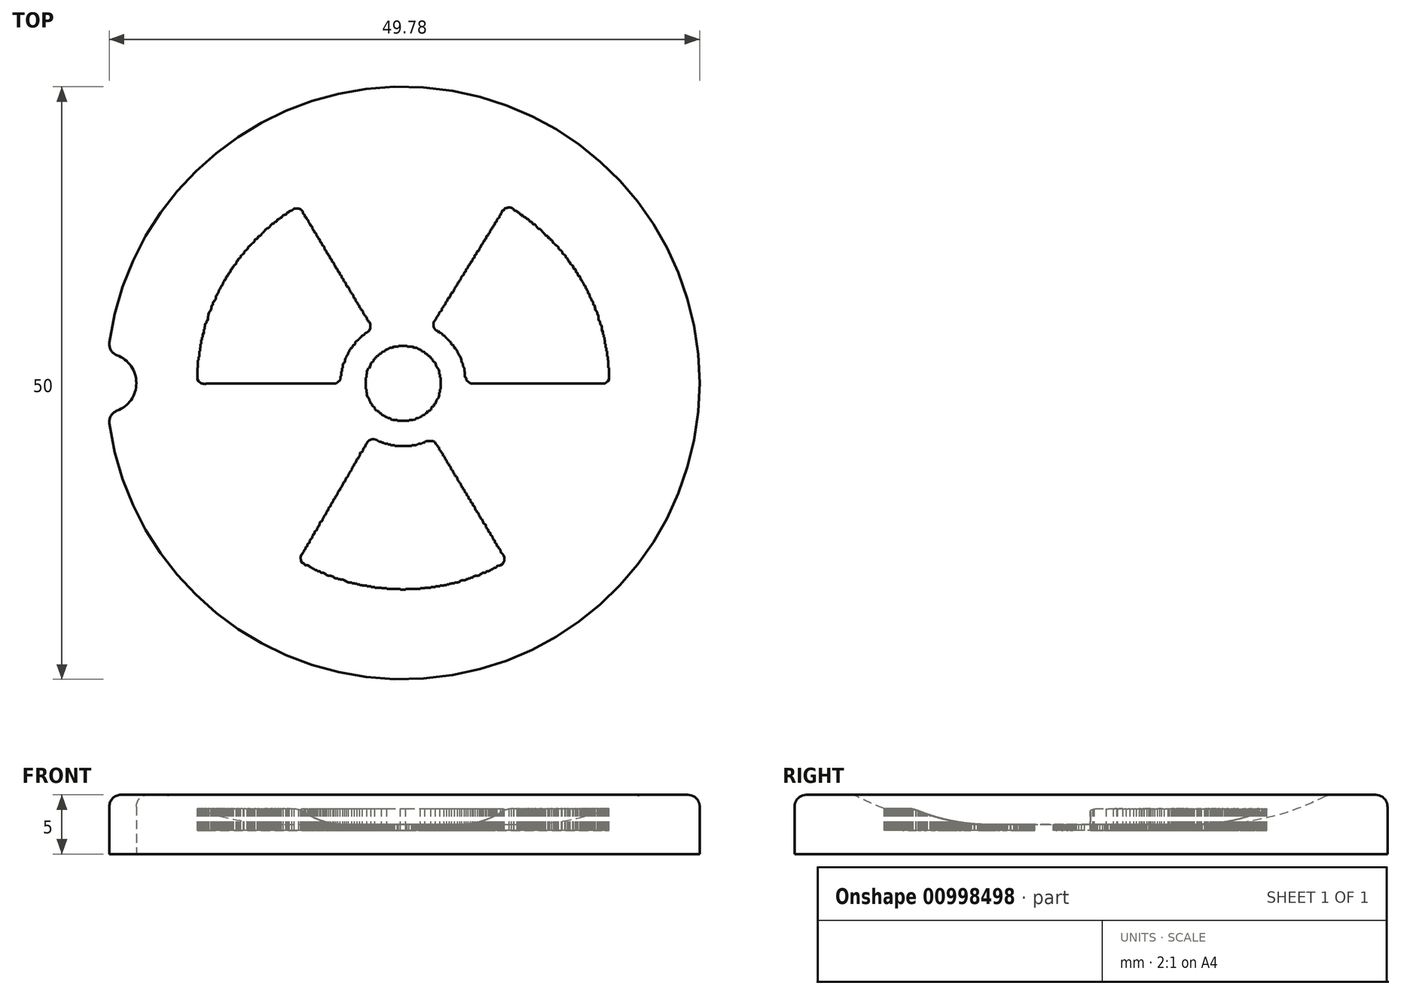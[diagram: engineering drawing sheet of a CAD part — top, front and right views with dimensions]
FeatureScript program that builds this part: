
annotation { "Feature Type Name" : "Feature", "Feature Type Description" : "" }
export const myFeature = defineFeature(function(context is Context, id is Id, definition is map)
    precondition{}
    {
        {
            var Q0;
            Q0=qCreatedBy(makeId("Front.planeOp"),FACE);
            var sketch = newSketch(context, id + "F0", { "sketchPlane" : qUnion([Q0])});
            skLineSegment(sketch, "E0.bottom", {"start": v(0, 0) * mm, "end": v(-25, 0) * mm});
            skLineSegment(sketch, "E0.top", {"start": v(-20, 5) * mm, "end": v(-25, 5) * mm});
            skLineSegment(sketch, "E0.left", {"start": v(0, 0) * mm, "end": v(0, 2.5) * mm});
            skLineSegment(sketch, "E0.right", {"start": v(-25, 0) * mm, "end": v(-25, 5) * mm});
            skArc(sketch, "E1", {"start": v(-20, 5) * mm, "mid": v(-15.15, 3.13) * mm, "end": v(-10, 2.5) * mm});
            skLineSegment(sketch, "E2", {"start": v(-10, 2.5) * mm, "end": v(0, 2.5) * mm});
            skPoint(sketch, "E3.orphan", {"position": v(0, 5) * mm});
            skSolve(sketch);
        }
        {
            var Q0;
            Q0 = qSketchRegion(id + "F0", true);
            var Q1;
            Q1=sQuery(id+"F0.wireOp",EDGE,"E0.left");
            revolve(context, id + "F1", {"surfaceOperationType" : NewSurfaceOperationType.NEW, "entities" : qUnion([Q0]), "axis" : qUnion([Q1]), "revolveType" : RevolveType.FULL});
        }
        {
            var Q0;
            Q0=makeQuery(id+"F1.opRevolve","SWEPT_EDGE",EDGE,{"disambiguationData":[OSD([sQuery(id+"F0.wireOp",EDGE,"E0.top"),sQuery(id+"F0.wireOp",EDGE,"E0.right")])]});
            var Q1;
            Q1=makeQuery(id+"F1.opRevolve","SWEPT_FACE",FACE,{"disambiguationData":[OSD([sQuery(id+"F0.wireOp",EDGE,"E2")])]});
            var Q2;
            Q2=makeQuery(id+"F1.opRevolve","SWEPT_EDGE",EDGE,{"disambiguationData":[OSD([sQuery(id+"F0.wireOp",EDGE,"E0.top"),sQuery(id+"F0.wireOp",EDGE,"E1")])]});
            fillet(context, id + "F2", {"entities" : qUnion([Q0, Q1, Q2]), "radius" : 1 * mm, "tangentPropagation" : true, "allowEdgeOverflow" : false});
        }
        {
            var Q0;
            Q0=qCreatedBy(makeId("Top.planeOp"),FACE);
            var sketch = newSketch(context, id + "F3", { "sketchPlane" : qUnion([Q0])});
            skLineSegment(sketch, "E4", {"start": v(0, 0) * mm, "end": v(-25, 0) * mm});
            skCircle(sketch, "E5", {"center": v(-25, 0) * mm, "radius": 2.5 * mm});
            skSolve(sketch);
        }
        {
            var Q0;
            Q0 = qSketchRegion(id + "F3", true);
            extrude(context, id + "F4", {"entities" : qUnion([Q0]), "operationType" : NewBodyOperationType.REMOVE, "depth" : 25 * mm, "offsetDistance" : 25 * mm});
        }
        {
            var Q0;
            Q0=makeQuery(id+"F4.boolean.opBoolean","INTERSECT",EDGE,{"derivedFrom":[makeQuery(id+"F1.opRevolve","SWEPT_FACE",FACE,{"disambiguationData":[OSD([sQuery(id+"F0.wireOp",EDGE,"E0.top")])]}),makeQuery(id+"F4.opExtrude","SWEPT_FACE",FACE,{"disambiguationData":[OSD([sQuery(id+"F3.wireOp",EDGE,"E5")])]})]});
            fillet(context, id + "F5", {"entities" : qUnion([Q0]), "radius" : 1 * mm, "tangentPropagation" : true, "allowEdgeOverflow" : false});
        }
        {
            var Q0;
            Q0=qCreatedBy(makeId("Top.planeOp"),FACE);
            cPlane(context, id + "F6", {"entities" : qUnion([Q0]), "cplaneType" : CPlaneType.OFFSET, "offset" : 5 * mm, "width" : 150 * mm, "height" : 150 * mm});
        }
        {
            var Q0;
            Q0=qCreatedBy(id+"F6.planeOp",FACE);
            var sketch = newSketch(context, id + "F7", { "sketchPlane" : qUnion([Q0])});
            skLineSegment(sketch, "E6", {"start": v(8.93, 14.83) * mm, "end": v(8.54, 14.72) * mm});
            skLineSegment(sketch, "E7", {"start": v(8.54, 14.72) * mm, "end": v(8.48, 14.56) * mm});
            skLineSegment(sketch, "E8", {"start": v(8.48, 14.56) * mm, "end": v(8.37, 14.56) * mm});
            skLineSegment(sketch, "E9", {"start": v(8.37, 14.56) * mm, "end": v(8.32, 14.45) * mm});
            skLineSegment(sketch, "E10", {"start": v(8.32, 14.45) * mm, "end": v(8.32, 14.33) * mm});
            skLineSegment(sketch, "E11", {"start": v(8.32, 14.33) * mm, "end": v(8.26, 14.33) * mm});
            skLineSegment(sketch, "E12", {"start": v(8.26, 14.33) * mm, "end": v(8.26, 14.22) * mm});
            skLineSegment(sketch, "E13", {"start": v(8.26, 14.22) * mm, "end": v(8.15, 14.17) * mm});
            skLineSegment(sketch, "E14", {"start": v(8.15, 14.17) * mm, "end": v(8.1, 13.95) * mm});
            skLineSegment(sketch, "E15", {"start": v(8.1, 13.95) * mm, "end": v(7.93, 13.84) * mm});
            skLineSegment(sketch, "E16", {"start": v(7.93, 13.84) * mm, "end": v(7.87, 13.61) * mm});
            skLineSegment(sketch, "E17", {"start": v(7.87, 13.61) * mm, "end": v(7.76, 13.56) * mm});
            skLineSegment(sketch, "E18", {"start": v(7.76, 13.56) * mm, "end": v(7.7, 13.34) * mm});
            skLineSegment(sketch, "E19", {"start": v(7.7, 13.34) * mm, "end": v(7.6, 13.28) * mm});
            skLineSegment(sketch, "E20", {"start": v(7.6, 13.28) * mm, "end": v(7.6, 13.17) * mm});
            skLineSegment(sketch, "E21", {"start": v(7.6, 13.17) * mm, "end": v(7.49, 13.11) * mm});
            skLineSegment(sketch, "E22", {"start": v(7.49, 13.11) * mm, "end": v(7.49, 13) * mm});
            skLineSegment(sketch, "E23", {"start": v(7.49, 13) * mm, "end": v(7.38, 12.95) * mm});
            skLineSegment(sketch, "E24", {"start": v(7.38, 12.95) * mm, "end": v(7.38, 12.84) * mm});
            skLineSegment(sketch, "E25", {"start": v(7.38, 12.84) * mm, "end": v(7.32, 12.84) * mm});
            skLineSegment(sketch, "E26", {"start": v(7.32, 12.84) * mm, "end": v(7.32, 12.73) * mm});
            skLineSegment(sketch, "E27", {"start": v(7.32, 12.73) * mm, "end": v(7.26, 12.62) * mm});
            skLineSegment(sketch, "E28", {"start": v(7.26, 12.62) * mm, "end": v(7.15, 12.56) * mm});
            skLineSegment(sketch, "E29", {"start": v(7.15, 12.56) * mm, "end": v(7.15, 12.45) * mm});
            skLineSegment(sketch, "E30", {"start": v(7.15, 12.45) * mm, "end": v(7.04, 12.4) * mm});
            skLineSegment(sketch, "E31", {"start": v(7.04, 12.4) * mm, "end": v(6.99, 12.17) * mm});
            skLineSegment(sketch, "E32", {"start": v(6.99, 12.17) * mm, "end": v(6.88, 12.12) * mm});
            skLineSegment(sketch, "E33", {"start": v(6.88, 12.12) * mm, "end": v(6.88, 12) * mm});
            skLineSegment(sketch, "E34", {"start": v(6.88, 12) * mm, "end": v(6.77, 11.95) * mm});
            skLineSegment(sketch, "E35", {"start": v(6.77, 11.95) * mm, "end": v(6.7, 11.73) * mm});
            skLineSegment(sketch, "E36", {"start": v(6.7, 11.73) * mm, "end": v(6.6, 11.67) * mm});
            skLineSegment(sketch, "E37", {"start": v(6.6, 11.67) * mm, "end": v(6.6, 11.56) * mm});
            skLineSegment(sketch, "E38", {"start": v(6.6, 11.56) * mm, "end": v(6.49, 11.5) * mm});
            skLineSegment(sketch, "E39", {"start": v(6.49, 11.5) * mm, "end": v(6.49, 11.4) * mm});
            skLineSegment(sketch, "E40", {"start": v(6.49, 11.4) * mm, "end": v(6.43, 11.4) * mm});
            skLineSegment(sketch, "E41", {"start": v(6.43, 11.4) * mm, "end": v(6.43, 11.28) * mm});
            skLineSegment(sketch, "E42", {"start": v(6.43, 11.28) * mm, "end": v(6.38, 11.17) * mm});
            skLineSegment(sketch, "E43", {"start": v(6.38, 11.17) * mm, "end": v(6.21, 11.06) * mm});
            skLineSegment(sketch, "E44", {"start": v(6.21, 11.06) * mm, "end": v(6.16, 10.84) * mm});
            skLineSegment(sketch, "E45", {"start": v(6.16, 10.84) * mm, "end": v(6.04, 10.79) * mm});
            skLineSegment(sketch, "E46", {"start": v(6.04, 10.79) * mm, "end": v(5.99, 10.56) * mm});
            skLineSegment(sketch, "E47", {"start": v(5.99, 10.56) * mm, "end": v(5.88, 10.5) * mm});
            skLineSegment(sketch, "E48", {"start": v(5.88, 10.5) * mm, "end": v(5.82, 10.29) * mm});
            skLineSegment(sketch, "E49", {"start": v(5.82, 10.29) * mm, "end": v(5.71, 10.23) * mm});
            skLineSegment(sketch, "E50", {"start": v(5.71, 10.23) * mm, "end": v(5.71, 10.12) * mm});
            skLineSegment(sketch, "E51", {"start": v(5.71, 10.12) * mm, "end": v(5.6, 10.06) * mm});
            skLineSegment(sketch, "E52", {"start": v(5.6, 10.06) * mm, "end": v(5.6, 9.95) * mm});
            skLineSegment(sketch, "E53", {"start": v(5.6, 9.95) * mm, "end": v(5.49, 9.9) * mm});
            skLineSegment(sketch, "E54", {"start": v(5.49, 9.9) * mm, "end": v(5.43, 9.68) * mm});
            skLineSegment(sketch, "E55", {"start": v(5.43, 9.68) * mm, "end": v(5.32, 9.62) * mm});
            skLineSegment(sketch, "E56", {"start": v(5.32, 9.62) * mm, "end": v(5.27, 9.4) * mm});
            skLineSegment(sketch, "E57", {"start": v(5.27, 9.4) * mm, "end": v(5.16, 9.34) * mm});
            skLineSegment(sketch, "E58", {"start": v(5.16, 9.34) * mm, "end": v(5.1, 9.12) * mm});
            skLineSegment(sketch, "E59", {"start": v(5.1, 9.12) * mm, "end": v(4.94, 9.01) * mm});
            skLineSegment(sketch, "E60", {"start": v(4.94, 9.01) * mm, "end": v(4.82, 8.68) * mm});
            skLineSegment(sketch, "E61", {"start": v(4.82, 8.68) * mm, "end": v(4.71, 8.62) * mm});
            skLineSegment(sketch, "E62", {"start": v(4.71, 8.62) * mm, "end": v(4.71, 8.51) * mm});
            skLineSegment(sketch, "E63", {"start": v(4.71, 8.51) * mm, "end": v(4.6, 8.46) * mm});
            skLineSegment(sketch, "E64", {"start": v(4.6, 8.46) * mm, "end": v(4.55, 8.23) * mm});
            skLineSegment(sketch, "E65", {"start": v(4.55, 8.23) * mm, "end": v(4.44, 8.18) * mm});
            skLineSegment(sketch, "E66", {"start": v(4.44, 8.18) * mm, "end": v(4.44, 8.07) * mm});
            skLineSegment(sketch, "E67", {"start": v(4.44, 8.07) * mm, "end": v(4.33, 8.01) * mm});
            skLineSegment(sketch, "E68", {"start": v(4.33, 8.01) * mm, "end": v(4.33, 7.9) * mm});
            skLineSegment(sketch, "E69", {"start": v(4.33, 7.9) * mm, "end": v(4.27, 7.9) * mm});
            skLineSegment(sketch, "E70", {"start": v(4.27, 7.9) * mm, "end": v(4.27, 7.8) * mm});
            skLineSegment(sketch, "E71", {"start": v(4.27, 7.8) * mm, "end": v(4.21, 7.68) * mm});
            skLineSegment(sketch, "E72", {"start": v(4.21, 7.68) * mm, "end": v(4.05, 7.57) * mm});
            skLineSegment(sketch, "E73", {"start": v(4.05, 7.57) * mm, "end": v(3.94, 7.24) * mm});
            skLineSegment(sketch, "E74", {"start": v(3.94, 7.24) * mm, "end": v(3.77, 7.13) * mm});
            skLineSegment(sketch, "E75", {"start": v(3.77, 7.13) * mm, "end": v(3.72, 6.9) * mm});
            skLineSegment(sketch, "E76", {"start": v(3.72, 6.9) * mm, "end": v(3.6, 6.85) * mm});
            skLineSegment(sketch, "E77", {"start": v(3.6, 6.85) * mm, "end": v(3.55, 6.63) * mm});
            skLineSegment(sketch, "E78", {"start": v(3.55, 6.63) * mm, "end": v(3.44, 6.57) * mm});
            skLineSegment(sketch, "E79", {"start": v(3.44, 6.57) * mm, "end": v(3.44, 6.46) * mm});
            skLineSegment(sketch, "E80", {"start": v(3.44, 6.46) * mm, "end": v(3.33, 6.4) * mm});
            skLineSegment(sketch, "E81", {"start": v(3.33, 6.4) * mm, "end": v(3.33, 6.3) * mm});
            skLineSegment(sketch, "E82", {"start": v(3.33, 6.3) * mm, "end": v(3.27, 6.3) * mm});
            skLineSegment(sketch, "E83", {"start": v(3.27, 6.3) * mm, "end": v(3.27, 6.18) * mm});
            skLineSegment(sketch, "E84", {"start": v(3.27, 6.18) * mm, "end": v(3.22, 6.07) * mm});
            skLineSegment(sketch, "E85", {"start": v(3.22, 6.07) * mm, "end": v(3.05, 5.96) * mm});
            skLineSegment(sketch, "E86", {"start": v(3.05, 5.96) * mm, "end": v(3, 5.74) * mm});
            skLineSegment(sketch, "E87", {"start": v(3, 5.74) * mm, "end": v(2.88, 5.68) * mm});
            skLineSegment(sketch, "E88", {"start": v(2.88, 5.68) * mm, "end": v(2.88, 5.57) * mm});
            skLineSegment(sketch, "E89", {"start": v(2.88, 5.57) * mm, "end": v(2.77, 5.52) * mm});
            skLineSegment(sketch, "E90", {"start": v(2.77, 5.52) * mm, "end": v(2.77, 5.4) * mm});
            skLineSegment(sketch, "E91", {"start": v(2.77, 5.4) * mm, "end": v(2.72, 5.4) * mm});
            skLineSegment(sketch, "E92", {"start": v(2.72, 5.4) * mm, "end": v(2.72, 5.3) * mm});
            skLineSegment(sketch, "E93", {"start": v(2.72, 5.3) * mm, "end": v(2.66, 5.3) * mm});
            skLineSegment(sketch, "E94", {"start": v(2.66, 5.3) * mm, "end": v(2.66, 5.18) * mm});
            skLineSegment(sketch, "E95", {"start": v(2.66, 5.18) * mm, "end": v(2.6, 5.18) * mm});
            skLineSegment(sketch, "E96", {"start": v(2.6, 5.18) * mm, "end": v(2.55, 5.07) * mm});
            skLineSegment(sketch, "E97", {"start": v(2.55, 5.07) * mm, "end": v(2.55, 4.74) * mm});
            skLineSegment(sketch, "E98", {"start": v(2.55, 4.74) * mm, "end": v(2.66, 4.57) * mm});
            skLineSegment(sketch, "E99", {"start": v(2.66, 4.57) * mm, "end": v(2.83, 4.4) * mm});
            skLineSegment(sketch, "E100", {"start": v(2.83, 4.4) * mm, "end": v(2.94, 4.4) * mm});
            skLineSegment(sketch, "E101", {"start": v(2.94, 4.4) * mm, "end": v(3.05, 4.24) * mm});
            skLineSegment(sketch, "E102", {"start": v(3.05, 4.24) * mm, "end": v(3.16, 4.24) * mm});
            skLineSegment(sketch, "E103", {"start": v(3.16, 4.24) * mm, "end": v(3.33, 4.13) * mm});
            skLineSegment(sketch, "E104", {"start": v(3.33, 4.13) * mm, "end": v(3.33, 4.02) * mm});
            skLineSegment(sketch, "E105", {"start": v(3.33, 4.02) * mm, "end": v(3.44, 4.02) * mm});
            skLineSegment(sketch, "E106", {"start": v(3.44, 4.02) * mm, "end": v(3.5, 3.96) * mm});
            skLineSegment(sketch, "E107", {"start": v(3.5, 3.96) * mm, "end": v(3.55, 3.9) * mm});
            skLineSegment(sketch, "E108", {"start": v(3.55, 3.9) * mm, "end": v(3.55, 3.85) * mm});
            skLineSegment(sketch, "E109", {"start": v(3.55, 3.85) * mm, "end": v(3.6, 3.85) * mm});
            skLineSegment(sketch, "E110", {"start": v(3.6, 3.85) * mm, "end": v(3.6, 3.8) * mm});
            skLineSegment(sketch, "E111", {"start": v(3.6, 3.8) * mm, "end": v(3.66, 3.8) * mm});
            skLineSegment(sketch, "E112", {"start": v(3.66, 3.8) * mm, "end": v(3.66, 3.74) * mm});
            skLineSegment(sketch, "E113", {"start": v(3.66, 3.74) * mm, "end": v(3.72, 3.74) * mm});
            skLineSegment(sketch, "E114", {"start": v(3.72, 3.74) * mm, "end": v(3.72, 3.69) * mm});
            skLineSegment(sketch, "E115", {"start": v(3.72, 3.69) * mm, "end": v(3.77, 3.69) * mm});
            skLineSegment(sketch, "E116", {"start": v(3.77, 3.69) * mm, "end": v(3.77, 3.63) * mm});
            skLineSegment(sketch, "E117", {"start": v(3.77, 3.63) * mm, "end": v(3.83, 3.63) * mm});
            skLineSegment(sketch, "E118", {"start": v(3.83, 3.63) * mm, "end": v(3.83, 3.58) * mm});
            skLineSegment(sketch, "E119", {"start": v(3.83, 3.58) * mm, "end": v(3.88, 3.58) * mm});
            skLineSegment(sketch, "E120", {"start": v(3.88, 3.58) * mm, "end": v(3.88, 3.52) * mm});
            skLineSegment(sketch, "E121", {"start": v(3.88, 3.52) * mm, "end": v(3.94, 3.52) * mm});
            skLineSegment(sketch, "E122", {"start": v(3.94, 3.52) * mm, "end": v(3.94, 3.47) * mm});
            skLineSegment(sketch, "E123", {"start": v(3.94, 3.47) * mm, "end": v(4.05, 3.41) * mm});
            skLineSegment(sketch, "E124", {"start": v(4.05, 3.41) * mm, "end": v(4.05, 3.3) * mm});
            skLineSegment(sketch, "E125", {"start": v(4.05, 3.3) * mm, "end": v(4.1, 3.24) * mm});
            skLineSegment(sketch, "E126", {"start": v(4.1, 3.24) * mm, "end": v(4.21, 3.19) * mm});
            skLineSegment(sketch, "E127", {"start": v(4.21, 3.19) * mm, "end": v(4.27, 3.13) * mm});
            skLineSegment(sketch, "E128", {"start": v(4.27, 3.13) * mm, "end": v(4.27, 3.02) * mm});
            skLineSegment(sketch, "E129", {"start": v(4.27, 3.02) * mm, "end": v(4.44, 2.91) * mm});
            skLineSegment(sketch, "E130", {"start": v(4.44, 2.91) * mm, "end": v(4.44, 2.8) * mm});
            skLineSegment(sketch, "E131", {"start": v(4.44, 2.8) * mm, "end": v(4.55, 2.74) * mm});
            skLineSegment(sketch, "E132", {"start": v(4.55, 2.74) * mm, "end": v(4.6, 2.52) * mm});
            skLineSegment(sketch, "E133", {"start": v(4.6, 2.52) * mm, "end": v(4.66, 2.52) * mm});
            skLineSegment(sketch, "E134", {"start": v(4.66, 2.52) * mm, "end": v(4.66, 2.41) * mm});
            skLineSegment(sketch, "E135", {"start": v(4.66, 2.41) * mm, "end": v(4.71, 2.41) * mm});
            skLineSegment(sketch, "E136", {"start": v(4.71, 2.41) * mm, "end": v(4.71, 2.3) * mm});
            skLineSegment(sketch, "E137", {"start": v(4.71, 2.3) * mm, "end": v(4.77, 2.3) * mm});
            skLineSegment(sketch, "E138", {"start": v(4.77, 2.3) * mm, "end": v(4.77, 2.2) * mm});
            skLineSegment(sketch, "E139", {"start": v(4.77, 2.2) * mm, "end": v(4.82, 2.2) * mm});
            skLineSegment(sketch, "E140", {"start": v(4.82, 2.2) * mm, "end": v(4.88, 2.08) * mm});
            skLineSegment(sketch, "E141", {"start": v(4.88, 2.08) * mm, "end": v(4.94, 1.75) * mm});
            skLineSegment(sketch, "E142", {"start": v(4.94, 1.75) * mm, "end": v(5.05, 1.64) * mm});
            skLineSegment(sketch, "E143", {"start": v(5.05, 1.64) * mm, "end": v(5.05, 1.41) * mm});
            skLineSegment(sketch, "E144", {"start": v(5.05, 1.41) * mm, "end": v(5.16, 1.25) * mm});
            skLineSegment(sketch, "E145", {"start": v(5.16, 1.25) * mm, "end": v(5.16, 0.97) * mm});
            skLineSegment(sketch, "E146", {"start": v(5.16, 0.97) * mm, "end": v(5.21, 0.97) * mm});
            skLineSegment(sketch, "E147", {"start": v(5.21, 0.97) * mm, "end": v(5.21, 0.58) * mm});
            skLineSegment(sketch, "E148", {"start": v(5.21, 0.58) * mm, "end": v(5.27, 0.42) * mm});
            skLineSegment(sketch, "E149", {"start": v(5.27, 0.42) * mm, "end": v(5.32, 0.42) * mm});
            skLineSegment(sketch, "E150", {"start": v(5.32, 0.42) * mm, "end": v(5.32, 0.25) * mm});
            skLineSegment(sketch, "E151", {"start": v(5.32, 0.25) * mm, "end": v(5.66, -0.03) * mm});
            skLineSegment(sketch, "E152", {"start": v(5.66, -0.03) * mm, "end": v(5.88, -0.03) * mm});
            skLineSegment(sketch, "E153", {"start": v(5.88, -0.03) * mm, "end": v(5.93, -0.03) * mm});
            skLineSegment(sketch, "E154", {"start": v(5.93, -0.03) * mm, "end": v(5.99, -0.03) * mm});
            skLineSegment(sketch, "E155", {"start": v(5.99, -0.03) * mm, "end": v(6.04, -0.03) * mm});
            skLineSegment(sketch, "E156", {"start": v(6.04, -0.03) * mm, "end": v(6.1, -0.03) * mm});
            skLineSegment(sketch, "E157", {"start": v(6.1, -0.03) * mm, "end": v(6.16, -0.03) * mm});
            skLineSegment(sketch, "E158", {"start": v(6.16, -0.03) * mm, "end": v(6.21, -0.03) * mm});
            skLineSegment(sketch, "E159", {"start": v(6.21, -0.03) * mm, "end": v(6.27, -0.03) * mm});
            skLineSegment(sketch, "E160", {"start": v(6.27, -0.03) * mm, "end": v(6.32, -0.03) * mm});
            skLineSegment(sketch, "E161", {"start": v(6.32, -0.03) * mm, "end": v(6.38, -0.03) * mm});
            skLineSegment(sketch, "E162", {"start": v(6.38, -0.03) * mm, "end": v(6.43, -0.03) * mm});
            skLineSegment(sketch, "E163", {"start": v(6.43, -0.03) * mm, "end": v(6.49, -0.03) * mm});
            skLineSegment(sketch, "E164", {"start": v(6.49, -0.03) * mm, "end": v(6.54, -0.03) * mm});
            skLineSegment(sketch, "E165", {"start": v(6.54, -0.03) * mm, "end": v(6.6, -0.03) * mm});
            skLineSegment(sketch, "E166", {"start": v(6.6, -0.03) * mm, "end": v(6.65, -0.03) * mm});
            skLineSegment(sketch, "E167", {"start": v(6.65, -0.03) * mm, "end": v(6.7, -0.03) * mm});
            skLineSegment(sketch, "E168", {"start": v(6.7, -0.03) * mm, "end": v(6.77, -0.03) * mm});
            skLineSegment(sketch, "E169", {"start": v(6.77, -0.03) * mm, "end": v(6.82, -0.03) * mm});
            skLineSegment(sketch, "E170", {"start": v(6.82, -0.03) * mm, "end": v(6.88, -0.03) * mm});
            skLineSegment(sketch, "E171", {"start": v(6.88, -0.03) * mm, "end": v(6.93, -0.03) * mm});
            skLineSegment(sketch, "E172", {"start": v(6.93, -0.03) * mm, "end": v(6.99, -0.03) * mm});
            skLineSegment(sketch, "E173", {"start": v(6.99, -0.03) * mm, "end": v(7.04, -0.03) * mm});
            skLineSegment(sketch, "E174", {"start": v(7.04, -0.03) * mm, "end": v(7.1, -0.03) * mm});
            skLineSegment(sketch, "E175", {"start": v(7.1, -0.03) * mm, "end": v(7.15, -0.03) * mm});
            skLineSegment(sketch, "E176", {"start": v(7.15, -0.03) * mm, "end": v(7.2, -0.03) * mm});
            skLineSegment(sketch, "E177", {"start": v(7.2, -0.03) * mm, "end": v(7.26, -0.03) * mm});
            skLineSegment(sketch, "E178", {"start": v(7.26, -0.03) * mm, "end": v(7.32, -0.03) * mm});
            skLineSegment(sketch, "E179", {"start": v(7.32, -0.03) * mm, "end": v(7.38, -0.03) * mm});
            skLineSegment(sketch, "E180", {"start": v(7.38, -0.03) * mm, "end": v(7.43, -0.03) * mm});
            skLineSegment(sketch, "E181", {"start": v(7.43, -0.03) * mm, "end": v(7.49, -0.03) * mm});
            skLineSegment(sketch, "E182", {"start": v(7.49, -0.03) * mm, "end": v(7.54, -0.03) * mm});
            skLineSegment(sketch, "E183", {"start": v(7.54, -0.03) * mm, "end": v(7.6, -0.03) * mm});
            skLineSegment(sketch, "E184", {"start": v(7.6, -0.03) * mm, "end": v(7.65, -0.03) * mm});
            skLineSegment(sketch, "E185", {"start": v(7.65, -0.03) * mm, "end": v(7.7, -0.03) * mm});
            skLineSegment(sketch, "E186", {"start": v(7.7, -0.03) * mm, "end": v(7.76, -0.03) * mm});
            skLineSegment(sketch, "E187", {"start": v(7.76, -0.03) * mm, "end": v(7.82, -0.03) * mm});
            skLineSegment(sketch, "E188", {"start": v(7.82, -0.03) * mm, "end": v(7.87, -0.03) * mm});
            skLineSegment(sketch, "E189", {"start": v(7.87, -0.03) * mm, "end": v(7.93, -0.03) * mm});
            skLineSegment(sketch, "E190", {"start": v(7.93, -0.03) * mm, "end": v(7.99, -0.03) * mm});
            skLineSegment(sketch, "E191", {"start": v(7.99, -0.03) * mm, "end": v(8.04, -0.03) * mm});
            skLineSegment(sketch, "E192", {"start": v(8.04, -0.03) * mm, "end": v(8.1, -0.03) * mm});
            skLineSegment(sketch, "E193", {"start": v(8.1, -0.03) * mm, "end": v(8.15, -0.03) * mm});
            skLineSegment(sketch, "E194", {"start": v(8.15, -0.03) * mm, "end": v(8.2, -0.03) * mm});
            skLineSegment(sketch, "E195", {"start": v(8.2, -0.03) * mm, "end": v(8.26, -0.03) * mm});
            skLineSegment(sketch, "E196", {"start": v(8.26, -0.03) * mm, "end": v(8.32, -0.03) * mm});
            skLineSegment(sketch, "E197", {"start": v(8.32, -0.03) * mm, "end": v(8.37, -0.03) * mm});
            skLineSegment(sketch, "E198", {"start": v(8.37, -0.03) * mm, "end": v(8.43, -0.03) * mm});
            skLineSegment(sketch, "E199", {"start": v(8.43, -0.03) * mm, "end": v(8.48, -0.03) * mm});
            skLineSegment(sketch, "E200", {"start": v(8.48, -0.03) * mm, "end": v(8.54, -0.03) * mm});
            skLineSegment(sketch, "E201", {"start": v(8.54, -0.03) * mm, "end": v(8.6, -0.03) * mm});
            skLineSegment(sketch, "E202", {"start": v(8.6, -0.03) * mm, "end": v(8.65, -0.03) * mm});
            skLineSegment(sketch, "E203", {"start": v(8.65, -0.03) * mm, "end": v(8.7, -0.03) * mm});
            skLineSegment(sketch, "E204", {"start": v(8.7, -0.03) * mm, "end": v(8.76, -0.03) * mm});
            skLineSegment(sketch, "E205", {"start": v(8.76, -0.03) * mm, "end": v(8.82, -0.03) * mm});
            skLineSegment(sketch, "E206", {"start": v(8.82, -0.03) * mm, "end": v(8.87, -0.03) * mm});
            skLineSegment(sketch, "E207", {"start": v(8.87, -0.03) * mm, "end": v(8.93, -0.03) * mm});
            skLineSegment(sketch, "E208", {"start": v(8.93, -0.03) * mm, "end": v(8.98, -0.03) * mm});
            skLineSegment(sketch, "E209", {"start": v(8.98, -0.03) * mm, "end": v(9.04, -0.03) * mm});
            skLineSegment(sketch, "E210", {"start": v(9.04, -0.03) * mm, "end": v(9.1, -0.03) * mm});
            skLineSegment(sketch, "E211", {"start": v(9.1, -0.03) * mm, "end": v(9.15, -0.03) * mm});
            skLineSegment(sketch, "E212", {"start": v(9.15, -0.03) * mm, "end": v(9.2, -0.03) * mm});
            skLineSegment(sketch, "E213", {"start": v(9.2, -0.03) * mm, "end": v(9.26, -0.03) * mm});
            skLineSegment(sketch, "E214", {"start": v(9.26, -0.03) * mm, "end": v(9.32, -0.03) * mm});
            skLineSegment(sketch, "E215", {"start": v(9.32, -0.03) * mm, "end": v(9.37, -0.03) * mm});
            skLineSegment(sketch, "E216", {"start": v(9.37, -0.03) * mm, "end": v(9.43, -0.03) * mm});
            skLineSegment(sketch, "E217", {"start": v(9.43, -0.03) * mm, "end": v(9.48, -0.03) * mm});
            skLineSegment(sketch, "E218", {"start": v(9.48, -0.03) * mm, "end": v(9.54, -0.03) * mm});
            skLineSegment(sketch, "E219", {"start": v(9.54, -0.03) * mm, "end": v(9.6, -0.03) * mm});
            skLineSegment(sketch, "E220", {"start": v(9.6, -0.03) * mm, "end": v(9.65, -0.03) * mm});
            skLineSegment(sketch, "E221", {"start": v(9.65, -0.03) * mm, "end": v(9.7, -0.03) * mm});
            skLineSegment(sketch, "E222", {"start": v(9.7, -0.03) * mm, "end": v(9.76, -0.03) * mm});
            skLineSegment(sketch, "E223", {"start": v(9.76, -0.03) * mm, "end": v(9.82, -0.03) * mm});
            skLineSegment(sketch, "E224", {"start": v(9.82, -0.03) * mm, "end": v(9.87, -0.03) * mm});
            skLineSegment(sketch, "E225", {"start": v(9.87, -0.03) * mm, "end": v(9.93, -0.03) * mm});
            skLineSegment(sketch, "E226", {"start": v(9.93, -0.03) * mm, "end": v(9.98, -0.03) * mm});
            skLineSegment(sketch, "E227", {"start": v(9.98, -0.03) * mm, "end": v(10.04, -0.03) * mm});
            skLineSegment(sketch, "E228", {"start": v(10.04, -0.03) * mm, "end": v(10.1, -0.03) * mm});
            skLineSegment(sketch, "E229", {"start": v(10.1, -0.03) * mm, "end": v(10.15, -0.03) * mm});
            skLineSegment(sketch, "E230", {"start": v(10.15, -0.03) * mm, "end": v(10.2, -0.03) * mm});
            skLineSegment(sketch, "E231", {"start": v(10.2, -0.03) * mm, "end": v(10.26, -0.03) * mm});
            skLineSegment(sketch, "E232", {"start": v(10.26, -0.03) * mm, "end": v(10.31, -0.03) * mm});
            skLineSegment(sketch, "E233", {"start": v(10.31, -0.03) * mm, "end": v(10.37, -0.03) * mm});
            skLineSegment(sketch, "E234", {"start": v(10.37, -0.03) * mm, "end": v(10.43, -0.03) * mm});
            skLineSegment(sketch, "E235", {"start": v(10.43, -0.03) * mm, "end": v(10.48, -0.03) * mm});
            skLineSegment(sketch, "E236", {"start": v(10.48, -0.03) * mm, "end": v(10.54, -0.03) * mm});
            skLineSegment(sketch, "E237", {"start": v(10.54, -0.03) * mm, "end": v(10.6, -0.03) * mm});
            skLineSegment(sketch, "E238", {"start": v(10.6, -0.03) * mm, "end": v(10.65, -0.03) * mm});
            skLineSegment(sketch, "E239", {"start": v(10.65, -0.03) * mm, "end": v(10.7, -0.03) * mm});
            skLineSegment(sketch, "E240", {"start": v(10.7, -0.03) * mm, "end": v(10.76, -0.03) * mm});
            skLineSegment(sketch, "E241", {"start": v(10.76, -0.03) * mm, "end": v(10.81, -0.03) * mm});
            skLineSegment(sketch, "E242", {"start": v(10.81, -0.03) * mm, "end": v(10.87, -0.03) * mm});
            skLineSegment(sketch, "E243", {"start": v(10.87, -0.03) * mm, "end": v(10.92, -0.03) * mm});
            skLineSegment(sketch, "E244", {"start": v(10.92, -0.03) * mm, "end": v(10.98, -0.03) * mm});
            skLineSegment(sketch, "E245", {"start": v(10.98, -0.03) * mm, "end": v(11.04, -0.03) * mm});
            skLineSegment(sketch, "E246", {"start": v(11.04, -0.03) * mm, "end": v(11.1, -0.03) * mm});
            skLineSegment(sketch, "E247", {"start": v(11.1, -0.03) * mm, "end": v(11.15, -0.03) * mm});
            skLineSegment(sketch, "E248", {"start": v(11.15, -0.03) * mm, "end": v(11.2, -0.03) * mm});
            skLineSegment(sketch, "E249", {"start": v(11.2, -0.03) * mm, "end": v(11.26, -0.03) * mm});
            skLineSegment(sketch, "E250", {"start": v(11.26, -0.03) * mm, "end": v(11.31, -0.03) * mm});
            skLineSegment(sketch, "E251", {"start": v(11.31, -0.03) * mm, "end": v(11.37, -0.03) * mm});
            skLineSegment(sketch, "E252", {"start": v(11.37, -0.03) * mm, "end": v(11.42, -0.03) * mm});
            skLineSegment(sketch, "E253", {"start": v(11.42, -0.03) * mm, "end": v(11.48, -0.03) * mm});
            skLineSegment(sketch, "E254", {"start": v(11.48, -0.03) * mm, "end": v(11.53, -0.03) * mm});
            skLineSegment(sketch, "E255", {"start": v(11.53, -0.03) * mm, "end": v(11.59, -0.03) * mm});
            skLineSegment(sketch, "E256", {"start": v(11.59, -0.03) * mm, "end": v(11.65, -0.03) * mm});
            skLineSegment(sketch, "E257", {"start": v(11.65, -0.03) * mm, "end": v(11.7, -0.03) * mm});
            skLineSegment(sketch, "E258", {"start": v(11.7, -0.03) * mm, "end": v(11.76, -0.03) * mm});
            skLineSegment(sketch, "E259", {"start": v(11.76, -0.03) * mm, "end": v(11.81, -0.03) * mm});
            skLineSegment(sketch, "E260", {"start": v(11.81, -0.03) * mm, "end": v(11.87, -0.03) * mm});
            skLineSegment(sketch, "E261", {"start": v(11.87, -0.03) * mm, "end": v(11.92, -0.03) * mm});
            skLineSegment(sketch, "E262", {"start": v(11.92, -0.03) * mm, "end": v(11.98, -0.03) * mm});
            skLineSegment(sketch, "E263", {"start": v(11.98, -0.03) * mm, "end": v(12.03, -0.03) * mm});
            skLineSegment(sketch, "E264", {"start": v(12.03, -0.03) * mm, "end": v(12.09, -0.03) * mm});
            skLineSegment(sketch, "E265", {"start": v(12.09, -0.03) * mm, "end": v(12.14, -0.03) * mm});
            skLineSegment(sketch, "E266", {"start": v(12.14, -0.03) * mm, "end": v(12.2, -0.03) * mm});
            skLineSegment(sketch, "E267", {"start": v(12.2, -0.03) * mm, "end": v(12.26, -0.03) * mm});
            skLineSegment(sketch, "E268", {"start": v(12.26, -0.03) * mm, "end": v(12.31, -0.03) * mm});
            skLineSegment(sketch, "E269", {"start": v(12.31, -0.03) * mm, "end": v(12.37, -0.03) * mm});
            skLineSegment(sketch, "E270", {"start": v(12.37, -0.03) * mm, "end": v(12.42, -0.03) * mm});
            skLineSegment(sketch, "E271", {"start": v(12.42, -0.03) * mm, "end": v(12.48, -0.03) * mm});
            skLineSegment(sketch, "E272", {"start": v(12.48, -0.03) * mm, "end": v(12.53, -0.03) * mm});
            skLineSegment(sketch, "E273", {"start": v(12.53, -0.03) * mm, "end": v(12.59, -0.03) * mm});
            skLineSegment(sketch, "E274", {"start": v(12.59, -0.03) * mm, "end": v(12.64, -0.03) * mm});
            skLineSegment(sketch, "E275", {"start": v(12.64, -0.03) * mm, "end": v(12.7, -0.03) * mm});
            skLineSegment(sketch, "E276", {"start": v(12.7, -0.03) * mm, "end": v(12.75, -0.03) * mm});
            skLineSegment(sketch, "E277", {"start": v(12.75, -0.03) * mm, "end": v(12.8, -0.03) * mm});
            skLineSegment(sketch, "E278", {"start": v(12.8, -0.03) * mm, "end": v(12.87, -0.03) * mm});
            skLineSegment(sketch, "E279", {"start": v(12.87, -0.03) * mm, "end": v(12.92, -0.03) * mm});
            skLineSegment(sketch, "E280", {"start": v(12.92, -0.03) * mm, "end": v(12.98, -0.03) * mm});
            skLineSegment(sketch, "E281", {"start": v(12.98, -0.03) * mm, "end": v(13.03, -0.03) * mm});
            skLineSegment(sketch, "E282", {"start": v(13.03, -0.03) * mm, "end": v(13.09, -0.03) * mm});
            skLineSegment(sketch, "E283", {"start": v(13.09, -0.03) * mm, "end": v(13.14, -0.03) * mm});
            skLineSegment(sketch, "E284", {"start": v(13.14, -0.03) * mm, "end": v(13.2, -0.03) * mm});
            skLineSegment(sketch, "E285", {"start": v(13.2, -0.03) * mm, "end": v(13.25, -0.03) * mm});
            skLineSegment(sketch, "E286", {"start": v(13.25, -0.03) * mm, "end": v(13.3, -0.03) * mm});
            skLineSegment(sketch, "E287", {"start": v(13.3, -0.03) * mm, "end": v(13.36, -0.03) * mm});
            skLineSegment(sketch, "E288", {"start": v(13.36, -0.03) * mm, "end": v(13.42, -0.03) * mm});
            skLineSegment(sketch, "E289", {"start": v(13.42, -0.03) * mm, "end": v(13.47, -0.03) * mm});
            skLineSegment(sketch, "E290", {"start": v(13.47, -0.03) * mm, "end": v(13.53, -0.03) * mm});
            skLineSegment(sketch, "E291", {"start": v(13.53, -0.03) * mm, "end": v(13.59, -0.03) * mm});
            skLineSegment(sketch, "E292", {"start": v(13.59, -0.03) * mm, "end": v(13.64, -0.03) * mm});
            skLineSegment(sketch, "E293", {"start": v(13.64, -0.03) * mm, "end": v(13.7, -0.03) * mm});
            skLineSegment(sketch, "E294", {"start": v(13.7, -0.03) * mm, "end": v(13.75, -0.03) * mm});
            skLineSegment(sketch, "E295", {"start": v(13.75, -0.03) * mm, "end": v(13.8, -0.03) * mm});
            skLineSegment(sketch, "E296", {"start": v(13.8, -0.03) * mm, "end": v(13.86, -0.03) * mm});
            skLineSegment(sketch, "E297", {"start": v(13.86, -0.03) * mm, "end": v(13.92, -0.03) * mm});
            skLineSegment(sketch, "E298", {"start": v(13.92, -0.03) * mm, "end": v(13.97, -0.03) * mm});
            skLineSegment(sketch, "E299", {"start": v(13.97, -0.03) * mm, "end": v(14.03, -0.03) * mm});
            skLineSegment(sketch, "E300", {"start": v(14.03, -0.03) * mm, "end": v(14.08, -0.03) * mm});
            skLineSegment(sketch, "E301", {"start": v(14.08, -0.03) * mm, "end": v(14.14, -0.03) * mm});
            skLineSegment(sketch, "E302", {"start": v(14.14, -0.03) * mm, "end": v(14.2, -0.03) * mm});
            skLineSegment(sketch, "E303", {"start": v(14.2, -0.03) * mm, "end": v(14.25, -0.03) * mm});
            skLineSegment(sketch, "E304", {"start": v(14.25, -0.03) * mm, "end": v(14.3, -0.03) * mm});
            skLineSegment(sketch, "E305", {"start": v(14.3, -0.03) * mm, "end": v(14.36, -0.03) * mm});
            skLineSegment(sketch, "E306", {"start": v(14.36, -0.03) * mm, "end": v(14.42, -0.03) * mm});
            skLineSegment(sketch, "E307", {"start": v(14.42, -0.03) * mm, "end": v(14.47, -0.03) * mm});
            skLineSegment(sketch, "E308", {"start": v(14.47, -0.03) * mm, "end": v(14.53, -0.03) * mm});
            skLineSegment(sketch, "E309", {"start": v(14.53, -0.03) * mm, "end": v(14.58, -0.03) * mm});
            skLineSegment(sketch, "E310", {"start": v(14.58, -0.03) * mm, "end": v(14.64, -0.03) * mm});
            skLineSegment(sketch, "E311", {"start": v(14.64, -0.03) * mm, "end": v(14.7, -0.03) * mm});
            skLineSegment(sketch, "E312", {"start": v(14.7, -0.03) * mm, "end": v(14.75, -0.03) * mm});
            skLineSegment(sketch, "E313", {"start": v(14.75, -0.03) * mm, "end": v(14.8, -0.03) * mm});
            skLineSegment(sketch, "E314", {"start": v(14.8, -0.03) * mm, "end": v(14.86, -0.03) * mm});
            skLineSegment(sketch, "E315", {"start": v(14.86, -0.03) * mm, "end": v(14.92, -0.03) * mm});
            skLineSegment(sketch, "E316", {"start": v(14.92, -0.03) * mm, "end": v(14.97, -0.03) * mm});
            skLineSegment(sketch, "E317", {"start": v(14.97, -0.03) * mm, "end": v(15.03, -0.03) * mm});
            skLineSegment(sketch, "E318", {"start": v(15.03, -0.03) * mm, "end": v(15.08, -0.03) * mm});
            skLineSegment(sketch, "E319", {"start": v(15.08, -0.03) * mm, "end": v(15.14, -0.03) * mm});
            skLineSegment(sketch, "E320", {"start": v(15.14, -0.03) * mm, "end": v(15.2, -0.03) * mm});
            skLineSegment(sketch, "E321", {"start": v(15.2, -0.03) * mm, "end": v(15.25, -0.03) * mm});
            skLineSegment(sketch, "E322", {"start": v(15.25, -0.03) * mm, "end": v(15.3, -0.03) * mm});
            skLineSegment(sketch, "E323", {"start": v(15.3, -0.03) * mm, "end": v(15.36, -0.03) * mm});
            skLineSegment(sketch, "E324", {"start": v(15.36, -0.03) * mm, "end": v(15.42, -0.03) * mm});
            skLineSegment(sketch, "E325", {"start": v(15.42, -0.03) * mm, "end": v(15.47, -0.03) * mm});
            skLineSegment(sketch, "E326", {"start": v(15.47, -0.03) * mm, "end": v(15.53, -0.03) * mm});
            skLineSegment(sketch, "E327", {"start": v(15.53, -0.03) * mm, "end": v(15.58, -0.03) * mm});
            skLineSegment(sketch, "E328", {"start": v(15.58, -0.03) * mm, "end": v(15.64, -0.03) * mm});
            skLineSegment(sketch, "E329", {"start": v(15.64, -0.03) * mm, "end": v(15.7, -0.03) * mm});
            skLineSegment(sketch, "E330", {"start": v(15.7, -0.03) * mm, "end": v(15.75, -0.03) * mm});
            skLineSegment(sketch, "E331", {"start": v(15.75, -0.03) * mm, "end": v(15.8, -0.03) * mm});
            skLineSegment(sketch, "E332", {"start": v(15.8, -0.03) * mm, "end": v(15.86, -0.03) * mm});
            skLineSegment(sketch, "E333", {"start": v(15.86, -0.03) * mm, "end": v(15.91, -0.03) * mm});
            skLineSegment(sketch, "E334", {"start": v(15.91, -0.03) * mm, "end": v(15.97, -0.03) * mm});
            skLineSegment(sketch, "E335", {"start": v(15.97, -0.03) * mm, "end": v(16.03, -0.03) * mm});
            skLineSegment(sketch, "E336", {"start": v(16.03, -0.03) * mm, "end": v(16.08, -0.03) * mm});
            skLineSegment(sketch, "E337", {"start": v(16.08, -0.03) * mm, "end": v(16.14, -0.03) * mm});
            skLineSegment(sketch, "E338", {"start": v(16.14, -0.03) * mm, "end": v(16.2, -0.03) * mm});
            skLineSegment(sketch, "E339", {"start": v(16.2, -0.03) * mm, "end": v(16.25, -0.03) * mm});
            skLineSegment(sketch, "E340", {"start": v(16.25, -0.03) * mm, "end": v(16.3, -0.03) * mm});
            skLineSegment(sketch, "E341", {"start": v(16.3, -0.03) * mm, "end": v(16.36, -0.03) * mm});
            skLineSegment(sketch, "E342", {"start": v(16.36, -0.03) * mm, "end": v(16.41, -0.03) * mm});
            skLineSegment(sketch, "E343", {"start": v(16.41, -0.03) * mm, "end": v(16.47, -0.03) * mm});
            skLineSegment(sketch, "E344", {"start": v(16.47, -0.03) * mm, "end": v(16.52, -0.03) * mm});
            skLineSegment(sketch, "E345", {"start": v(16.52, -0.03) * mm, "end": v(16.58, -0.03) * mm});
            skLineSegment(sketch, "E346", {"start": v(16.58, -0.03) * mm, "end": v(16.64, -0.03) * mm});
            skLineSegment(sketch, "E347", {"start": v(16.64, -0.03) * mm, "end": v(16.7, -0.03) * mm});
            skLineSegment(sketch, "E348", {"start": v(16.7, -0.03) * mm, "end": v(17.02, -0.03) * mm});
            skLineSegment(sketch, "E349", {"start": v(17.02, -0.03) * mm, "end": v(17.25, 0.14) * mm});
            skLineSegment(sketch, "E350", {"start": v(17.25, 0.14) * mm, "end": v(17.36, 0.3) * mm});
            skLineSegment(sketch, "E351", {"start": v(17.36, 0.3) * mm, "end": v(17.36, 0.53) * mm});
            skLineSegment(sketch, "E352", {"start": v(17.36, 0.53) * mm, "end": v(17.36, 0.58) * mm});
            skLineSegment(sketch, "E353", {"start": v(17.36, 0.58) * mm, "end": v(17.36, 0.64) * mm});
            skLineSegment(sketch, "E354", {"start": v(17.36, 0.64) * mm, "end": v(17.36, 0.7) * mm});
            skLineSegment(sketch, "E355", {"start": v(17.36, 0.7) * mm, "end": v(17.36, 0.75) * mm});
            skLineSegment(sketch, "E356", {"start": v(17.36, 0.75) * mm, "end": v(17.36, 0.8) * mm});
            skLineSegment(sketch, "E357", {"start": v(17.36, 0.8) * mm, "end": v(17.36, 0.86) * mm});
            skLineSegment(sketch, "E358", {"start": v(17.36, 0.86) * mm, "end": v(17.36, 0.91) * mm});
            skLineSegment(sketch, "E359", {"start": v(17.36, 0.91) * mm, "end": v(17.36, 1.3) * mm});
            skLineSegment(sketch, "E360", {"start": v(17.36, 1.3) * mm, "end": v(17.3, 1.3) * mm});
            skLineSegment(sketch, "E361", {"start": v(17.3, 1.3) * mm, "end": v(17.3, 1.47) * mm});
            skLineSegment(sketch, "E362", {"start": v(17.3, 1.47) * mm, "end": v(17.3, 1.91) * mm});
            skLineSegment(sketch, "E363", {"start": v(17.3, 1.91) * mm, "end": v(17.25, 1.91) * mm});
            skLineSegment(sketch, "E364", {"start": v(17.25, 1.91) * mm, "end": v(17.25, 2.25) * mm});
            skLineSegment(sketch, "E365", {"start": v(17.25, 2.25) * mm, "end": v(17.2, 2.25) * mm});
            skLineSegment(sketch, "E366", {"start": v(17.2, 2.25) * mm, "end": v(17.2, 2.69) * mm});
            skLineSegment(sketch, "E367", {"start": v(17.2, 2.69) * mm, "end": v(17.13, 2.69) * mm});
            skLineSegment(sketch, "E368", {"start": v(17.13, 2.69) * mm, "end": v(17.13, 2.97) * mm});
            skLineSegment(sketch, "E369", {"start": v(17.13, 2.97) * mm, "end": v(17.08, 2.97) * mm});
            skLineSegment(sketch, "E370", {"start": v(17.08, 2.97) * mm, "end": v(17.08, 3.3) * mm});
            skLineSegment(sketch, "E371", {"start": v(17.08, 3.3) * mm, "end": v(17.02, 3.3) * mm});
            skLineSegment(sketch, "E372", {"start": v(17.02, 3.3) * mm, "end": v(17.02, 3.63) * mm});
            skLineSegment(sketch, "E373", {"start": v(17.02, 3.63) * mm, "end": v(16.97, 3.63) * mm});
            skLineSegment(sketch, "E374", {"start": v(16.97, 3.63) * mm, "end": v(16.97, 3.85) * mm});
            skLineSegment(sketch, "E375", {"start": v(16.97, 3.85) * mm, "end": v(16.91, 3.85) * mm});
            skLineSegment(sketch, "E376", {"start": v(16.91, 3.85) * mm, "end": v(16.91, 4.08) * mm});
            skLineSegment(sketch, "E377", {"start": v(16.91, 4.08) * mm, "end": v(16.86, 4.08) * mm});
            skLineSegment(sketch, "E378", {"start": v(16.86, 4.08) * mm, "end": v(16.86, 4.3) * mm});
            skLineSegment(sketch, "E379", {"start": v(16.86, 4.3) * mm, "end": v(16.75, 4.46) * mm});
            skLineSegment(sketch, "E380", {"start": v(16.75, 4.46) * mm, "end": v(16.75, 4.74) * mm});
            skLineSegment(sketch, "E381", {"start": v(16.75, 4.74) * mm, "end": v(16.7, 4.9) * mm});
            skLineSegment(sketch, "E382", {"start": v(16.7, 4.9) * mm, "end": v(16.64, 4.9) * mm});
            skLineSegment(sketch, "E383", {"start": v(16.64, 4.9) * mm, "end": v(16.64, 5.07) * mm});
            skLineSegment(sketch, "E384", {"start": v(16.64, 5.07) * mm, "end": v(16.58, 5.07) * mm});
            skLineSegment(sketch, "E385", {"start": v(16.58, 5.07) * mm, "end": v(16.58, 5.24) * mm});
            skLineSegment(sketch, "E386", {"start": v(16.58, 5.24) * mm, "end": v(16.52, 5.24) * mm});
            skLineSegment(sketch, "E387", {"start": v(16.52, 5.24) * mm, "end": v(16.47, 5.4) * mm});
            skLineSegment(sketch, "E388", {"start": v(16.47, 5.4) * mm, "end": v(16.47, 5.63) * mm});
            skLineSegment(sketch, "E389", {"start": v(16.47, 5.63) * mm, "end": v(16.41, 5.8) * mm});
            skLineSegment(sketch, "E390", {"start": v(16.41, 5.8) * mm, "end": v(16.36, 5.8) * mm});
            skLineSegment(sketch, "E391", {"start": v(16.36, 5.8) * mm, "end": v(16.36, 5.96) * mm});
            skLineSegment(sketch, "E392", {"start": v(16.36, 5.96) * mm, "end": v(16.2, 6.18) * mm});
            skLineSegment(sketch, "E393", {"start": v(16.2, 6.18) * mm, "end": v(16.14, 6.52) * mm});
            skLineSegment(sketch, "E394", {"start": v(16.14, 6.52) * mm, "end": v(16.03, 6.63) * mm});
            skLineSegment(sketch, "E395", {"start": v(16.03, 6.63) * mm, "end": v(16.03, 6.8) * mm});
            skLineSegment(sketch, "E396", {"start": v(16.03, 6.8) * mm, "end": v(15.97, 6.9) * mm});
            skLineSegment(sketch, "E397", {"start": v(15.97, 6.9) * mm, "end": v(15.91, 6.9) * mm});
            skLineSegment(sketch, "E398", {"start": v(15.91, 6.9) * mm, "end": v(15.91, 7.01) * mm});
            skLineSegment(sketch, "E399", {"start": v(15.91, 7.01) * mm, "end": v(15.86, 7.01) * mm});
            skLineSegment(sketch, "E400", {"start": v(15.86, 7.01) * mm, "end": v(15.86, 7.13) * mm});
            skLineSegment(sketch, "E401", {"start": v(15.86, 7.13) * mm, "end": v(15.8, 7.13) * mm});
            skLineSegment(sketch, "E402", {"start": v(15.8, 7.13) * mm, "end": v(15.8, 7.24) * mm});
            skLineSegment(sketch, "E403", {"start": v(15.8, 7.24) * mm, "end": v(15.75, 7.24) * mm});
            skLineSegment(sketch, "E404", {"start": v(15.75, 7.24) * mm, "end": v(15.7, 7.51) * mm});
            skLineSegment(sketch, "E405", {"start": v(15.7, 7.51) * mm, "end": v(15.58, 7.57) * mm});
            skLineSegment(sketch, "E406", {"start": v(15.58, 7.57) * mm, "end": v(15.58, 7.74) * mm});
            skLineSegment(sketch, "E407", {"start": v(15.58, 7.74) * mm, "end": v(15.47, 7.85) * mm});
            skLineSegment(sketch, "E408", {"start": v(15.47, 7.85) * mm, "end": v(15.47, 7.96) * mm});
            skLineSegment(sketch, "E409", {"start": v(15.47, 7.96) * mm, "end": v(15.42, 7.96) * mm});
            skLineSegment(sketch, "E410", {"start": v(15.42, 7.96) * mm, "end": v(15.36, 8.18) * mm});
            skLineSegment(sketch, "E411", {"start": v(15.36, 8.18) * mm, "end": v(15.25, 8.23) * mm});
            skLineSegment(sketch, "E412", {"start": v(15.25, 8.23) * mm, "end": v(15.25, 8.35) * mm});
            skLineSegment(sketch, "E413", {"start": v(15.25, 8.35) * mm, "end": v(15.2, 8.35) * mm});
            skLineSegment(sketch, "E414", {"start": v(15.2, 8.35) * mm, "end": v(15.2, 8.46) * mm});
            skLineSegment(sketch, "E415", {"start": v(15.2, 8.46) * mm, "end": v(15.14, 8.46) * mm});
            skLineSegment(sketch, "E416", {"start": v(15.14, 8.46) * mm, "end": v(15.14, 8.57) * mm});
            skLineSegment(sketch, "E417", {"start": v(15.14, 8.57) * mm, "end": v(15.08, 8.57) * mm});
            skLineSegment(sketch, "E418", {"start": v(15.08, 8.57) * mm, "end": v(15.08, 8.68) * mm});
            skLineSegment(sketch, "E419", {"start": v(15.08, 8.68) * mm, "end": v(14.97, 8.73) * mm});
            skLineSegment(sketch, "E420", {"start": v(14.97, 8.73) * mm, "end": v(14.92, 8.96) * mm});
            skLineSegment(sketch, "E421", {"start": v(14.92, 8.96) * mm, "end": v(14.75, 9.07) * mm});
            skLineSegment(sketch, "E422", {"start": v(14.75, 9.07) * mm, "end": v(14.7, 9.29) * mm});
            skLineSegment(sketch, "E423", {"start": v(14.7, 9.29) * mm, "end": v(14.58, 9.34) * mm});
            skLineSegment(sketch, "E424", {"start": v(14.58, 9.34) * mm, "end": v(14.53, 9.57) * mm});
            skLineSegment(sketch, "E425", {"start": v(14.53, 9.57) * mm, "end": v(14.36, 9.68) * mm});
            skLineSegment(sketch, "E426", {"start": v(14.36, 9.68) * mm, "end": v(14.3, 9.9) * mm});
            skLineSegment(sketch, "E427", {"start": v(14.3, 9.9) * mm, "end": v(14.08, 10.06) * mm});
            skLineSegment(sketch, "E428", {"start": v(14.08, 10.06) * mm, "end": v(14.08, 10.18) * mm});
            skLineSegment(sketch, "E429", {"start": v(14.08, 10.18) * mm, "end": v(13.97, 10.23) * mm});
            skLineSegment(sketch, "E430", {"start": v(13.97, 10.23) * mm, "end": v(13.97, 10.34) * mm});
            skLineSegment(sketch, "E431", {"start": v(13.97, 10.34) * mm, "end": v(13.86, 10.4) * mm});
            skLineSegment(sketch, "E432", {"start": v(13.86, 10.4) * mm, "end": v(13.86, 10.5) * mm});
            skLineSegment(sketch, "E433", {"start": v(13.86, 10.5) * mm, "end": v(13.7, 10.62) * mm});
            skLineSegment(sketch, "E434", {"start": v(13.7, 10.62) * mm, "end": v(13.7, 10.73) * mm});
            skLineSegment(sketch, "E435", {"start": v(13.7, 10.73) * mm, "end": v(13.64, 10.79) * mm});
            skLineSegment(sketch, "E436", {"start": v(13.64, 10.79) * mm, "end": v(13.42, 10.95) * mm});
            skLineSegment(sketch, "E437", {"start": v(13.42, 10.95) * mm, "end": v(13.42, 11.06) * mm});
            skLineSegment(sketch, "E438", {"start": v(13.42, 11.06) * mm, "end": v(13.36, 11.12) * mm});
            skLineSegment(sketch, "E439", {"start": v(13.36, 11.12) * mm, "end": v(13.09, 11.34) * mm});
            skLineSegment(sketch, "E440", {"start": v(13.09, 11.34) * mm, "end": v(13.09, 11.45) * mm});
            skLineSegment(sketch, "E441", {"start": v(13.09, 11.45) * mm, "end": v(13.03, 11.5) * mm});
            skLineSegment(sketch, "E442", {"start": v(13.03, 11.5) * mm, "end": v(12.92, 11.62) * mm});
            skLineSegment(sketch, "E443", {"start": v(12.92, 11.62) * mm, "end": v(12.87, 11.62) * mm});
            skLineSegment(sketch, "E444", {"start": v(12.87, 11.62) * mm, "end": v(12.87, 11.67) * mm});
            skLineSegment(sketch, "E445", {"start": v(12.87, 11.67) * mm, "end": v(12.8, 11.67) * mm});
            skLineSegment(sketch, "E446", {"start": v(12.8, 11.67) * mm, "end": v(12.8, 11.73) * mm});
            skLineSegment(sketch, "E447", {"start": v(12.8, 11.73) * mm, "end": v(12.75, 11.73) * mm});
            skLineSegment(sketch, "E448", {"start": v(12.75, 11.73) * mm, "end": v(12.75, 11.78) * mm});
            skLineSegment(sketch, "E449", {"start": v(12.75, 11.78) * mm, "end": v(12.7, 11.78) * mm});
            skLineSegment(sketch, "E450", {"start": v(12.7, 11.78) * mm, "end": v(12.53, 12.06) * mm});
            skLineSegment(sketch, "E451", {"start": v(12.53, 12.06) * mm, "end": v(12.37, 12.12) * mm});
            skLineSegment(sketch, "E452", {"start": v(12.37, 12.12) * mm, "end": v(12.37, 12.23) * mm});
            skLineSegment(sketch, "E453", {"start": v(12.37, 12.23) * mm, "end": v(12.26, 12.23) * mm});
            skLineSegment(sketch, "E454", {"start": v(12.26, 12.23) * mm, "end": v(12.2, 12.28) * mm});
            skLineSegment(sketch, "E455", {"start": v(12.2, 12.28) * mm, "end": v(12.2, 12.4) * mm});
            skLineSegment(sketch, "E456", {"start": v(12.2, 12.4) * mm, "end": v(12.03, 12.45) * mm});
            skLineSegment(sketch, "E457", {"start": v(12.03, 12.45) * mm, "end": v(11.92, 12.56) * mm});
            skLineSegment(sketch, "E458", {"start": v(11.92, 12.56) * mm, "end": v(11.92, 12.62) * mm});
            skLineSegment(sketch, "E459", {"start": v(11.92, 12.62) * mm, "end": v(11.87, 12.62) * mm});
            skLineSegment(sketch, "E460", {"start": v(11.87, 12.62) * mm, "end": v(11.87, 12.67) * mm});
            skLineSegment(sketch, "E461", {"start": v(11.87, 12.67) * mm, "end": v(11.81, 12.67) * mm});
            skLineSegment(sketch, "E462", {"start": v(11.81, 12.67) * mm, "end": v(11.81, 12.73) * mm});
            skLineSegment(sketch, "E463", {"start": v(11.81, 12.73) * mm, "end": v(11.76, 12.73) * mm});
            skLineSegment(sketch, "E464", {"start": v(11.76, 12.73) * mm, "end": v(11.76, 12.78) * mm});
            skLineSegment(sketch, "E465", {"start": v(11.76, 12.78) * mm, "end": v(11.7, 12.78) * mm});
            skLineSegment(sketch, "E466", {"start": v(11.7, 12.78) * mm, "end": v(11.7, 12.84) * mm});
            skLineSegment(sketch, "E467", {"start": v(11.7, 12.84) * mm, "end": v(11.65, 12.84) * mm});
            skLineSegment(sketch, "E468", {"start": v(11.65, 12.84) * mm, "end": v(11.65, 12.9) * mm});
            skLineSegment(sketch, "E469", {"start": v(11.65, 12.9) * mm, "end": v(11.53, 13) * mm});
            skLineSegment(sketch, "E470", {"start": v(11.53, 13) * mm, "end": v(11.42, 13) * mm});
            skLineSegment(sketch, "E471", {"start": v(11.42, 13) * mm, "end": v(11.37, 13.06) * mm});
            skLineSegment(sketch, "E472", {"start": v(11.37, 13.06) * mm, "end": v(11.26, 13.17) * mm});
            skLineSegment(sketch, "E473", {"start": v(11.26, 13.17) * mm, "end": v(11.26, 13.23) * mm});
            skLineSegment(sketch, "E474", {"start": v(11.26, 13.23) * mm, "end": v(11.2, 13.23) * mm});
            skLineSegment(sketch, "E475", {"start": v(11.2, 13.23) * mm, "end": v(11.2, 13.28) * mm});
            skLineSegment(sketch, "E476", {"start": v(11.2, 13.28) * mm, "end": v(11.1, 13.4) * mm});
            skLineSegment(sketch, "E477", {"start": v(11.1, 13.4) * mm, "end": v(10.98, 13.4) * mm});
            skLineSegment(sketch, "E478", {"start": v(10.98, 13.4) * mm, "end": v(10.92, 13.45) * mm});
            skLineSegment(sketch, "E479", {"start": v(10.92, 13.45) * mm, "end": v(10.87, 13.56) * mm});
            skLineSegment(sketch, "E480", {"start": v(10.87, 13.56) * mm, "end": v(10.81, 13.61) * mm});
            skLineSegment(sketch, "E481", {"start": v(10.81, 13.61) * mm, "end": v(10.7, 13.61) * mm});
            skLineSegment(sketch, "E482", {"start": v(10.7, 13.61) * mm, "end": v(10.65, 13.67) * mm});
            skLineSegment(sketch, "E483", {"start": v(10.65, 13.67) * mm, "end": v(10.6, 13.78) * mm});
            skLineSegment(sketch, "E484", {"start": v(10.6, 13.78) * mm, "end": v(10.54, 13.84) * mm});
            skLineSegment(sketch, "E485", {"start": v(10.54, 13.84) * mm, "end": v(10.43, 13.84) * mm});
            skLineSegment(sketch, "E486", {"start": v(10.43, 13.84) * mm, "end": v(10.37, 13.95) * mm});
            skLineSegment(sketch, "E487", {"start": v(10.37, 13.95) * mm, "end": v(10.26, 13.95) * mm});
            skLineSegment(sketch, "E488", {"start": v(10.26, 13.95) * mm, "end": v(10.2, 14.06) * mm});
            skLineSegment(sketch, "E489", {"start": v(10.2, 14.06) * mm, "end": v(10.1, 14.06) * mm});
            skLineSegment(sketch, "E490", {"start": v(10.1, 14.06) * mm, "end": v(9.98, 14.22) * mm});
            skLineSegment(sketch, "E491", {"start": v(9.98, 14.22) * mm, "end": v(9.87, 14.22) * mm});
            skLineSegment(sketch, "E492", {"start": v(9.87, 14.22) * mm, "end": v(9.76, 14.4) * mm});
            skLineSegment(sketch, "E493", {"start": v(9.76, 14.4) * mm, "end": v(9.65, 14.4) * mm});
            skLineSegment(sketch, "E494", {"start": v(9.65, 14.4) * mm, "end": v(9.6, 14.5) * mm});
            skLineSegment(sketch, "E495", {"start": v(9.6, 14.5) * mm, "end": v(9.37, 14.56) * mm});
            skLineSegment(sketch, "E496", {"start": v(9.37, 14.56) * mm, "end": v(9.32, 14.67) * mm});
            skLineSegment(sketch, "E497", {"start": v(9.32, 14.67) * mm, "end": v(9.15, 14.78) * mm});
            skLineSegment(sketch, "E498", {"start": v(9.15, 14.78) * mm, "end": v(8.93, 14.83) * mm});
            skLineSegment(sketch, "E499", {"start": v(-9.2, 14.72) * mm, "end": v(-9.37, 14.56) * mm});
            skLineSegment(sketch, "E500", {"start": v(-9.37, 14.56) * mm, "end": v(-9.6, 14.5) * mm});
            skLineSegment(sketch, "E501", {"start": v(-9.6, 14.5) * mm, "end": v(-9.65, 14.4) * mm});
            skLineSegment(sketch, "E502", {"start": v(-9.65, 14.4) * mm, "end": v(-9.76, 14.4) * mm});
            skLineSegment(sketch, "E503", {"start": v(-9.76, 14.4) * mm, "end": v(-9.87, 14.22) * mm});
            skLineSegment(sketch, "E504", {"start": v(-9.87, 14.22) * mm, "end": v(-10.1, 14.17) * mm});
            skLineSegment(sketch, "E505", {"start": v(-10.1, 14.17) * mm, "end": v(-10.26, 13.95) * mm});
            skLineSegment(sketch, "E506", {"start": v(-10.26, 13.95) * mm, "end": v(-10.37, 13.95) * mm});
            skLineSegment(sketch, "E507", {"start": v(-10.37, 13.95) * mm, "end": v(-10.43, 13.84) * mm});
            skLineSegment(sketch, "E508", {"start": v(-10.43, 13.84) * mm, "end": v(-10.54, 13.84) * mm});
            skLineSegment(sketch, "E509", {"start": v(-10.54, 13.84) * mm, "end": v(-10.6, 13.78) * mm});
            skLineSegment(sketch, "E510", {"start": v(-10.6, 13.78) * mm, "end": v(-10.65, 13.67) * mm});
            skLineSegment(sketch, "E511", {"start": v(-10.65, 13.67) * mm, "end": v(-10.7, 13.61) * mm});
            skLineSegment(sketch, "E512", {"start": v(-10.7, 13.61) * mm, "end": v(-10.81, 13.61) * mm});
            skLineSegment(sketch, "E513", {"start": v(-10.81, 13.61) * mm, "end": v(-10.92, 13.45) * mm});
            skLineSegment(sketch, "E514", {"start": v(-10.92, 13.45) * mm, "end": v(-11.04, 13.45) * mm});
            skLineSegment(sketch, "E515", {"start": v(-11.04, 13.45) * mm, "end": v(-11.1, 13.4) * mm});
            skLineSegment(sketch, "E516", {"start": v(-11.1, 13.4) * mm, "end": v(-11.2, 13.28) * mm});
            skLineSegment(sketch, "E517", {"start": v(-11.2, 13.28) * mm, "end": v(-11.2, 13.23) * mm});
            skLineSegment(sketch, "E518", {"start": v(-11.2, 13.23) * mm, "end": v(-11.26, 13.23) * mm});
            skLineSegment(sketch, "E519", {"start": v(-11.26, 13.23) * mm, "end": v(-11.26, 13.17) * mm});
            skLineSegment(sketch, "E520", {"start": v(-11.26, 13.17) * mm, "end": v(-11.37, 13.06) * mm});
            skLineSegment(sketch, "E521", {"start": v(-11.37, 13.06) * mm, "end": v(-11.48, 13.06) * mm});
            skLineSegment(sketch, "E522", {"start": v(-11.48, 13.06) * mm, "end": v(-11.53, 13) * mm});
            skLineSegment(sketch, "E523", {"start": v(-11.53, 13) * mm, "end": v(-11.65, 12.9) * mm});
            skLineSegment(sketch, "E524", {"start": v(-11.65, 12.9) * mm, "end": v(-11.65, 12.84) * mm});
            skLineSegment(sketch, "E525", {"start": v(-11.65, 12.84) * mm, "end": v(-11.7, 12.84) * mm});
            skLineSegment(sketch, "E526", {"start": v(-11.7, 12.84) * mm, "end": v(-11.7, 12.78) * mm});
            skLineSegment(sketch, "E527", {"start": v(-11.7, 12.78) * mm, "end": v(-11.76, 12.78) * mm});
            skLineSegment(sketch, "E528", {"start": v(-11.76, 12.78) * mm, "end": v(-11.76, 12.73) * mm});
            skLineSegment(sketch, "E529", {"start": v(-11.76, 12.73) * mm, "end": v(-11.81, 12.73) * mm});
            skLineSegment(sketch, "E530", {"start": v(-11.81, 12.73) * mm, "end": v(-11.81, 12.67) * mm});
            skLineSegment(sketch, "E531", {"start": v(-11.81, 12.67) * mm, "end": v(-11.87, 12.67) * mm});
            skLineSegment(sketch, "E532", {"start": v(-11.87, 12.67) * mm, "end": v(-11.87, 12.62) * mm});
            skLineSegment(sketch, "E533", {"start": v(-11.87, 12.62) * mm, "end": v(-11.92, 12.62) * mm});
            skLineSegment(sketch, "E534", {"start": v(-11.92, 12.62) * mm, "end": v(-11.92, 12.56) * mm});
            skLineSegment(sketch, "E535", {"start": v(-11.92, 12.56) * mm, "end": v(-12.03, 12.45) * mm});
            skLineSegment(sketch, "E536", {"start": v(-12.03, 12.45) * mm, "end": v(-12.09, 12.4) * mm});
            skLineSegment(sketch, "E537", {"start": v(-12.09, 12.4) * mm, "end": v(-12.2, 12.4) * mm});
            skLineSegment(sketch, "E538", {"start": v(-12.2, 12.4) * mm, "end": v(-12.26, 12.23) * mm});
            skLineSegment(sketch, "E539", {"start": v(-12.26, 12.23) * mm, "end": v(-12.31, 12.17) * mm});
            skLineSegment(sketch, "E540", {"start": v(-12.31, 12.17) * mm, "end": v(-12.48, 12.12) * mm});
            skLineSegment(sketch, "E541", {"start": v(-12.48, 12.12) * mm, "end": v(-12.53, 12.06) * mm});
            skLineSegment(sketch, "E542", {"start": v(-12.53, 12.06) * mm, "end": v(-12.53, 11.95) * mm});
            skLineSegment(sketch, "E543", {"start": v(-12.53, 11.95) * mm, "end": v(-12.64, 11.84) * mm});
            skLineSegment(sketch, "E544", {"start": v(-12.64, 11.84) * mm, "end": v(-12.7, 11.84) * mm});
            skLineSegment(sketch, "E545", {"start": v(-12.7, 11.84) * mm, "end": v(-12.7, 11.78) * mm});
            skLineSegment(sketch, "E546", {"start": v(-12.7, 11.78) * mm, "end": v(-12.75, 11.78) * mm});
            skLineSegment(sketch, "E547", {"start": v(-12.75, 11.78) * mm, "end": v(-12.75, 11.73) * mm});
            skLineSegment(sketch, "E548", {"start": v(-12.75, 11.73) * mm, "end": v(-12.8, 11.73) * mm});
            skLineSegment(sketch, "E549", {"start": v(-12.8, 11.73) * mm, "end": v(-12.8, 11.67) * mm});
            skLineSegment(sketch, "E550", {"start": v(-12.8, 11.67) * mm, "end": v(-12.87, 11.67) * mm});
            skLineSegment(sketch, "E551", {"start": v(-12.87, 11.67) * mm, "end": v(-12.87, 11.62) * mm});
            skLineSegment(sketch, "E552", {"start": v(-12.87, 11.62) * mm, "end": v(-12.92, 11.62) * mm});
            skLineSegment(sketch, "E553", {"start": v(-12.92, 11.62) * mm, "end": v(-12.92, 11.56) * mm});
            skLineSegment(sketch, "E554", {"start": v(-12.92, 11.56) * mm, "end": v(-12.98, 11.56) * mm});
            skLineSegment(sketch, "E555", {"start": v(-12.98, 11.56) * mm, "end": v(-13.09, 11.45) * mm});
            skLineSegment(sketch, "E556", {"start": v(-13.09, 11.45) * mm, "end": v(-13.09, 11.34) * mm});
            skLineSegment(sketch, "E557", {"start": v(-13.09, 11.34) * mm, "end": v(-13.14, 11.28) * mm});
            skLineSegment(sketch, "E558", {"start": v(-13.14, 11.28) * mm, "end": v(-13.42, 11.06) * mm});
            skLineSegment(sketch, "E559", {"start": v(-13.42, 11.06) * mm, "end": v(-13.42, 10.95) * mm});
            skLineSegment(sketch, "E560", {"start": v(-13.42, 10.95) * mm, "end": v(-13.48, 10.9) * mm});
            skLineSegment(sketch, "E561", {"start": v(-13.48, 10.9) * mm, "end": v(-13.7, 10.73) * mm});
            skLineSegment(sketch, "E562", {"start": v(-13.7, 10.73) * mm, "end": v(-13.7, 10.62) * mm});
            skLineSegment(sketch, "E563", {"start": v(-13.7, 10.62) * mm, "end": v(-13.75, 10.56) * mm});
            skLineSegment(sketch, "E564", {"start": v(-13.75, 10.56) * mm, "end": v(-13.86, 10.5) * mm});
            skLineSegment(sketch, "E565", {"start": v(-13.86, 10.5) * mm, "end": v(-13.92, 10.45) * mm});
            skLineSegment(sketch, "E566", {"start": v(-13.92, 10.45) * mm, "end": v(-13.92, 10.34) * mm});
            skLineSegment(sketch, "E567", {"start": v(-13.92, 10.34) * mm, "end": v(-14.03, 10.29) * mm});
            skLineSegment(sketch, "E568", {"start": v(-14.03, 10.29) * mm, "end": v(-14.09, 10.06) * mm});
            skLineSegment(sketch, "E569", {"start": v(-14.09, 10.06) * mm, "end": v(-14.3, 9.9) * mm});
            skLineSegment(sketch, "E570", {"start": v(-14.3, 9.9) * mm, "end": v(-14.3, 9.79) * mm});
            skLineSegment(sketch, "E571", {"start": v(-14.3, 9.79) * mm, "end": v(-14.42, 9.73) * mm});
            skLineSegment(sketch, "E572", {"start": v(-14.42, 9.73) * mm, "end": v(-14.42, 9.62) * mm});
            skLineSegment(sketch, "E573", {"start": v(-14.42, 9.62) * mm, "end": v(-14.53, 9.57) * mm});
            skLineSegment(sketch, "E574", {"start": v(-14.53, 9.57) * mm, "end": v(-14.58, 9.34) * mm});
            skLineSegment(sketch, "E575", {"start": v(-14.58, 9.34) * mm, "end": v(-14.7, 9.29) * mm});
            skLineSegment(sketch, "E576", {"start": v(-14.7, 9.29) * mm, "end": v(-14.7, 9.18) * mm});
            skLineSegment(sketch, "E577", {"start": v(-14.7, 9.18) * mm, "end": v(-14.8, 9.12) * mm});
            skLineSegment(sketch, "E578", {"start": v(-14.8, 9.12) * mm, "end": v(-14.8, 9.01) * mm});
            skLineSegment(sketch, "E579", {"start": v(-14.8, 9.01) * mm, "end": v(-14.92, 8.96) * mm});
            skLineSegment(sketch, "E580", {"start": v(-14.92, 8.96) * mm, "end": v(-14.97, 8.73) * mm});
            skLineSegment(sketch, "E581", {"start": v(-14.97, 8.73) * mm, "end": v(-15.08, 8.68) * mm});
            skLineSegment(sketch, "E582", {"start": v(-15.08, 8.68) * mm, "end": v(-15.08, 8.57) * mm});
            skLineSegment(sketch, "E583", {"start": v(-15.08, 8.57) * mm, "end": v(-15.14, 8.57) * mm});
            skLineSegment(sketch, "E584", {"start": v(-15.14, 8.57) * mm, "end": v(-15.14, 8.46) * mm});
            skLineSegment(sketch, "E585", {"start": v(-15.14, 8.46) * mm, "end": v(-15.2, 8.46) * mm});
            skLineSegment(sketch, "E586", {"start": v(-15.2, 8.46) * mm, "end": v(-15.2, 8.35) * mm});
            skLineSegment(sketch, "E587", {"start": v(-15.2, 8.35) * mm, "end": v(-15.25, 8.35) * mm});
            skLineSegment(sketch, "E588", {"start": v(-15.25, 8.35) * mm, "end": v(-15.25, 8.23) * mm});
            skLineSegment(sketch, "E589", {"start": v(-15.25, 8.23) * mm, "end": v(-15.36, 8.18) * mm});
            skLineSegment(sketch, "E590", {"start": v(-15.36, 8.18) * mm, "end": v(-15.36, 8.07) * mm});
            skLineSegment(sketch, "E591", {"start": v(-15.36, 8.07) * mm, "end": v(-15.42, 8.07) * mm});
            skLineSegment(sketch, "E592", {"start": v(-15.42, 8.07) * mm, "end": v(-15.42, 7.96) * mm});
            skLineSegment(sketch, "E593", {"start": v(-15.42, 7.96) * mm, "end": v(-15.47, 7.96) * mm});
            skLineSegment(sketch, "E594", {"start": v(-15.47, 7.96) * mm, "end": v(-15.47, 7.85) * mm});
            skLineSegment(sketch, "E595", {"start": v(-15.47, 7.85) * mm, "end": v(-15.53, 7.85) * mm});
            skLineSegment(sketch, "E596", {"start": v(-15.53, 7.85) * mm, "end": v(-15.53, 7.74) * mm});
            skLineSegment(sketch, "E597", {"start": v(-15.53, 7.74) * mm, "end": v(-15.58, 7.74) * mm});
            skLineSegment(sketch, "E598", {"start": v(-15.58, 7.74) * mm, "end": v(-15.58, 7.62) * mm});
            skLineSegment(sketch, "E599", {"start": v(-15.58, 7.62) * mm, "end": v(-15.64, 7.62) * mm});
            skLineSegment(sketch, "E600", {"start": v(-15.64, 7.62) * mm, "end": v(-15.64, 7.51) * mm});
            skLineSegment(sketch, "E601", {"start": v(-15.64, 7.51) * mm, "end": v(-15.7, 7.51) * mm});
            skLineSegment(sketch, "E602", {"start": v(-15.7, 7.51) * mm, "end": v(-15.7, 7.4) * mm});
            skLineSegment(sketch, "E603", {"start": v(-15.7, 7.4) * mm, "end": v(-15.75, 7.4) * mm});
            skLineSegment(sketch, "E604", {"start": v(-15.75, 7.4) * mm, "end": v(-15.8, 7.3) * mm});
            skLineSegment(sketch, "E605", {"start": v(-15.8, 7.3) * mm, "end": v(-15.8, 7.13) * mm});
            skLineSegment(sketch, "E606", {"start": v(-15.8, 7.13) * mm, "end": v(-15.86, 7.01) * mm});
            skLineSegment(sketch, "E607", {"start": v(-15.86, 7.01) * mm, "end": v(-15.92, 7.01) * mm});
            skLineSegment(sketch, "E608", {"start": v(-15.92, 7.01) * mm, "end": v(-15.92, 6.9) * mm});
            skLineSegment(sketch, "E609", {"start": v(-15.92, 6.9) * mm, "end": v(-16.03, 6.8) * mm});
            skLineSegment(sketch, "E610", {"start": v(-16.03, 6.8) * mm, "end": v(-16.03, 6.63) * mm});
            skLineSegment(sketch, "E611", {"start": v(-16.03, 6.63) * mm, "end": v(-16.14, 6.52) * mm});
            skLineSegment(sketch, "E612", {"start": v(-16.14, 6.52) * mm, "end": v(-16.2, 6.18) * mm});
            skLineSegment(sketch, "E613", {"start": v(-16.2, 6.18) * mm, "end": v(-16.36, 5.96) * mm});
            skLineSegment(sketch, "E614", {"start": v(-16.36, 5.96) * mm, "end": v(-16.41, 5.8) * mm});
            skLineSegment(sketch, "E615", {"start": v(-16.41, 5.8) * mm, "end": v(-16.41, 5.63) * mm});
            skLineSegment(sketch, "E616", {"start": v(-16.41, 5.63) * mm, "end": v(-16.47, 5.63) * mm});
            skLineSegment(sketch, "E617", {"start": v(-16.47, 5.63) * mm, "end": v(-16.47, 5.4) * mm});
            skLineSegment(sketch, "E618", {"start": v(-16.47, 5.4) * mm, "end": v(-16.53, 5.24) * mm});
            skLineSegment(sketch, "E619", {"start": v(-16.53, 5.24) * mm, "end": v(-16.58, 5.24) * mm});
            skLineSegment(sketch, "E620", {"start": v(-16.58, 5.24) * mm, "end": v(-16.58, 5.07) * mm});
            skLineSegment(sketch, "E621", {"start": v(-16.58, 5.07) * mm, "end": v(-16.7, 4.96) * mm});
            skLineSegment(sketch, "E622", {"start": v(-16.7, 4.96) * mm, "end": v(-16.7, 4.74) * mm});
            skLineSegment(sketch, "E623", {"start": v(-16.7, 4.74) * mm, "end": v(-16.75, 4.74) * mm});
            skLineSegment(sketch, "E624", {"start": v(-16.75, 4.74) * mm, "end": v(-16.75, 4.52) * mm});
            skLineSegment(sketch, "E625", {"start": v(-16.75, 4.52) * mm, "end": v(-16.8, 4.52) * mm});
            skLineSegment(sketch, "E626", {"start": v(-16.8, 4.52) * mm, "end": v(-16.8, 4.24) * mm});
            skLineSegment(sketch, "E627", {"start": v(-16.8, 4.24) * mm, "end": v(-16.91, 4.08) * mm});
            skLineSegment(sketch, "E628", {"start": v(-16.91, 4.08) * mm, "end": v(-16.91, 3.85) * mm});
            skLineSegment(sketch, "E629", {"start": v(-16.91, 3.85) * mm, "end": v(-16.97, 3.85) * mm});
            skLineSegment(sketch, "E630", {"start": v(-16.97, 3.85) * mm, "end": v(-16.97, 3.63) * mm});
            skLineSegment(sketch, "E631", {"start": v(-16.97, 3.63) * mm, "end": v(-17.02, 3.63) * mm});
            skLineSegment(sketch, "E632", {"start": v(-17.02, 3.63) * mm, "end": v(-17.02, 3.3) * mm});
            skLineSegment(sketch, "E633", {"start": v(-17.02, 3.3) * mm, "end": v(-17.08, 3.3) * mm});
            skLineSegment(sketch, "E634", {"start": v(-17.08, 3.3) * mm, "end": v(-17.08, 2.97) * mm});
            skLineSegment(sketch, "E635", {"start": v(-17.08, 2.97) * mm, "end": v(-17.13, 2.97) * mm});
            skLineSegment(sketch, "E636", {"start": v(-17.13, 2.97) * mm, "end": v(-17.13, 2.69) * mm});
            skLineSegment(sketch, "E637", {"start": v(-17.13, 2.69) * mm, "end": v(-17.2, 2.69) * mm});
            skLineSegment(sketch, "E638", {"start": v(-17.2, 2.69) * mm, "end": v(-17.2, 2.52) * mm});
            skLineSegment(sketch, "E639", {"start": v(-17.2, 2.52) * mm, "end": v(-17.2, 2.36) * mm});
            skLineSegment(sketch, "E640", {"start": v(-17.2, 2.36) * mm, "end": v(-17.2, 2.2) * mm});
            skLineSegment(sketch, "E641", {"start": v(-17.2, 2.2) * mm, "end": v(-17.25, 2.2) * mm});
            skLineSegment(sketch, "E642", {"start": v(-17.25, 2.2) * mm, "end": v(-17.25, 1.91) * mm});
            skLineSegment(sketch, "E643", {"start": v(-17.25, 1.91) * mm, "end": v(-17.3, 1.91) * mm});
            skLineSegment(sketch, "E644", {"start": v(-17.3, 1.91) * mm, "end": v(-17.3, 1.75) * mm});
            skLineSegment(sketch, "E645", {"start": v(-17.3, 1.75) * mm, "end": v(-17.3, 1.3) * mm});
            skLineSegment(sketch, "E646", {"start": v(-17.3, 1.3) * mm, "end": v(-17.36, 1.3) * mm});
            skLineSegment(sketch, "E647", {"start": v(-17.36, 1.3) * mm, "end": v(-17.36, 1.14) * mm});
            skLineSegment(sketch, "E648", {"start": v(-17.36, 1.14) * mm, "end": v(-17.36, 0.91) * mm});
            skLineSegment(sketch, "E649", {"start": v(-17.36, 0.91) * mm, "end": v(-17.36, 0.86) * mm});
            skLineSegment(sketch, "E650", {"start": v(-17.36, 0.86) * mm, "end": v(-17.36, 0.8) * mm});
            skLineSegment(sketch, "E651", {"start": v(-17.36, 0.8) * mm, "end": v(-17.36, 0.75) * mm});
            skLineSegment(sketch, "E652", {"start": v(-17.36, 0.75) * mm, "end": v(-17.36, 0.7) * mm});
            skLineSegment(sketch, "E653", {"start": v(-17.36, 0.7) * mm, "end": v(-17.36, 0.64) * mm});
            skLineSegment(sketch, "E654", {"start": v(-17.36, 0.64) * mm, "end": v(-17.36, 0.58) * mm});
            skLineSegment(sketch, "E655", {"start": v(-17.36, 0.58) * mm, "end": v(-17.36, 0.53) * mm});
            skLineSegment(sketch, "E656", {"start": v(-17.36, 0.53) * mm, "end": v(-17.36, 0.3) * mm});
            skLineSegment(sketch, "E657", {"start": v(-17.36, 0.3) * mm, "end": v(-17.25, 0.14) * mm});
            skLineSegment(sketch, "E658", {"start": v(-17.25, 0.14) * mm, "end": v(-17.02, -0.03) * mm});
            skLineSegment(sketch, "E659", {"start": v(-17.02, -0.03) * mm, "end": v(-16.75, -0.08) * mm});
            skLineSegment(sketch, "E660", {"start": v(-16.75, -0.08) * mm, "end": v(-16.64, -0.08) * mm});
            skLineSegment(sketch, "E661", {"start": v(-16.64, -0.08) * mm, "end": v(-16.58, -0.03) * mm});
            skLineSegment(sketch, "E662", {"start": v(-16.58, -0.03) * mm, "end": v(-16.36, -0.03) * mm});
            skLineSegment(sketch, "E663", {"start": v(-16.36, -0.03) * mm, "end": v(-16.3, -0.03) * mm});
            skLineSegment(sketch, "E664", {"start": v(-16.3, -0.03) * mm, "end": v(-16.25, -0.03) * mm});
            skLineSegment(sketch, "E665", {"start": v(-16.25, -0.03) * mm, "end": v(-16.2, -0.03) * mm});
            skLineSegment(sketch, "E666", {"start": v(-16.2, -0.03) * mm, "end": v(-16.14, -0.03) * mm});
            skLineSegment(sketch, "E667", {"start": v(-16.14, -0.03) * mm, "end": v(-16.08, -0.03) * mm});
            skLineSegment(sketch, "E668", {"start": v(-16.08, -0.03) * mm, "end": v(-16.03, -0.03) * mm});
            skLineSegment(sketch, "E669", {"start": v(-16.03, -0.03) * mm, "end": v(-15.97, -0.03) * mm});
            skLineSegment(sketch, "E670", {"start": v(-15.97, -0.03) * mm, "end": v(-15.92, -0.03) * mm});
            skLineSegment(sketch, "E671", {"start": v(-15.92, -0.03) * mm, "end": v(-15.86, -0.03) * mm});
            skLineSegment(sketch, "E672", {"start": v(-15.86, -0.03) * mm, "end": v(-15.8, -0.03) * mm});
            skLineSegment(sketch, "E673", {"start": v(-15.8, -0.03) * mm, "end": v(-15.75, -0.03) * mm});
            skLineSegment(sketch, "E674", {"start": v(-15.75, -0.03) * mm, "end": v(-15.7, -0.03) * mm});
            skLineSegment(sketch, "E675", {"start": v(-15.7, -0.03) * mm, "end": v(-15.64, -0.03) * mm});
            skLineSegment(sketch, "E676", {"start": v(-15.64, -0.03) * mm, "end": v(-15.58, -0.03) * mm});
            skLineSegment(sketch, "E677", {"start": v(-15.58, -0.03) * mm, "end": v(-15.53, -0.03) * mm});
            skLineSegment(sketch, "E678", {"start": v(-15.53, -0.03) * mm, "end": v(-15.47, -0.03) * mm});
            skLineSegment(sketch, "E679", {"start": v(-15.47, -0.03) * mm, "end": v(-15.42, -0.03) * mm});
            skLineSegment(sketch, "E680", {"start": v(-15.42, -0.03) * mm, "end": v(-15.36, -0.03) * mm});
            skLineSegment(sketch, "E681", {"start": v(-15.36, -0.03) * mm, "end": v(-15.3, -0.03) * mm});
            skLineSegment(sketch, "E682", {"start": v(-15.3, -0.03) * mm, "end": v(-15.25, -0.03) * mm});
            skLineSegment(sketch, "E683", {"start": v(-15.25, -0.03) * mm, "end": v(-15.2, -0.03) * mm});
            skLineSegment(sketch, "E684", {"start": v(-15.2, -0.03) * mm, "end": v(-15.14, -0.03) * mm});
            skLineSegment(sketch, "E685", {"start": v(-15.14, -0.03) * mm, "end": v(-15.08, -0.03) * mm});
            skLineSegment(sketch, "E686", {"start": v(-15.08, -0.03) * mm, "end": v(-15.03, -0.03) * mm});
            skLineSegment(sketch, "E687", {"start": v(-15.03, -0.03) * mm, "end": v(-14.97, -0.03) * mm});
            skLineSegment(sketch, "E688", {"start": v(-14.97, -0.03) * mm, "end": v(-14.92, -0.03) * mm});
            skLineSegment(sketch, "E689", {"start": v(-14.92, -0.03) * mm, "end": v(-14.86, -0.03) * mm});
            skLineSegment(sketch, "E690", {"start": v(-14.86, -0.03) * mm, "end": v(-14.8, -0.03) * mm});
            skLineSegment(sketch, "E691", {"start": v(-14.8, -0.03) * mm, "end": v(-14.75, -0.03) * mm});
            skLineSegment(sketch, "E692", {"start": v(-14.75, -0.03) * mm, "end": v(-14.7, -0.03) * mm});
            skLineSegment(sketch, "E693", {"start": v(-14.7, -0.03) * mm, "end": v(-14.64, -0.03) * mm});
            skLineSegment(sketch, "E694", {"start": v(-14.64, -0.03) * mm, "end": v(-14.58, -0.03) * mm});
            skLineSegment(sketch, "E695", {"start": v(-14.58, -0.03) * mm, "end": v(-14.53, -0.03) * mm});
            skLineSegment(sketch, "E696", {"start": v(-14.53, -0.03) * mm, "end": v(-14.47, -0.03) * mm});
            skLineSegment(sketch, "E697", {"start": v(-14.47, -0.03) * mm, "end": v(-14.42, -0.03) * mm});
            skLineSegment(sketch, "E698", {"start": v(-14.42, -0.03) * mm, "end": v(-14.36, -0.03) * mm});
            skLineSegment(sketch, "E699", {"start": v(-14.36, -0.03) * mm, "end": v(-14.3, -0.03) * mm});
            skLineSegment(sketch, "E700", {"start": v(-14.3, -0.03) * mm, "end": v(-14.25, -0.03) * mm});
            skLineSegment(sketch, "E701", {"start": v(-14.25, -0.03) * mm, "end": v(-14.2, -0.03) * mm});
            skLineSegment(sketch, "E702", {"start": v(-14.2, -0.03) * mm, "end": v(-14.14, -0.03) * mm});
            skLineSegment(sketch, "E703", {"start": v(-14.14, -0.03) * mm, "end": v(-14.09, -0.03) * mm});
            skLineSegment(sketch, "E704", {"start": v(-14.09, -0.03) * mm, "end": v(-14.03, -0.03) * mm});
            skLineSegment(sketch, "E705", {"start": v(-14.03, -0.03) * mm, "end": v(-13.97, -0.03) * mm});
            skLineSegment(sketch, "E706", {"start": v(-13.97, -0.03) * mm, "end": v(-13.92, -0.03) * mm});
            skLineSegment(sketch, "E707", {"start": v(-13.92, -0.03) * mm, "end": v(-13.86, -0.03) * mm});
            skLineSegment(sketch, "E708", {"start": v(-13.86, -0.03) * mm, "end": v(-13.8, -0.03) * mm});
            skLineSegment(sketch, "E709", {"start": v(-13.8, -0.03) * mm, "end": v(-13.75, -0.03) * mm});
            skLineSegment(sketch, "E710", {"start": v(-13.75, -0.03) * mm, "end": v(-13.7, -0.03) * mm});
            skLineSegment(sketch, "E711", {"start": v(-13.7, -0.03) * mm, "end": v(-13.64, -0.03) * mm});
            skLineSegment(sketch, "E712", {"start": v(-13.64, -0.03) * mm, "end": v(-13.59, -0.03) * mm});
            skLineSegment(sketch, "E713", {"start": v(-13.59, -0.03) * mm, "end": v(-13.53, -0.03) * mm});
            skLineSegment(sketch, "E714", {"start": v(-13.53, -0.03) * mm, "end": v(-13.48, -0.03) * mm});
            skLineSegment(sketch, "E715", {"start": v(-13.48, -0.03) * mm, "end": v(-13.42, -0.03) * mm});
            skLineSegment(sketch, "E716", {"start": v(-13.42, -0.03) * mm, "end": v(-13.36, -0.03) * mm});
            skLineSegment(sketch, "E717", {"start": v(-13.36, -0.03) * mm, "end": v(-13.3, -0.03) * mm});
            skLineSegment(sketch, "E718", {"start": v(-13.3, -0.03) * mm, "end": v(-13.25, -0.03) * mm});
            skLineSegment(sketch, "E719", {"start": v(-13.25, -0.03) * mm, "end": v(-13.2, -0.03) * mm});
            skLineSegment(sketch, "E720", {"start": v(-13.2, -0.03) * mm, "end": v(-13.14, -0.03) * mm});
            skLineSegment(sketch, "E721", {"start": v(-13.14, -0.03) * mm, "end": v(-13.09, -0.03) * mm});
            skLineSegment(sketch, "E722", {"start": v(-13.09, -0.03) * mm, "end": v(-13.03, -0.03) * mm});
            skLineSegment(sketch, "E723", {"start": v(-13.03, -0.03) * mm, "end": v(-12.98, -0.03) * mm});
            skLineSegment(sketch, "E724", {"start": v(-12.98, -0.03) * mm, "end": v(-12.92, -0.03) * mm});
            skLineSegment(sketch, "E725", {"start": v(-12.92, -0.03) * mm, "end": v(-12.87, -0.03) * mm});
            skLineSegment(sketch, "E726", {"start": v(-12.87, -0.03) * mm, "end": v(-12.8, -0.03) * mm});
            skLineSegment(sketch, "E727", {"start": v(-12.8, -0.03) * mm, "end": v(-12.75, -0.03) * mm});
            skLineSegment(sketch, "E728", {"start": v(-12.75, -0.03) * mm, "end": v(-12.7, -0.03) * mm});
            skLineSegment(sketch, "E729", {"start": v(-12.7, -0.03) * mm, "end": v(-12.64, -0.03) * mm});
            skLineSegment(sketch, "E730", {"start": v(-12.64, -0.03) * mm, "end": v(-12.59, -0.03) * mm});
            skLineSegment(sketch, "E731", {"start": v(-12.59, -0.03) * mm, "end": v(-12.53, -0.03) * mm});
            skLineSegment(sketch, "E732", {"start": v(-12.53, -0.03) * mm, "end": v(-12.48, -0.03) * mm});
            skLineSegment(sketch, "E733", {"start": v(-12.48, -0.03) * mm, "end": v(-12.42, -0.03) * mm});
            skLineSegment(sketch, "E734", {"start": v(-12.42, -0.03) * mm, "end": v(-12.37, -0.03) * mm});
            skLineSegment(sketch, "E735", {"start": v(-12.37, -0.03) * mm, "end": v(-12.31, -0.03) * mm});
            skLineSegment(sketch, "E736", {"start": v(-12.31, -0.03) * mm, "end": v(-12.26, -0.03) * mm});
            skLineSegment(sketch, "E737", {"start": v(-12.26, -0.03) * mm, "end": v(-12.2, -0.03) * mm});
            skLineSegment(sketch, "E738", {"start": v(-12.2, -0.03) * mm, "end": v(-12.14, -0.03) * mm});
            skLineSegment(sketch, "E739", {"start": v(-12.14, -0.03) * mm, "end": v(-12.09, -0.03) * mm});
            skLineSegment(sketch, "E740", {"start": v(-12.09, -0.03) * mm, "end": v(-12.03, -0.03) * mm});
            skLineSegment(sketch, "E741", {"start": v(-12.03, -0.03) * mm, "end": v(-11.98, -0.03) * mm});
            skLineSegment(sketch, "E742", {"start": v(-11.98, -0.03) * mm, "end": v(-11.92, -0.03) * mm});
            skLineSegment(sketch, "E743", {"start": v(-11.92, -0.03) * mm, "end": v(-11.87, -0.03) * mm});
            skLineSegment(sketch, "E744", {"start": v(-11.87, -0.03) * mm, "end": v(-11.81, -0.03) * mm});
            skLineSegment(sketch, "E745", {"start": v(-11.81, -0.03) * mm, "end": v(-11.76, -0.03) * mm});
            skLineSegment(sketch, "E746", {"start": v(-11.76, -0.03) * mm, "end": v(-11.7, -0.03) * mm});
            skLineSegment(sketch, "E747", {"start": v(-11.7, -0.03) * mm, "end": v(-11.65, -0.03) * mm});
            skLineSegment(sketch, "E748", {"start": v(-11.65, -0.03) * mm, "end": v(-11.59, -0.03) * mm});
            skLineSegment(sketch, "E749", {"start": v(-11.59, -0.03) * mm, "end": v(-11.53, -0.03) * mm});
            skLineSegment(sketch, "E750", {"start": v(-11.53, -0.03) * mm, "end": v(-11.48, -0.03) * mm});
            skLineSegment(sketch, "E751", {"start": v(-11.48, -0.03) * mm, "end": v(-11.42, -0.03) * mm});
            skLineSegment(sketch, "E752", {"start": v(-11.42, -0.03) * mm, "end": v(-11.37, -0.03) * mm});
            skLineSegment(sketch, "E753", {"start": v(-11.37, -0.03) * mm, "end": v(-11.31, -0.03) * mm});
            skLineSegment(sketch, "E754", {"start": v(-11.31, -0.03) * mm, "end": v(-11.26, -0.03) * mm});
            skLineSegment(sketch, "E755", {"start": v(-11.26, -0.03) * mm, "end": v(-11.2, -0.03) * mm});
            skLineSegment(sketch, "E756", {"start": v(-11.2, -0.03) * mm, "end": v(-11.15, -0.03) * mm});
            skLineSegment(sketch, "E757", {"start": v(-11.15, -0.03) * mm, "end": v(-11.1, -0.03) * mm});
            skLineSegment(sketch, "E758", {"start": v(-11.1, -0.03) * mm, "end": v(-11.04, -0.03) * mm});
            skLineSegment(sketch, "E759", {"start": v(-11.04, -0.03) * mm, "end": v(-10.98, -0.03) * mm});
            skLineSegment(sketch, "E760", {"start": v(-10.98, -0.03) * mm, "end": v(-10.92, -0.03) * mm});
            skLineSegment(sketch, "E761", {"start": v(-10.92, -0.03) * mm, "end": v(-10.87, -0.03) * mm});
            skLineSegment(sketch, "E762", {"start": v(-10.87, -0.03) * mm, "end": v(-10.81, -0.03) * mm});
            skLineSegment(sketch, "E763", {"start": v(-10.81, -0.03) * mm, "end": v(-10.76, -0.03) * mm});
            skLineSegment(sketch, "E764", {"start": v(-10.76, -0.03) * mm, "end": v(-10.7, -0.03) * mm});
            skLineSegment(sketch, "E765", {"start": v(-10.7, -0.03) * mm, "end": v(-10.65, -0.03) * mm});
            skLineSegment(sketch, "E766", {"start": v(-10.65, -0.03) * mm, "end": v(-10.6, -0.03) * mm});
            skLineSegment(sketch, "E767", {"start": v(-10.6, -0.03) * mm, "end": v(-10.54, -0.03) * mm});
            skLineSegment(sketch, "E768", {"start": v(-10.54, -0.03) * mm, "end": v(-10.48, -0.03) * mm});
            skLineSegment(sketch, "E769", {"start": v(-10.48, -0.03) * mm, "end": v(-10.43, -0.03) * mm});
            skLineSegment(sketch, "E770", {"start": v(-10.43, -0.03) * mm, "end": v(-10.37, -0.03) * mm});
            skLineSegment(sketch, "E771", {"start": v(-10.37, -0.03) * mm, "end": v(-10.31, -0.03) * mm});
            skLineSegment(sketch, "E772", {"start": v(-10.31, -0.03) * mm, "end": v(-10.26, -0.03) * mm});
            skLineSegment(sketch, "E773", {"start": v(-10.26, -0.03) * mm, "end": v(-10.2, -0.03) * mm});
            skLineSegment(sketch, "E774", {"start": v(-10.2, -0.03) * mm, "end": v(-10.15, -0.03) * mm});
            skLineSegment(sketch, "E775", {"start": v(-10.15, -0.03) * mm, "end": v(-10.1, -0.03) * mm});
            skLineSegment(sketch, "E776", {"start": v(-10.1, -0.03) * mm, "end": v(-10.04, -0.03) * mm});
            skLineSegment(sketch, "E777", {"start": v(-10.04, -0.03) * mm, "end": v(-9.98, -0.03) * mm});
            skLineSegment(sketch, "E778", {"start": v(-9.98, -0.03) * mm, "end": v(-9.93, -0.03) * mm});
            skLineSegment(sketch, "E779", {"start": v(-9.93, -0.03) * mm, "end": v(-9.87, -0.03) * mm});
            skLineSegment(sketch, "E780", {"start": v(-9.87, -0.03) * mm, "end": v(-9.82, -0.03) * mm});
            skLineSegment(sketch, "E781", {"start": v(-9.82, -0.03) * mm, "end": v(-9.76, -0.03) * mm});
            skLineSegment(sketch, "E782", {"start": v(-9.76, -0.03) * mm, "end": v(-9.7, -0.03) * mm});
            skLineSegment(sketch, "E783", {"start": v(-9.7, -0.03) * mm, "end": v(-9.65, -0.03) * mm});
            skLineSegment(sketch, "E784", {"start": v(-9.65, -0.03) * mm, "end": v(-9.6, -0.03) * mm});
            skLineSegment(sketch, "E785", {"start": v(-9.6, -0.03) * mm, "end": v(-9.54, -0.03) * mm});
            skLineSegment(sketch, "E786", {"start": v(-9.54, -0.03) * mm, "end": v(-9.48, -0.03) * mm});
            skLineSegment(sketch, "E787", {"start": v(-9.48, -0.03) * mm, "end": v(-9.43, -0.03) * mm});
            skLineSegment(sketch, "E788", {"start": v(-9.43, -0.03) * mm, "end": v(-9.37, -0.03) * mm});
            skLineSegment(sketch, "E789", {"start": v(-9.37, -0.03) * mm, "end": v(-9.32, -0.03) * mm});
            skLineSegment(sketch, "E790", {"start": v(-9.32, -0.03) * mm, "end": v(-9.26, -0.03) * mm});
            skLineSegment(sketch, "E791", {"start": v(-9.26, -0.03) * mm, "end": v(-9.2, -0.03) * mm});
            skLineSegment(sketch, "E792", {"start": v(-9.2, -0.03) * mm, "end": v(-9.15, -0.03) * mm});
            skLineSegment(sketch, "E793", {"start": v(-9.15, -0.03) * mm, "end": v(-9.1, -0.03) * mm});
            skLineSegment(sketch, "E794", {"start": v(-9.1, -0.03) * mm, "end": v(-9.04, -0.03) * mm});
            skLineSegment(sketch, "E795", {"start": v(-9.04, -0.03) * mm, "end": v(-8.98, -0.03) * mm});
            skLineSegment(sketch, "E796", {"start": v(-8.98, -0.03) * mm, "end": v(-8.93, -0.03) * mm});
            skLineSegment(sketch, "E797", {"start": v(-8.93, -0.03) * mm, "end": v(-8.87, -0.03) * mm});
            skLineSegment(sketch, "E798", {"start": v(-8.87, -0.03) * mm, "end": v(-8.82, -0.03) * mm});
            skLineSegment(sketch, "E799", {"start": v(-8.82, -0.03) * mm, "end": v(-8.76, -0.03) * mm});
            skLineSegment(sketch, "E800", {"start": v(-8.76, -0.03) * mm, "end": v(-8.7, -0.03) * mm});
            skLineSegment(sketch, "E801", {"start": v(-8.7, -0.03) * mm, "end": v(-8.65, -0.03) * mm});
            skLineSegment(sketch, "E802", {"start": v(-8.65, -0.03) * mm, "end": v(-8.6, -0.03) * mm});
            skLineSegment(sketch, "E803", {"start": v(-8.6, -0.03) * mm, "end": v(-8.54, -0.03) * mm});
            skLineSegment(sketch, "E804", {"start": v(-8.54, -0.03) * mm, "end": v(-8.48, -0.03) * mm});
            skLineSegment(sketch, "E805", {"start": v(-8.48, -0.03) * mm, "end": v(-8.43, -0.03) * mm});
            skLineSegment(sketch, "E806", {"start": v(-8.43, -0.03) * mm, "end": v(-8.37, -0.03) * mm});
            skLineSegment(sketch, "E807", {"start": v(-8.37, -0.03) * mm, "end": v(-8.32, -0.03) * mm});
            skLineSegment(sketch, "E808", {"start": v(-8.32, -0.03) * mm, "end": v(-8.26, -0.03) * mm});
            skLineSegment(sketch, "E809", {"start": v(-8.26, -0.03) * mm, "end": v(-8.2, -0.03) * mm});
            skLineSegment(sketch, "E810", {"start": v(-8.2, -0.03) * mm, "end": v(-8.15, -0.03) * mm});
            skLineSegment(sketch, "E811", {"start": v(-8.15, -0.03) * mm, "end": v(-8.1, -0.03) * mm});
            skLineSegment(sketch, "E812", {"start": v(-8.1, -0.03) * mm, "end": v(-8.04, -0.03) * mm});
            skLineSegment(sketch, "E813", {"start": v(-8.04, -0.03) * mm, "end": v(-7.99, -0.03) * mm});
            skLineSegment(sketch, "E814", {"start": v(-7.99, -0.03) * mm, "end": v(-7.93, -0.03) * mm});
            skLineSegment(sketch, "E815", {"start": v(-7.93, -0.03) * mm, "end": v(-7.87, -0.03) * mm});
            skLineSegment(sketch, "E816", {"start": v(-7.87, -0.03) * mm, "end": v(-7.82, -0.03) * mm});
            skLineSegment(sketch, "E817", {"start": v(-7.82, -0.03) * mm, "end": v(-7.76, -0.03) * mm});
            skLineSegment(sketch, "E818", {"start": v(-7.76, -0.03) * mm, "end": v(-7.7, -0.03) * mm});
            skLineSegment(sketch, "E819", {"start": v(-7.7, -0.03) * mm, "end": v(-7.65, -0.03) * mm});
            skLineSegment(sketch, "E820", {"start": v(-7.65, -0.03) * mm, "end": v(-7.6, -0.03) * mm});
            skLineSegment(sketch, "E821", {"start": v(-7.6, -0.03) * mm, "end": v(-7.54, -0.03) * mm});
            skLineSegment(sketch, "E822", {"start": v(-7.54, -0.03) * mm, "end": v(-7.49, -0.03) * mm});
            skLineSegment(sketch, "E823", {"start": v(-7.49, -0.03) * mm, "end": v(-7.43, -0.03) * mm});
            skLineSegment(sketch, "E824", {"start": v(-7.43, -0.03) * mm, "end": v(-7.38, -0.03) * mm});
            skLineSegment(sketch, "E825", {"start": v(-7.38, -0.03) * mm, "end": v(-7.32, -0.03) * mm});
            skLineSegment(sketch, "E826", {"start": v(-7.32, -0.03) * mm, "end": v(-7.26, -0.03) * mm});
            skLineSegment(sketch, "E827", {"start": v(-7.26, -0.03) * mm, "end": v(-7.2, -0.03) * mm});
            skLineSegment(sketch, "E828", {"start": v(-7.2, -0.03) * mm, "end": v(-7.15, -0.03) * mm});
            skLineSegment(sketch, "E829", {"start": v(-7.15, -0.03) * mm, "end": v(-7.1, -0.03) * mm});
            skLineSegment(sketch, "E830", {"start": v(-7.1, -0.03) * mm, "end": v(-7.04, -0.03) * mm});
            skLineSegment(sketch, "E831", {"start": v(-7.04, -0.03) * mm, "end": v(-6.99, -0.03) * mm});
            skLineSegment(sketch, "E832", {"start": v(-6.99, -0.03) * mm, "end": v(-6.93, -0.03) * mm});
            skLineSegment(sketch, "E833", {"start": v(-6.93, -0.03) * mm, "end": v(-6.88, -0.03) * mm});
            skLineSegment(sketch, "E834", {"start": v(-6.88, -0.03) * mm, "end": v(-6.82, -0.03) * mm});
            skLineSegment(sketch, "E835", {"start": v(-6.82, -0.03) * mm, "end": v(-6.77, -0.03) * mm});
            skLineSegment(sketch, "E836", {"start": v(-6.77, -0.03) * mm, "end": v(-6.7, -0.03) * mm});
            skLineSegment(sketch, "E837", {"start": v(-6.7, -0.03) * mm, "end": v(-6.65, -0.03) * mm});
            skLineSegment(sketch, "E838", {"start": v(-6.65, -0.03) * mm, "end": v(-6.6, -0.03) * mm});
            skLineSegment(sketch, "E839", {"start": v(-6.6, -0.03) * mm, "end": v(-6.54, -0.03) * mm});
            skLineSegment(sketch, "E840", {"start": v(-6.54, -0.03) * mm, "end": v(-6.49, -0.03) * mm});
            skLineSegment(sketch, "E841", {"start": v(-6.49, -0.03) * mm, "end": v(-6.43, -0.03) * mm});
            skLineSegment(sketch, "E842", {"start": v(-6.43, -0.03) * mm, "end": v(-6.38, -0.03) * mm});
            skLineSegment(sketch, "E843", {"start": v(-6.38, -0.03) * mm, "end": v(-6.32, -0.03) * mm});
            skLineSegment(sketch, "E844", {"start": v(-6.32, -0.03) * mm, "end": v(-6.27, -0.03) * mm});
            skLineSegment(sketch, "E845", {"start": v(-6.27, -0.03) * mm, "end": v(-6.21, -0.03) * mm});
            skLineSegment(sketch, "E846", {"start": v(-6.21, -0.03) * mm, "end": v(-6.16, -0.03) * mm});
            skLineSegment(sketch, "E847", {"start": v(-6.16, -0.03) * mm, "end": v(-6.1, -0.03) * mm});
            skLineSegment(sketch, "E848", {"start": v(-6.1, -0.03) * mm, "end": v(-6.04, -0.03) * mm});
            skLineSegment(sketch, "E849", {"start": v(-6.04, -0.03) * mm, "end": v(-5.99, -0.03) * mm});
            skLineSegment(sketch, "E850", {"start": v(-5.99, -0.03) * mm, "end": v(-5.66, -0.03) * mm});
            skLineSegment(sketch, "E851", {"start": v(-5.66, -0.03) * mm, "end": v(-5.49, 0.08) * mm});
            skLineSegment(sketch, "E852", {"start": v(-5.49, 0.08) * mm, "end": v(-5.32, 0.25) * mm});
            skLineSegment(sketch, "E853", {"start": v(-5.32, 0.25) * mm, "end": v(-5.27, 0.42) * mm});
            skLineSegment(sketch, "E854", {"start": v(-5.27, 0.42) * mm, "end": v(-5.27, 0.58) * mm});
            skLineSegment(sketch, "E855", {"start": v(-5.27, 0.58) * mm, "end": v(-5.21, 0.58) * mm});
            skLineSegment(sketch, "E856", {"start": v(-5.21, 0.58) * mm, "end": v(-5.21, 0.97) * mm});
            skLineSegment(sketch, "E857", {"start": v(-5.21, 0.97) * mm, "end": v(-5.16, 0.97) * mm});
            skLineSegment(sketch, "E858", {"start": v(-5.16, 0.97) * mm, "end": v(-5.16, 1.25) * mm});
            skLineSegment(sketch, "E859", {"start": v(-5.16, 1.25) * mm, "end": v(-5.1, 1.25) * mm});
            skLineSegment(sketch, "E860", {"start": v(-5.1, 1.25) * mm, "end": v(-5.1, 1.47) * mm});
            skLineSegment(sketch, "E861", {"start": v(-5.1, 1.47) * mm, "end": v(-5.05, 1.64) * mm});
            skLineSegment(sketch, "E862", {"start": v(-5.05, 1.64) * mm, "end": v(-4.94, 1.75) * mm});
            skLineSegment(sketch, "E863", {"start": v(-4.94, 1.75) * mm, "end": v(-4.88, 2.08) * mm});
            skLineSegment(sketch, "E864", {"start": v(-4.88, 2.08) * mm, "end": v(-4.77, 2.2) * mm});
            skLineSegment(sketch, "E865", {"start": v(-4.77, 2.2) * mm, "end": v(-4.77, 2.3) * mm});
            skLineSegment(sketch, "E866", {"start": v(-4.77, 2.3) * mm, "end": v(-4.71, 2.3) * mm});
            skLineSegment(sketch, "E867", {"start": v(-4.71, 2.3) * mm, "end": v(-4.71, 2.41) * mm});
            skLineSegment(sketch, "E868", {"start": v(-4.71, 2.41) * mm, "end": v(-4.66, 2.41) * mm});
            skLineSegment(sketch, "E869", {"start": v(-4.66, 2.41) * mm, "end": v(-4.66, 2.52) * mm});
            skLineSegment(sketch, "E870", {"start": v(-4.66, 2.52) * mm, "end": v(-4.6, 2.52) * mm});
            skLineSegment(sketch, "E871", {"start": v(-4.6, 2.52) * mm, "end": v(-4.6, 2.63) * mm});
            skLineSegment(sketch, "E872", {"start": v(-4.6, 2.63) * mm, "end": v(-4.55, 2.63) * mm});
            skLineSegment(sketch, "E873", {"start": v(-4.55, 2.63) * mm, "end": v(-4.55, 2.74) * mm});
            skLineSegment(sketch, "E874", {"start": v(-4.55, 2.74) * mm, "end": v(-4.44, 2.8) * mm});
            skLineSegment(sketch, "E875", {"start": v(-4.44, 2.8) * mm, "end": v(-4.44, 2.91) * mm});
            skLineSegment(sketch, "E876", {"start": v(-4.44, 2.91) * mm, "end": v(-4.27, 3.02) * mm});
            skLineSegment(sketch, "E877", {"start": v(-4.27, 3.02) * mm, "end": v(-4.27, 3.13) * mm});
            skLineSegment(sketch, "E878", {"start": v(-4.27, 3.13) * mm, "end": v(-4.21, 3.19) * mm});
            skLineSegment(sketch, "E879", {"start": v(-4.21, 3.19) * mm, "end": v(-4.1, 3.24) * mm});
            skLineSegment(sketch, "E880", {"start": v(-4.1, 3.24) * mm, "end": v(-4.05, 3.3) * mm});
            skLineSegment(sketch, "E881", {"start": v(-4.05, 3.3) * mm, "end": v(-4.05, 3.41) * mm});
            skLineSegment(sketch, "E882", {"start": v(-4.05, 3.41) * mm, "end": v(-4, 3.47) * mm});
            skLineSegment(sketch, "E883", {"start": v(-4, 3.47) * mm, "end": v(-3.88, 3.58) * mm});
            skLineSegment(sketch, "E884", {"start": v(-3.88, 3.58) * mm, "end": v(-3.83, 3.58) * mm});
            skLineSegment(sketch, "E885", {"start": v(-3.83, 3.58) * mm, "end": v(-3.83, 3.63) * mm});
            skLineSegment(sketch, "E886", {"start": v(-3.83, 3.63) * mm, "end": v(-3.77, 3.63) * mm});
            skLineSegment(sketch, "E887", {"start": v(-3.77, 3.63) * mm, "end": v(-3.77, 3.69) * mm});
            skLineSegment(sketch, "E888", {"start": v(-3.77, 3.69) * mm, "end": v(-3.72, 3.69) * mm});
            skLineSegment(sketch, "E889", {"start": v(-3.72, 3.69) * mm, "end": v(-3.72, 3.74) * mm});
            skLineSegment(sketch, "E890", {"start": v(-3.72, 3.74) * mm, "end": v(-3.66, 3.74) * mm});
            skLineSegment(sketch, "E891", {"start": v(-3.66, 3.74) * mm, "end": v(-3.66, 3.8) * mm});
            skLineSegment(sketch, "E892", {"start": v(-3.66, 3.8) * mm, "end": v(-3.6, 3.8) * mm});
            skLineSegment(sketch, "E893", {"start": v(-3.6, 3.8) * mm, "end": v(-3.6, 3.85) * mm});
            skLineSegment(sketch, "E894", {"start": v(-3.6, 3.85) * mm, "end": v(-3.55, 3.85) * mm});
            skLineSegment(sketch, "E895", {"start": v(-3.55, 3.85) * mm, "end": v(-3.44, 4.02) * mm});
            skLineSegment(sketch, "E896", {"start": v(-3.44, 4.02) * mm, "end": v(-3.33, 4.02) * mm});
            skLineSegment(sketch, "E897", {"start": v(-3.33, 4.02) * mm, "end": v(-3.27, 4.08) * mm});
            skLineSegment(sketch, "E898", {"start": v(-3.27, 4.08) * mm, "end": v(-3.22, 4.19) * mm});
            skLineSegment(sketch, "E899", {"start": v(-3.22, 4.19) * mm, "end": v(-3.16, 4.24) * mm});
            skLineSegment(sketch, "E900", {"start": v(-3.16, 4.24) * mm, "end": v(-3.05, 4.24) * mm});
            skLineSegment(sketch, "E901", {"start": v(-3.05, 4.24) * mm, "end": v(-3, 4.3) * mm});
            skLineSegment(sketch, "E902", {"start": v(-3, 4.3) * mm, "end": v(-2.94, 4.35) * mm});
            skLineSegment(sketch, "E903", {"start": v(-2.94, 4.35) * mm, "end": v(-2.88, 4.4) * mm});
            skLineSegment(sketch, "E904", {"start": v(-2.88, 4.4) * mm, "end": v(-2.77, 4.63) * mm});
            skLineSegment(sketch, "E905", {"start": v(-2.77, 4.63) * mm, "end": v(-2.77, 4.96) * mm});
            skLineSegment(sketch, "E906", {"start": v(-2.77, 4.96) * mm, "end": v(-2.88, 5.18) * mm});
            skLineSegment(sketch, "E907", {"start": v(-2.88, 5.18) * mm, "end": v(-3, 5.24) * mm});
            skLineSegment(sketch, "E908", {"start": v(-3, 5.24) * mm, "end": v(-3, 5.35) * mm});
            skLineSegment(sketch, "E909", {"start": v(-3, 5.35) * mm, "end": v(-3.05, 5.35) * mm});
            skLineSegment(sketch, "E910", {"start": v(-3.05, 5.35) * mm, "end": v(-3.05, 5.46) * mm});
            skLineSegment(sketch, "E911", {"start": v(-3.05, 5.46) * mm, "end": v(-3.1, 5.57) * mm});
            skLineSegment(sketch, "E912", {"start": v(-3.1, 5.57) * mm, "end": v(-3.22, 5.63) * mm});
            skLineSegment(sketch, "E913", {"start": v(-3.22, 5.63) * mm, "end": v(-3.22, 5.74) * mm});
            skLineSegment(sketch, "E914", {"start": v(-3.22, 5.74) * mm, "end": v(-3.33, 5.8) * mm});
            skLineSegment(sketch, "E915", {"start": v(-3.33, 5.8) * mm, "end": v(-3.33, 5.9) * mm});
            skLineSegment(sketch, "E916", {"start": v(-3.33, 5.9) * mm, "end": v(-3.38, 5.9) * mm});
            skLineSegment(sketch, "E917", {"start": v(-3.38, 5.9) * mm, "end": v(-3.38, 6.02) * mm});
            skLineSegment(sketch, "E918", {"start": v(-3.38, 6.02) * mm, "end": v(-3.44, 6.13) * mm});
            skLineSegment(sketch, "E919", {"start": v(-3.44, 6.13) * mm, "end": v(-3.55, 6.18) * mm});
            skLineSegment(sketch, "E920", {"start": v(-3.55, 6.18) * mm, "end": v(-3.55, 6.3) * mm});
            skLineSegment(sketch, "E921", {"start": v(-3.55, 6.3) * mm, "end": v(-3.66, 6.35) * mm});
            skLineSegment(sketch, "E922", {"start": v(-3.66, 6.35) * mm, "end": v(-3.72, 6.57) * mm});
            skLineSegment(sketch, "E923", {"start": v(-3.72, 6.57) * mm, "end": v(-3.83, 6.63) * mm});
            skLineSegment(sketch, "E924", {"start": v(-3.83, 6.63) * mm, "end": v(-3.83, 6.74) * mm});
            skLineSegment(sketch, "E925", {"start": v(-3.83, 6.74) * mm, "end": v(-3.94, 6.8) * mm});
            skLineSegment(sketch, "E926", {"start": v(-3.94, 6.8) * mm, "end": v(-3.94, 6.9) * mm});
            skLineSegment(sketch, "E927", {"start": v(-3.94, 6.9) * mm, "end": v(-4, 6.9) * mm});
            skLineSegment(sketch, "E928", {"start": v(-4, 6.9) * mm, "end": v(-4, 7.01) * mm});
            skLineSegment(sketch, "E929", {"start": v(-4, 7.01) * mm, "end": v(-4.05, 7.13) * mm});
            skLineSegment(sketch, "E930", {"start": v(-4.05, 7.13) * mm, "end": v(-4.16, 7.18) * mm});
            skLineSegment(sketch, "E931", {"start": v(-4.16, 7.18) * mm, "end": v(-4.16, 7.3) * mm});
            skLineSegment(sketch, "E932", {"start": v(-4.16, 7.3) * mm, "end": v(-4.21, 7.3) * mm});
            skLineSegment(sketch, "E933", {"start": v(-4.21, 7.3) * mm, "end": v(-4.21, 7.4) * mm});
            skLineSegment(sketch, "E934", {"start": v(-4.21, 7.4) * mm, "end": v(-4.27, 7.51) * mm});
            skLineSegment(sketch, "E935", {"start": v(-4.27, 7.51) * mm, "end": v(-4.38, 7.57) * mm});
            skLineSegment(sketch, "E936", {"start": v(-4.38, 7.57) * mm, "end": v(-4.38, 7.68) * mm});
            skLineSegment(sketch, "E937", {"start": v(-4.38, 7.68) * mm, "end": v(-4.5, 7.74) * mm});
            skLineSegment(sketch, "E938", {"start": v(-4.5, 7.74) * mm, "end": v(-4.5, 7.85) * mm});
            skLineSegment(sketch, "E939", {"start": v(-4.5, 7.85) * mm, "end": v(-4.55, 7.85) * mm});
            skLineSegment(sketch, "E940", {"start": v(-4.55, 7.85) * mm, "end": v(-4.55, 7.96) * mm});
            skLineSegment(sketch, "E941", {"start": v(-4.55, 7.96) * mm, "end": v(-4.6, 8.07) * mm});
            skLineSegment(sketch, "E942", {"start": v(-4.6, 8.07) * mm, "end": v(-4.77, 8.18) * mm});
            skLineSegment(sketch, "E943", {"start": v(-4.77, 8.18) * mm, "end": v(-4.88, 8.51) * mm});
            skLineSegment(sketch, "E944", {"start": v(-4.88, 8.51) * mm, "end": v(-5, 8.57) * mm});
            skLineSegment(sketch, "E945", {"start": v(-5, 8.57) * mm, "end": v(-5.05, 8.79) * mm});
            skLineSegment(sketch, "E946", {"start": v(-5.05, 8.79) * mm, "end": v(-5.16, 8.84) * mm});
            skLineSegment(sketch, "E947", {"start": v(-5.16, 8.84) * mm, "end": v(-5.21, 9.07) * mm});
            skLineSegment(sketch, "E948", {"start": v(-5.21, 9.07) * mm, "end": v(-5.32, 9.12) * mm});
            skLineSegment(sketch, "E949", {"start": v(-5.32, 9.12) * mm, "end": v(-5.38, 9.34) * mm});
            skLineSegment(sketch, "E950", {"start": v(-5.38, 9.34) * mm, "end": v(-5.49, 9.4) * mm});
            skLineSegment(sketch, "E951", {"start": v(-5.49, 9.4) * mm, "end": v(-5.55, 9.62) * mm});
            skLineSegment(sketch, "E952", {"start": v(-5.55, 9.62) * mm, "end": v(-5.66, 9.68) * mm});
            skLineSegment(sketch, "E953", {"start": v(-5.66, 9.68) * mm, "end": v(-5.66, 9.79) * mm});
            skLineSegment(sketch, "E954", {"start": v(-5.66, 9.79) * mm, "end": v(-5.77, 9.84) * mm});
            skLineSegment(sketch, "E955", {"start": v(-5.77, 9.84) * mm, "end": v(-5.77, 9.95) * mm});
            skLineSegment(sketch, "E956", {"start": v(-5.77, 9.95) * mm, "end": v(-5.82, 9.95) * mm});
            skLineSegment(sketch, "E957", {"start": v(-5.82, 9.95) * mm, "end": v(-5.82, 10.06) * mm});
            skLineSegment(sketch, "E958", {"start": v(-5.82, 10.06) * mm, "end": v(-5.88, 10.18) * mm});
            skLineSegment(sketch, "E959", {"start": v(-5.88, 10.18) * mm, "end": v(-5.99, 10.23) * mm});
            skLineSegment(sketch, "E960", {"start": v(-5.99, 10.23) * mm, "end": v(-6.04, 10.45) * mm});
            skLineSegment(sketch, "E961", {"start": v(-6.04, 10.45) * mm, "end": v(-6.16, 10.5) * mm});
            skLineSegment(sketch, "E962", {"start": v(-6.16, 10.5) * mm, "end": v(-6.21, 10.73) * mm});
            skLineSegment(sketch, "E963", {"start": v(-6.21, 10.73) * mm, "end": v(-6.32, 10.79) * mm});
            skLineSegment(sketch, "E964", {"start": v(-6.32, 10.79) * mm, "end": v(-6.32, 10.9) * mm});
            skLineSegment(sketch, "E965", {"start": v(-6.32, 10.9) * mm, "end": v(-6.43, 10.95) * mm});
            skLineSegment(sketch, "E966", {"start": v(-6.43, 10.95) * mm, "end": v(-6.49, 11.17) * mm});
            skLineSegment(sketch, "E967", {"start": v(-6.49, 11.17) * mm, "end": v(-6.6, 11.23) * mm});
            skLineSegment(sketch, "E968", {"start": v(-6.6, 11.23) * mm, "end": v(-6.6, 11.34) * mm});
            skLineSegment(sketch, "E969", {"start": v(-6.6, 11.34) * mm, "end": v(-6.65, 11.34) * mm});
            skLineSegment(sketch, "E970", {"start": v(-6.65, 11.34) * mm, "end": v(-6.65, 11.45) * mm});
            skLineSegment(sketch, "E971", {"start": v(-6.65, 11.45) * mm, "end": v(-6.7, 11.56) * mm});
            skLineSegment(sketch, "E972", {"start": v(-6.7, 11.56) * mm, "end": v(-6.82, 11.62) * mm});
            skLineSegment(sketch, "E973", {"start": v(-6.82, 11.62) * mm, "end": v(-6.88, 11.84) * mm});
            skLineSegment(sketch, "E974", {"start": v(-6.88, 11.84) * mm, "end": v(-6.99, 11.9) * mm});
            skLineSegment(sketch, "E975", {"start": v(-6.99, 11.9) * mm, "end": v(-7.04, 12.12) * mm});
            skLineSegment(sketch, "E976", {"start": v(-7.04, 12.12) * mm, "end": v(-7.15, 12.17) * mm});
            skLineSegment(sketch, "E977", {"start": v(-7.15, 12.17) * mm, "end": v(-7.15, 12.28) * mm});
            skLineSegment(sketch, "E978", {"start": v(-7.15, 12.28) * mm, "end": v(-7.26, 12.34) * mm});
            skLineSegment(sketch, "E979", {"start": v(-7.26, 12.34) * mm, "end": v(-7.26, 12.45) * mm});
            skLineSegment(sketch, "E980", {"start": v(-7.26, 12.45) * mm, "end": v(-7.32, 12.45) * mm});
            skLineSegment(sketch, "E981", {"start": v(-7.32, 12.45) * mm, "end": v(-7.32, 12.56) * mm});
            skLineSegment(sketch, "E982", {"start": v(-7.32, 12.56) * mm, "end": v(-7.38, 12.67) * mm});
            skLineSegment(sketch, "E983", {"start": v(-7.38, 12.67) * mm, "end": v(-7.49, 12.73) * mm});
            skLineSegment(sketch, "E984", {"start": v(-7.49, 12.73) * mm, "end": v(-7.49, 12.84) * mm});
            skLineSegment(sketch, "E985", {"start": v(-7.49, 12.84) * mm, "end": v(-7.6, 12.9) * mm});
            skLineSegment(sketch, "E986", {"start": v(-7.6, 12.9) * mm, "end": v(-7.6, 13) * mm});
            skLineSegment(sketch, "E987", {"start": v(-7.6, 13) * mm, "end": v(-7.65, 13) * mm});
            skLineSegment(sketch, "E988", {"start": v(-7.65, 13) * mm, "end": v(-7.65, 13.11) * mm});
            skLineSegment(sketch, "E989", {"start": v(-7.65, 13.11) * mm, "end": v(-7.7, 13.23) * mm});
            skLineSegment(sketch, "E990", {"start": v(-7.7, 13.23) * mm, "end": v(-7.82, 13.28) * mm});
            skLineSegment(sketch, "E991", {"start": v(-7.82, 13.28) * mm, "end": v(-7.82, 13.4) * mm});
            skLineSegment(sketch, "E992", {"start": v(-7.82, 13.4) * mm, "end": v(-7.93, 13.45) * mm});
            skLineSegment(sketch, "E993", {"start": v(-7.93, 13.45) * mm, "end": v(-7.93, 13.56) * mm});
            skLineSegment(sketch, "E994", {"start": v(-7.93, 13.56) * mm, "end": v(-7.99, 13.56) * mm});
            skLineSegment(sketch, "E995", {"start": v(-7.99, 13.56) * mm, "end": v(-7.99, 13.67) * mm});
            skLineSegment(sketch, "E996", {"start": v(-7.99, 13.67) * mm, "end": v(-8.04, 13.78) * mm});
            skLineSegment(sketch, "E997", {"start": v(-8.04, 13.78) * mm, "end": v(-8.15, 13.84) * mm});
            skLineSegment(sketch, "E998", {"start": v(-8.15, 13.84) * mm, "end": v(-8.15, 13.95) * mm});
            skLineSegment(sketch, "E999", {"start": v(-8.15, 13.95) * mm, "end": v(-8.26, 14) * mm});
            skLineSegment(sketch, "E1000", {"start": v(-8.26, 14) * mm, "end": v(-8.32, 14.22) * mm});
            skLineSegment(sketch, "E1001", {"start": v(-8.32, 14.22) * mm, "end": v(-8.43, 14.28) * mm});
            skLineSegment(sketch, "E1002", {"start": v(-8.43, 14.28) * mm, "end": v(-8.48, 14.5) * mm});
            skLineSegment(sketch, "E1003", {"start": v(-8.48, 14.5) * mm, "end": v(-8.65, 14.67) * mm});
            skLineSegment(sketch, "E1004", {"start": v(-8.65, 14.67) * mm, "end": v(-8.82, 14.72) * mm});
            skLineSegment(sketch, "E1005", {"start": v(-8.82, 14.72) * mm, "end": v(-9.2, 14.72) * mm});
            skLineSegment(sketch, "E1006", {"start": v(-0.39, 3.13) * mm, "end": v(-0.39, 3.08) * mm});
            skLineSegment(sketch, "E1007", {"start": v(-0.39, 3.08) * mm, "end": v(-0.78, 3.08) * mm});
            skLineSegment(sketch, "E1008", {"start": v(-0.78, 3.08) * mm, "end": v(-0.94, 2.97) * mm});
            skLineSegment(sketch, "E1009", {"start": v(-0.94, 2.97) * mm, "end": v(-1.16, 2.97) * mm});
            skLineSegment(sketch, "E1010", {"start": v(-1.16, 2.97) * mm, "end": v(-1.28, 2.86) * mm});
            skLineSegment(sketch, "E1011", {"start": v(-1.28, 2.86) * mm, "end": v(-1.39, 2.86) * mm});
            skLineSegment(sketch, "E1012", {"start": v(-1.39, 2.86) * mm, "end": v(-1.39, 2.8) * mm});
            skLineSegment(sketch, "E1013", {"start": v(-1.39, 2.8) * mm, "end": v(-1.5, 2.8) * mm});
            skLineSegment(sketch, "E1014", {"start": v(-1.5, 2.8) * mm, "end": v(-1.55, 2.69) * mm});
            skLineSegment(sketch, "E1015", {"start": v(-1.55, 2.69) * mm, "end": v(-1.77, 2.63) * mm});
            skLineSegment(sketch, "E1016", {"start": v(-1.77, 2.63) * mm, "end": v(-1.89, 2.47) * mm});
            skLineSegment(sketch, "E1017", {"start": v(-1.89, 2.47) * mm, "end": v(-2, 2.47) * mm});
            skLineSegment(sketch, "E1018", {"start": v(-2, 2.47) * mm, "end": v(-2.05, 2.41) * mm});
            skLineSegment(sketch, "E1019", {"start": v(-2.05, 2.41) * mm, "end": v(-2.1, 2.3) * mm});
            skLineSegment(sketch, "E1020", {"start": v(-2.1, 2.3) * mm, "end": v(-2.27, 2.25) * mm});
            skLineSegment(sketch, "E1021", {"start": v(-2.27, 2.25) * mm, "end": v(-2.33, 2.08) * mm});
            skLineSegment(sketch, "E1022", {"start": v(-2.33, 2.08) * mm, "end": v(-2.44, 2.02) * mm});
            skLineSegment(sketch, "E1023", {"start": v(-2.44, 2.02) * mm, "end": v(-2.5, 1.97) * mm});
            skLineSegment(sketch, "E1024", {"start": v(-2.5, 1.97) * mm, "end": v(-2.5, 1.86) * mm});
            skLineSegment(sketch, "E1025", {"start": v(-2.5, 1.86) * mm, "end": v(-2.55, 1.8) * mm});
            skLineSegment(sketch, "E1026", {"start": v(-2.55, 1.8) * mm, "end": v(-2.66, 1.75) * mm});
            skLineSegment(sketch, "E1027", {"start": v(-2.66, 1.75) * mm, "end": v(-2.72, 1.7) * mm});
            skLineSegment(sketch, "E1028", {"start": v(-2.72, 1.7) * mm, "end": v(-2.77, 1.41) * mm});
            skLineSegment(sketch, "E1029", {"start": v(-2.77, 1.41) * mm, "end": v(-2.88, 1.25) * mm});
            skLineSegment(sketch, "E1030", {"start": v(-2.88, 1.25) * mm, "end": v(-2.94, 1.25) * mm});
            skLineSegment(sketch, "E1031", {"start": v(-2.94, 1.25) * mm, "end": v(-3, 1.14) * mm});
            skLineSegment(sketch, "E1032", {"start": v(-3, 1.14) * mm, "end": v(-3.05, 0.97) * mm});
            skLineSegment(sketch, "E1033", {"start": v(-3.05, 0.97) * mm, "end": v(-3.05, 0.75) * mm});
            skLineSegment(sketch, "E1034", {"start": v(-3.05, 0.75) * mm, "end": v(-3.1, 0.75) * mm});
            skLineSegment(sketch, "E1035", {"start": v(-3.1, 0.75) * mm, "end": v(-3.1, 0.47) * mm});
            skLineSegment(sketch, "E1036", {"start": v(-3.1, 0.47) * mm, "end": v(-3.16, 0.47) * mm});
            skLineSegment(sketch, "E1037", {"start": v(-3.16, 0.47) * mm, "end": v(-3.16, 0.3) * mm});
            skLineSegment(sketch, "E1038", {"start": v(-3.16, 0.3) * mm, "end": v(-3.16, 0.08) * mm});
            skLineSegment(sketch, "E1039", {"start": v(-3.16, 0.08) * mm, "end": v(-3.16, 0.03) * mm});
            skLineSegment(sketch, "E1040", {"start": v(-3.16, 0.03) * mm, "end": v(-3.16, -0.03) * mm});
            skLineSegment(sketch, "E1041", {"start": v(-3.16, -0.03) * mm, "end": v(-3.16, -0.08) * mm});
            skLineSegment(sketch, "E1042", {"start": v(-3.16, -0.08) * mm, "end": v(-3.16, -0.14) * mm});
            skLineSegment(sketch, "E1043", {"start": v(-3.16, -0.14) * mm, "end": v(-3.16, -0.2) * mm});
            skLineSegment(sketch, "E1044", {"start": v(-3.16, -0.2) * mm, "end": v(-3.16, -0.25) * mm});
            skLineSegment(sketch, "E1045", {"start": v(-3.16, -0.25) * mm, "end": v(-3.16, -0.3) * mm});
            skLineSegment(sketch, "E1046", {"start": v(-3.16, -0.3) * mm, "end": v(-3.16, -0.53) * mm});
            skLineSegment(sketch, "E1047", {"start": v(-3.16, -0.53) * mm, "end": v(-3.1, -0.53) * mm});
            skLineSegment(sketch, "E1048", {"start": v(-3.1, -0.53) * mm, "end": v(-3.1, -0.8) * mm});
            skLineSegment(sketch, "E1049", {"start": v(-3.1, -0.8) * mm, "end": v(-3.05, -0.8) * mm});
            skLineSegment(sketch, "E1050", {"start": v(-3.05, -0.8) * mm, "end": v(-3.05, -1.03) * mm});
            skLineSegment(sketch, "E1051", {"start": v(-3.05, -1.03) * mm, "end": v(-3, -1.2) * mm});
            skLineSegment(sketch, "E1052", {"start": v(-3, -1.2) * mm, "end": v(-2.88, -1.3) * mm});
            skLineSegment(sketch, "E1053", {"start": v(-2.88, -1.3) * mm, "end": v(-2.88, -1.41) * mm});
            skLineSegment(sketch, "E1054", {"start": v(-2.88, -1.41) * mm, "end": v(-2.83, -1.41) * mm});
            skLineSegment(sketch, "E1055", {"start": v(-2.83, -1.41) * mm, "end": v(-2.83, -1.52) * mm});
            skLineSegment(sketch, "E1056", {"start": v(-2.83, -1.52) * mm, "end": v(-2.77, -1.52) * mm});
            skLineSegment(sketch, "E1057", {"start": v(-2.77, -1.52) * mm, "end": v(-2.77, -1.64) * mm});
            skLineSegment(sketch, "E1058", {"start": v(-2.77, -1.64) * mm, "end": v(-2.72, -1.75) * mm});
            skLineSegment(sketch, "E1059", {"start": v(-2.72, -1.75) * mm, "end": v(-2.6, -1.8) * mm});
            skLineSegment(sketch, "E1060", {"start": v(-2.6, -1.8) * mm, "end": v(-2.6, -1.91) * mm});
            skLineSegment(sketch, "E1061", {"start": v(-2.6, -1.91) * mm, "end": v(-2.38, -2.08) * mm});
            skLineSegment(sketch, "E1062", {"start": v(-2.38, -2.08) * mm, "end": v(-2.38, -2.2) * mm});
            skLineSegment(sketch, "E1063", {"start": v(-2.38, -2.2) * mm, "end": v(-2.33, -2.25) * mm});
            skLineSegment(sketch, "E1064", {"start": v(-2.33, -2.25) * mm, "end": v(-2.27, -2.3) * mm});
            skLineSegment(sketch, "E1065", {"start": v(-2.27, -2.3) * mm, "end": v(-2.22, -2.36) * mm});
            skLineSegment(sketch, "E1066", {"start": v(-2.22, -2.36) * mm, "end": v(-2.1, -2.36) * mm});
            skLineSegment(sketch, "E1067", {"start": v(-2.1, -2.36) * mm, "end": v(-2.05, -2.41) * mm});
            skLineSegment(sketch, "E1068", {"start": v(-2.05, -2.41) * mm, "end": v(-2, -2.52) * mm});
            skLineSegment(sketch, "E1069", {"start": v(-2, -2.52) * mm, "end": v(-1.83, -2.58) * mm});
            skLineSegment(sketch, "E1070", {"start": v(-1.83, -2.58) * mm, "end": v(-1.83, -2.69) * mm});
            skLineSegment(sketch, "E1071", {"start": v(-1.83, -2.69) * mm, "end": v(-1.72, -2.74) * mm});
            skLineSegment(sketch, "E1072", {"start": v(-1.72, -2.74) * mm, "end": v(-1.6, -2.74) * mm});
            skLineSegment(sketch, "E1073", {"start": v(-1.6, -2.74) * mm, "end": v(-1.6, -2.8) * mm});
            skLineSegment(sketch, "E1074", {"start": v(-1.6, -2.8) * mm, "end": v(-1.5, -2.8) * mm});
            skLineSegment(sketch, "E1075", {"start": v(-1.5, -2.8) * mm, "end": v(-1.5, -2.86) * mm});
            skLineSegment(sketch, "E1076", {"start": v(-1.5, -2.86) * mm, "end": v(-1.39, -2.86) * mm});
            skLineSegment(sketch, "E1077", {"start": v(-1.39, -2.86) * mm, "end": v(-1.28, -2.97) * mm});
            skLineSegment(sketch, "E1078", {"start": v(-1.28, -2.97) * mm, "end": v(-1.1, -2.97) * mm});
            skLineSegment(sketch, "E1079", {"start": v(-1.1, -2.97) * mm, "end": v(-1, -3.08) * mm});
            skLineSegment(sketch, "E1080", {"start": v(-1, -3.08) * mm, "end": v(-0.83, -3.13) * mm});
            skLineSegment(sketch, "E1081", {"start": v(-0.83, -3.13) * mm, "end": v(-0.5, -3.13) * mm});
            skLineSegment(sketch, "E1082", {"start": v(-0.5, -3.13) * mm, "end": v(-0.5, -3.19) * mm});
            skLineSegment(sketch, "E1083", {"start": v(-0.5, -3.19) * mm, "end": v(-0.33, -3.19) * mm});
            skLineSegment(sketch, "E1084", {"start": v(-0.33, -3.19) * mm, "end": v(-0.11, -3.19) * mm});
            skLineSegment(sketch, "E1085", {"start": v(-0.11, -3.19) * mm, "end": v(-0.06, -3.19) * mm});
            skLineSegment(sketch, "E1086", {"start": v(-0.06, -3.19) * mm, "end": v(0, -3.19) * mm});
            skLineSegment(sketch, "E1087", {"start": v(0, -3.19) * mm, "end": v(0.06, -3.19) * mm});
            skLineSegment(sketch, "E1088", {"start": v(0.06, -3.19) * mm, "end": v(0.11, -3.19) * mm});
            skLineSegment(sketch, "E1089", {"start": v(0.11, -3.19) * mm, "end": v(0.17, -3.19) * mm});
            skLineSegment(sketch, "E1090", {"start": v(0.17, -3.19) * mm, "end": v(0.22, -3.19) * mm});
            skLineSegment(sketch, "E1091", {"start": v(0.22, -3.19) * mm, "end": v(0.28, -3.19) * mm});
            skLineSegment(sketch, "E1092", {"start": v(0.28, -3.19) * mm, "end": v(0.5, -3.19) * mm});
            skLineSegment(sketch, "E1093", {"start": v(0.5, -3.19) * mm, "end": v(0.5, -3.13) * mm});
            skLineSegment(sketch, "E1094", {"start": v(0.5, -3.13) * mm, "end": v(0.83, -3.13) * mm});
            skLineSegment(sketch, "E1095", {"start": v(0.83, -3.13) * mm, "end": v(1, -3.08) * mm});
            skLineSegment(sketch, "E1096", {"start": v(1, -3.08) * mm, "end": v(1.1, -2.97) * mm});
            skLineSegment(sketch, "E1097", {"start": v(1.1, -2.97) * mm, "end": v(1.28, -2.97) * mm});
            skLineSegment(sketch, "E1098", {"start": v(1.28, -2.97) * mm, "end": v(1.39, -2.91) * mm});
            skLineSegment(sketch, "E1099", {"start": v(1.39, -2.91) * mm, "end": v(1.39, -2.86) * mm});
            skLineSegment(sketch, "E1100", {"start": v(1.39, -2.86) * mm, "end": v(1.5, -2.86) * mm});
            skLineSegment(sketch, "E1101", {"start": v(1.5, -2.86) * mm, "end": v(1.5, -2.8) * mm});
            skLineSegment(sketch, "E1102", {"start": v(1.5, -2.8) * mm, "end": v(1.6, -2.8) * mm});
            skLineSegment(sketch, "E1103", {"start": v(1.6, -2.8) * mm, "end": v(1.6, -2.74) * mm});
            skLineSegment(sketch, "E1104", {"start": v(1.6, -2.74) * mm, "end": v(1.83, -2.69) * mm});
            skLineSegment(sketch, "E1105", {"start": v(1.83, -2.69) * mm, "end": v(1.83, -2.58) * mm});
            skLineSegment(sketch, "E1106", {"start": v(1.83, -2.58) * mm, "end": v(1.94, -2.58) * mm});
            skLineSegment(sketch, "E1107", {"start": v(1.94, -2.58) * mm, "end": v(2, -2.52) * mm});
            skLineSegment(sketch, "E1108", {"start": v(2, -2.52) * mm, "end": v(2.1, -2.36) * mm});
            skLineSegment(sketch, "E1109", {"start": v(2.1, -2.36) * mm, "end": v(2.22, -2.36) * mm});
            skLineSegment(sketch, "E1110", {"start": v(2.22, -2.36) * mm, "end": v(2.27, -2.3) * mm});
            skLineSegment(sketch, "E1111", {"start": v(2.27, -2.3) * mm, "end": v(2.33, -2.25) * mm});
            skLineSegment(sketch, "E1112", {"start": v(2.33, -2.25) * mm, "end": v(2.38, -2.2) * mm});
            skLineSegment(sketch, "E1113", {"start": v(2.38, -2.2) * mm, "end": v(2.38, -2.08) * mm});
            skLineSegment(sketch, "E1114", {"start": v(2.38, -2.08) * mm, "end": v(2.44, -2.02) * mm});
            skLineSegment(sketch, "E1115", {"start": v(2.44, -2.02) * mm, "end": v(2.55, -1.97) * mm});
            skLineSegment(sketch, "E1116", {"start": v(2.55, -1.97) * mm, "end": v(2.6, -1.91) * mm});
            skLineSegment(sketch, "E1117", {"start": v(2.6, -1.91) * mm, "end": v(2.6, -1.8) * mm});
            skLineSegment(sketch, "E1118", {"start": v(2.6, -1.8) * mm, "end": v(2.72, -1.75) * mm});
            skLineSegment(sketch, "E1119", {"start": v(2.72, -1.75) * mm, "end": v(2.77, -1.52) * mm});
            skLineSegment(sketch, "E1120", {"start": v(2.77, -1.52) * mm, "end": v(2.83, -1.52) * mm});
            skLineSegment(sketch, "E1121", {"start": v(2.83, -1.52) * mm, "end": v(2.83, -1.41) * mm});
            skLineSegment(sketch, "E1122", {"start": v(2.83, -1.41) * mm, "end": v(2.88, -1.41) * mm});
            skLineSegment(sketch, "E1123", {"start": v(2.88, -1.41) * mm, "end": v(2.88, -1.3) * mm});
            skLineSegment(sketch, "E1124", {"start": v(2.88, -1.3) * mm, "end": v(2.94, -1.3) * mm});
            skLineSegment(sketch, "E1125", {"start": v(2.94, -1.3) * mm, "end": v(3, -1.2) * mm});
            skLineSegment(sketch, "E1126", {"start": v(3, -1.2) * mm, "end": v(3.05, -1.03) * mm});
            skLineSegment(sketch, "E1127", {"start": v(3.05, -1.03) * mm, "end": v(3.05, -0.8) * mm});
            skLineSegment(sketch, "E1128", {"start": v(3.05, -0.8) * mm, "end": v(3.1, -0.8) * mm});
            skLineSegment(sketch, "E1129", {"start": v(3.1, -0.8) * mm, "end": v(3.1, -0.53) * mm});
            skLineSegment(sketch, "E1130", {"start": v(3.1, -0.53) * mm, "end": v(3.16, -0.53) * mm});
            skLineSegment(sketch, "E1131", {"start": v(3.16, -0.53) * mm, "end": v(3.16, -0.36) * mm});
            skLineSegment(sketch, "E1132", {"start": v(3.16, -0.36) * mm, "end": v(3.16, -0.14) * mm});
            skLineSegment(sketch, "E1133", {"start": v(3.16, -0.14) * mm, "end": v(3.16, -0.08) * mm});
            skLineSegment(sketch, "E1134", {"start": v(3.16, -0.08) * mm, "end": v(3.16, -0.03) * mm});
            skLineSegment(sketch, "E1135", {"start": v(3.16, -0.03) * mm, "end": v(3.16, 0.03) * mm});
            skLineSegment(sketch, "E1136", {"start": v(3.16, 0.03) * mm, "end": v(3.16, 0.08) * mm});
            skLineSegment(sketch, "E1137", {"start": v(3.16, 0.08) * mm, "end": v(3.16, 0.14) * mm});
            skLineSegment(sketch, "E1138", {"start": v(3.16, 0.14) * mm, "end": v(3.16, 0.2) * mm});
            skLineSegment(sketch, "E1139", {"start": v(3.16, 0.2) * mm, "end": v(3.16, 0.25) * mm});
            skLineSegment(sketch, "E1140", {"start": v(3.16, 0.25) * mm, "end": v(3.16, 0.47) * mm});
            skLineSegment(sketch, "E1141", {"start": v(3.16, 0.47) * mm, "end": v(3.1, 0.47) * mm});
            skLineSegment(sketch, "E1142", {"start": v(3.1, 0.47) * mm, "end": v(3.1, 0.75) * mm});
            skLineSegment(sketch, "E1143", {"start": v(3.1, 0.75) * mm, "end": v(3.05, 0.75) * mm});
            skLineSegment(sketch, "E1144", {"start": v(3.05, 0.75) * mm, "end": v(3.05, 0.97) * mm});
            skLineSegment(sketch, "E1145", {"start": v(3.05, 0.97) * mm, "end": v(3, 1.14) * mm});
            skLineSegment(sketch, "E1146", {"start": v(3, 1.14) * mm, "end": v(2.77, 1.41) * mm});
            skLineSegment(sketch, "E1147", {"start": v(2.77, 1.41) * mm, "end": v(2.72, 1.7) * mm});
            skLineSegment(sketch, "E1148", {"start": v(2.72, 1.7) * mm, "end": v(2.5, 1.86) * mm});
            skLineSegment(sketch, "E1149", {"start": v(2.5, 1.86) * mm, "end": v(2.5, 1.97) * mm});
            skLineSegment(sketch, "E1150", {"start": v(2.5, 1.97) * mm, "end": v(2.44, 2.02) * mm});
            skLineSegment(sketch, "E1151", {"start": v(2.44, 2.02) * mm, "end": v(2.33, 2.08) * mm});
            skLineSegment(sketch, "E1152", {"start": v(2.33, 2.08) * mm, "end": v(2.27, 2.25) * mm});
            skLineSegment(sketch, "E1153", {"start": v(2.27, 2.25) * mm, "end": v(2.1, 2.3) * mm});
            skLineSegment(sketch, "E1154", {"start": v(2.1, 2.3) * mm, "end": v(2.05, 2.41) * mm});
            skLineSegment(sketch, "E1155", {"start": v(2.05, 2.41) * mm, "end": v(2, 2.47) * mm});
            skLineSegment(sketch, "E1156", {"start": v(2, 2.47) * mm, "end": v(1.89, 2.47) * mm});
            skLineSegment(sketch, "E1157", {"start": v(1.89, 2.47) * mm, "end": v(1.77, 2.63) * mm});
            skLineSegment(sketch, "E1158", {"start": v(1.77, 2.63) * mm, "end": v(1.55, 2.69) * mm});
            skLineSegment(sketch, "E1159", {"start": v(1.55, 2.69) * mm, "end": v(1.5, 2.8) * mm});
            skLineSegment(sketch, "E1160", {"start": v(1.5, 2.8) * mm, "end": v(1.39, 2.8) * mm});
            skLineSegment(sketch, "E1161", {"start": v(1.39, 2.8) * mm, "end": v(1.39, 2.86) * mm});
            skLineSegment(sketch, "E1162", {"start": v(1.39, 2.86) * mm, "end": v(1.28, 2.86) * mm});
            skLineSegment(sketch, "E1163", {"start": v(1.28, 2.86) * mm, "end": v(1.16, 2.97) * mm});
            skLineSegment(sketch, "E1164", {"start": v(1.16, 2.97) * mm, "end": v(0.94, 2.97) * mm});
            skLineSegment(sketch, "E1165", {"start": v(0.94, 2.97) * mm, "end": v(0.78, 3.08) * mm});
            skLineSegment(sketch, "E1166", {"start": v(0.78, 3.08) * mm, "end": v(0.33, 3.08) * mm});
            skLineSegment(sketch, "E1167", {"start": v(0.33, 3.08) * mm, "end": v(0.33, 3.13) * mm});
            skLineSegment(sketch, "E1168", {"start": v(0.33, 3.13) * mm, "end": v(0.17, 3.13) * mm});
            skLineSegment(sketch, "E1169", {"start": v(0.17, 3.13) * mm, "end": v(-0.39, 3.13) * mm});
            skLineSegment(sketch, "E1170", {"start": v(-0.28, 1.7) * mm, "end": v(-0.28, 1.64) * mm});
            skLineSegment(sketch, "E1171", {"start": v(-0.28, 1.64) * mm, "end": v(-0.5, 1.64) * mm});
            skLineSegment(sketch, "E1172", {"start": v(-0.5, 1.64) * mm, "end": v(-0.67, 1.58) * mm});
            skLineSegment(sketch, "E1173", {"start": v(-0.67, 1.58) * mm, "end": v(-0.78, 1.47) * mm});
            skLineSegment(sketch, "E1174", {"start": v(-0.78, 1.47) * mm, "end": v(-0.89, 1.47) * mm});
            skLineSegment(sketch, "E1175", {"start": v(-0.89, 1.47) * mm, "end": v(-0.89, 1.41) * mm});
            skLineSegment(sketch, "E1176", {"start": v(-0.89, 1.41) * mm, "end": v(-1, 1.41) * mm});
            skLineSegment(sketch, "E1177", {"start": v(-1, 1.41) * mm, "end": v(-1.1, 1.3) * mm});
            skLineSegment(sketch, "E1178", {"start": v(-1.1, 1.3) * mm, "end": v(-1.1, 1.25) * mm});
            skLineSegment(sketch, "E1179", {"start": v(-1.1, 1.25) * mm, "end": v(-1.16, 1.25) * mm});
            skLineSegment(sketch, "E1180", {"start": v(-1.16, 1.25) * mm, "end": v(-1.16, 1.2) * mm});
            skLineSegment(sketch, "E1181", {"start": v(-1.16, 1.2) * mm, "end": v(-1.22, 1.2) * mm});
            skLineSegment(sketch, "E1182", {"start": v(-1.22, 1.2) * mm, "end": v(-1.22, 1.14) * mm});
            skLineSegment(sketch, "E1183", {"start": v(-1.22, 1.14) * mm, "end": v(-1.28, 1.14) * mm});
            skLineSegment(sketch, "E1184", {"start": v(-1.28, 1.14) * mm, "end": v(-1.28, 1.08) * mm});
            skLineSegment(sketch, "E1185", {"start": v(-1.28, 1.08) * mm, "end": v(-1.44, 0.97) * mm});
            skLineSegment(sketch, "E1186", {"start": v(-1.44, 0.97) * mm, "end": v(-1.5, 0.75) * mm});
            skLineSegment(sketch, "E1187", {"start": v(-1.5, 0.75) * mm, "end": v(-1.55, 0.75) * mm});
            skLineSegment(sketch, "E1188", {"start": v(-1.55, 0.75) * mm, "end": v(-1.6, 0.64) * mm});
            skLineSegment(sketch, "E1189", {"start": v(-1.6, 0.64) * mm, "end": v(-1.66, 0.47) * mm});
            skLineSegment(sketch, "E1190", {"start": v(-1.66, 0.47) * mm, "end": v(-1.66, 0.3) * mm});
            skLineSegment(sketch, "E1191", {"start": v(-1.66, 0.3) * mm, "end": v(-1.72, 0.3) * mm});
            skLineSegment(sketch, "E1192", {"start": v(-1.72, 0.3) * mm, "end": v(-1.72, 0.08) * mm});
            skLineSegment(sketch, "E1193", {"start": v(-1.72, 0.08) * mm, "end": v(-1.72, 0.03) * mm});
            skLineSegment(sketch, "E1194", {"start": v(-1.72, 0.03) * mm, "end": v(-1.72, -0.03) * mm});
            skLineSegment(sketch, "E1195", {"start": v(-1.72, -0.03) * mm, "end": v(-1.72, -0.08) * mm});
            skLineSegment(sketch, "E1196", {"start": v(-1.72, -0.08) * mm, "end": v(-1.72, -0.36) * mm});
            skLineSegment(sketch, "E1197", {"start": v(-1.72, -0.36) * mm, "end": v(-1.66, -0.53) * mm});
            skLineSegment(sketch, "E1198", {"start": v(-1.66, -0.53) * mm, "end": v(-1.6, -0.53) * mm});
            skLineSegment(sketch, "E1199", {"start": v(-1.6, -0.53) * mm, "end": v(-1.6, -0.7) * mm});
            skLineSegment(sketch, "E1200", {"start": v(-1.6, -0.7) * mm, "end": v(-1.5, -0.91) * mm});
            skLineSegment(sketch, "E1201", {"start": v(-1.5, -0.91) * mm, "end": v(-1.39, -0.97) * mm});
            skLineSegment(sketch, "E1202", {"start": v(-1.39, -0.97) * mm, "end": v(-1.39, -1.08) * mm});
            skLineSegment(sketch, "E1203", {"start": v(-1.39, -1.08) * mm, "end": v(-1.22, -1.3) * mm});
            skLineSegment(sketch, "E1204", {"start": v(-1.22, -1.3) * mm, "end": v(-1.05, -1.41) * mm});
            skLineSegment(sketch, "E1205", {"start": v(-1.05, -1.41) * mm, "end": v(-0.94, -1.41) * mm});
            skLineSegment(sketch, "E1206", {"start": v(-0.94, -1.41) * mm, "end": v(-0.89, -1.52) * mm});
            skLineSegment(sketch, "E1207", {"start": v(-0.89, -1.52) * mm, "end": v(-0.67, -1.64) * mm});
            skLineSegment(sketch, "E1208", {"start": v(-0.67, -1.64) * mm, "end": v(-0.5, -1.7) * mm});
            skLineSegment(sketch, "E1209", {"start": v(-0.5, -1.7) * mm, "end": v(-0.33, -1.7) * mm});
            skLineSegment(sketch, "E1210", {"start": v(-0.33, -1.7) * mm, "end": v(-0.33, -1.75) * mm});
            skLineSegment(sketch, "E1211", {"start": v(-0.33, -1.75) * mm, "end": v(-0.11, -1.75) * mm});
            skLineSegment(sketch, "E1212", {"start": v(-0.11, -1.75) * mm, "end": v(-0.06, -1.75) * mm});
            skLineSegment(sketch, "E1213", {"start": v(-0.03, -1.75) * mm, "end": v(0.03, -1.75) * mm});
            skLineSegment(sketch, "E1214", {"start": v(0, -1.75) * mm, "end": v(0.08, -1.75) * mm});
            skLineSegment(sketch, "E1215", {"start": v(0.08, -1.75) * mm, "end": v(0.3, -1.75) * mm});
            skLineSegment(sketch, "E1216", {"start": v(0.3, -1.75) * mm, "end": v(0.28, -1.7) * mm});
            skLineSegment(sketch, "E1217", {"start": v(0.28, -1.7) * mm, "end": v(0.5, -1.7) * mm});
            skLineSegment(sketch, "E1218", {"start": v(0.5, -1.7) * mm, "end": v(0.67, -1.64) * mm});
            skLineSegment(sketch, "E1219", {"start": v(0.67, -1.64) * mm, "end": v(0.89, -1.52) * mm});
            skLineSegment(sketch, "E1220", {"start": v(0.89, -1.52) * mm, "end": v(0.94, -1.41) * mm});
            skLineSegment(sketch, "E1221", {"start": v(0.94, -1.41) * mm, "end": v(1.05, -1.41) * mm});
            skLineSegment(sketch, "E1222", {"start": v(1.05, -1.41) * mm, "end": v(1.22, -1.3) * mm});
            skLineSegment(sketch, "E1223", {"start": v(1.22, -1.3) * mm, "end": v(1.39, -1.08) * mm});
            skLineSegment(sketch, "E1224", {"start": v(1.39, -1.08) * mm, "end": v(1.39, -0.97) * mm});
            skLineSegment(sketch, "E1225", {"start": v(1.39, -0.97) * mm, "end": v(1.5, -0.91) * mm});
            skLineSegment(sketch, "E1226", {"start": v(1.5, -0.91) * mm, "end": v(1.6, -0.7) * mm});
            skLineSegment(sketch, "E1227", {"start": v(1.6, -0.7) * mm, "end": v(1.66, -0.53) * mm});
            skLineSegment(sketch, "E1228", {"start": v(1.66, -0.53) * mm, "end": v(1.66, -0.36) * mm});
            skLineSegment(sketch, "E1229", {"start": v(1.66, -0.36) * mm, "end": v(1.72, -0.36) * mm});
            skLineSegment(sketch, "E1230", {"start": v(1.72, -0.36) * mm, "end": v(1.72, -0.14) * mm});
            skLineSegment(sketch, "E1231", {"start": v(1.72, -0.14) * mm, "end": v(1.72, -0.08) * mm});
            skLineSegment(sketch, "E1232", {"start": v(1.72, -0.08) * mm, "end": v(1.72, -0.03) * mm});
            skLineSegment(sketch, "E1233", {"start": v(1.72, -0.06) * mm, "end": v(1.72, 0) * mm});
            skLineSegment(sketch, "E1234", {"start": v(1.72, 0.03) * mm, "end": v(1.72, 0.3) * mm});
            skLineSegment(sketch, "E1235", {"start": v(1.72, 0.3) * mm, "end": v(1.66, 0.47) * mm});
            skLineSegment(sketch, "E1236", {"start": v(1.66, 0.47) * mm, "end": v(1.6, 0.47) * mm});
            skLineSegment(sketch, "E1237", {"start": v(1.6, 0.47) * mm, "end": v(1.6, 0.64) * mm});
            skLineSegment(sketch, "E1238", {"start": v(1.6, 0.64) * mm, "end": v(1.5, 0.75) * mm});
            skLineSegment(sketch, "E1239", {"start": v(1.5, 0.75) * mm, "end": v(1.5, 0.86) * mm});
            skLineSegment(sketch, "E1240", {"start": v(1.5, 0.86) * mm, "end": v(1.44, 0.86) * mm});
            skLineSegment(sketch, "E1241", {"start": v(1.44, 0.86) * mm, "end": v(1.44, 0.97) * mm});
            skLineSegment(sketch, "E1242", {"start": v(1.44, 0.97) * mm, "end": v(1.33, 1.08) * mm});
            skLineSegment(sketch, "E1243", {"start": v(1.33, 1.08) * mm, "end": v(1.28, 1.08) * mm});
            skLineSegment(sketch, "E1244", {"start": v(1.28, 1.08) * mm, "end": v(1.28, 1.14) * mm});
            skLineSegment(sketch, "E1245", {"start": v(1.28, 1.14) * mm, "end": v(1.22, 1.14) * mm});
            skLineSegment(sketch, "E1246", {"start": v(1.22, 1.14) * mm, "end": v(1.22, 1.2) * mm});
            skLineSegment(sketch, "E1247", {"start": v(1.22, 1.2) * mm, "end": v(1.16, 1.2) * mm});
            skLineSegment(sketch, "E1248", {"start": v(1.16, 1.2) * mm, "end": v(1.16, 1.25) * mm});
            skLineSegment(sketch, "E1249", {"start": v(1.16, 1.25) * mm, "end": v(1.1, 1.25) * mm});
            skLineSegment(sketch, "E1250", {"start": v(1.1, 1.25) * mm, "end": v(1, 1.41) * mm});
            skLineSegment(sketch, "E1251", {"start": v(1, 1.41) * mm, "end": v(0.78, 1.47) * mm});
            skLineSegment(sketch, "E1252", {"start": v(0.78, 1.47) * mm, "end": v(0.78, 1.52) * mm});
            skLineSegment(sketch, "E1253", {"start": v(0.78, 1.52) * mm, "end": v(0.67, 1.58) * mm});
            skLineSegment(sketch, "E1254", {"start": v(0.67, 1.58) * mm, "end": v(0.5, 1.64) * mm});
            skLineSegment(sketch, "E1255", {"start": v(0.5, 1.64) * mm, "end": v(0.28, 1.64) * mm});
            skLineSegment(sketch, "E1256", {"start": v(0.28, 1.64) * mm, "end": v(0.28, 1.7) * mm});
            skLineSegment(sketch, "E1257", {"start": v(0.28, 1.7) * mm, "end": v(0.11, 1.7) * mm});
            skLineSegment(sketch, "E1258", {"start": v(0.11, 1.7) * mm, "end": v(-0.28, 1.7) * mm});
            skLineSegment(sketch, "E1259", {"start": v(-2.6, -4.74) * mm, "end": v(-2.88, -4.85) * mm});
            skLineSegment(sketch, "E1260", {"start": v(-2.88, -4.85) * mm, "end": v(-3.05, -5.02) * mm});
            skLineSegment(sketch, "E1261", {"start": v(-3.05, -5.02) * mm, "end": v(-3.05, -5.13) * mm});
            skLineSegment(sketch, "E1262", {"start": v(-3.05, -5.13) * mm, "end": v(-3.16, -5.18) * mm});
            skLineSegment(sketch, "E1263", {"start": v(-3.16, -5.18) * mm, "end": v(-3.22, -5.4) * mm});
            skLineSegment(sketch, "E1264", {"start": v(-3.22, -5.4) * mm, "end": v(-3.33, -5.46) * mm});
            skLineSegment(sketch, "E1265", {"start": v(-3.33, -5.46) * mm, "end": v(-3.33, -5.57) * mm});
            skLineSegment(sketch, "E1266", {"start": v(-3.33, -5.57) * mm, "end": v(-3.38, -5.57) * mm});
            skLineSegment(sketch, "E1267", {"start": v(-3.38, -5.57) * mm, "end": v(-3.38, -5.68) * mm});
            skLineSegment(sketch, "E1268", {"start": v(-3.38, -5.68) * mm, "end": v(-3.44, -5.8) * mm});
            skLineSegment(sketch, "E1269", {"start": v(-3.44, -5.8) * mm, "end": v(-3.55, -5.85) * mm});
            skLineSegment(sketch, "E1270", {"start": v(-3.55, -5.85) * mm, "end": v(-3.66, -6.02) * mm});
            skLineSegment(sketch, "E1271", {"start": v(-3.66, -6.02) * mm, "end": v(-3.66, -6.18) * mm});
            skLineSegment(sketch, "E1272", {"start": v(-3.66, -6.18) * mm, "end": v(-3.77, -6.24) * mm});
            skLineSegment(sketch, "E1273", {"start": v(-3.77, -6.24) * mm, "end": v(-3.77, -6.35) * mm});
            skLineSegment(sketch, "E1274", {"start": v(-3.77, -6.35) * mm, "end": v(-3.88, -6.4) * mm});
            skLineSegment(sketch, "E1275", {"start": v(-3.88, -6.4) * mm, "end": v(-4, -6.74) * mm});
            skLineSegment(sketch, "E1276", {"start": v(-4, -6.74) * mm, "end": v(-4.1, -6.8) * mm});
            skLineSegment(sketch, "E1277", {"start": v(-4.1, -6.8) * mm, "end": v(-4.16, -7.01) * mm});
            skLineSegment(sketch, "E1278", {"start": v(-4.16, -7.01) * mm, "end": v(-4.27, -7.07) * mm});
            skLineSegment(sketch, "E1279", {"start": v(-4.27, -7.07) * mm, "end": v(-4.27, -7.18) * mm});
            skLineSegment(sketch, "E1280", {"start": v(-4.27, -7.18) * mm, "end": v(-4.33, -7.18) * mm});
            skLineSegment(sketch, "E1281", {"start": v(-4.33, -7.18) * mm, "end": v(-4.33, -7.3) * mm});
            skLineSegment(sketch, "E1282", {"start": v(-4.33, -7.3) * mm, "end": v(-4.38, -7.4) * mm});
            skLineSegment(sketch, "E1283", {"start": v(-4.38, -7.4) * mm, "end": v(-4.5, -7.46) * mm});
            skLineSegment(sketch, "E1284", {"start": v(-4.5, -7.46) * mm, "end": v(-4.5, -7.57) * mm});
            skLineSegment(sketch, "E1285", {"start": v(-4.5, -7.57) * mm, "end": v(-4.55, -7.57) * mm});
            skLineSegment(sketch, "E1286", {"start": v(-4.55, -7.57) * mm, "end": v(-4.55, -7.68) * mm});
            skLineSegment(sketch, "E1287", {"start": v(-4.55, -7.68) * mm, "end": v(-4.6, -7.68) * mm});
            skLineSegment(sketch, "E1288", {"start": v(-4.6, -7.68) * mm, "end": v(-4.6, -7.8) * mm});
            skLineSegment(sketch, "E1289", {"start": v(-4.6, -7.8) * mm, "end": v(-4.66, -7.8) * mm});
            skLineSegment(sketch, "E1290", {"start": v(-4.66, -7.8) * mm, "end": v(-4.66, -7.9) * mm});
            skLineSegment(sketch, "E1291", {"start": v(-4.66, -7.9) * mm, "end": v(-4.82, -8.01) * mm});
            skLineSegment(sketch, "E1292", {"start": v(-4.82, -8.01) * mm, "end": v(-4.94, -8.35) * mm});
            skLineSegment(sketch, "E1293", {"start": v(-4.94, -8.35) * mm, "end": v(-5.05, -8.4) * mm});
            skLineSegment(sketch, "E1294", {"start": v(-5.05, -8.4) * mm, "end": v(-5.05, -8.51) * mm});
            skLineSegment(sketch, "E1295", {"start": v(-5.05, -8.51) * mm, "end": v(-5.1, -8.51) * mm});
            skLineSegment(sketch, "E1296", {"start": v(-5.1, -8.51) * mm, "end": v(-5.1, -8.62) * mm});
            skLineSegment(sketch, "E1297", {"start": v(-5.1, -8.62) * mm, "end": v(-5.16, -8.62) * mm});
            skLineSegment(sketch, "E1298", {"start": v(-5.16, -8.62) * mm, "end": v(-5.16, -8.73) * mm});
            skLineSegment(sketch, "E1299", {"start": v(-5.16, -8.73) * mm, "end": v(-5.21, -8.73) * mm});
            skLineSegment(sketch, "E1300", {"start": v(-5.21, -8.73) * mm, "end": v(-5.21, -8.84) * mm});
            skLineSegment(sketch, "E1301", {"start": v(-5.21, -8.84) * mm, "end": v(-5.32, -8.9) * mm});
            skLineSegment(sketch, "E1302", {"start": v(-5.32, -8.9) * mm, "end": v(-5.32, -9.01) * mm});
            skLineSegment(sketch, "E1303", {"start": v(-5.32, -9.01) * mm, "end": v(-5.43, -9.07) * mm});
            skLineSegment(sketch, "E1304", {"start": v(-5.43, -9.07) * mm, "end": v(-5.43, -9.18) * mm});
            skLineSegment(sketch, "E1305", {"start": v(-5.43, -9.18) * mm, "end": v(-5.49, -9.18) * mm});
            skLineSegment(sketch, "E1306", {"start": v(-5.49, -9.18) * mm, "end": v(-5.49, -9.29) * mm});
            skLineSegment(sketch, "E1307", {"start": v(-5.49, -9.29) * mm, "end": v(-5.55, -9.29) * mm});
            skLineSegment(sketch, "E1308", {"start": v(-5.55, -9.29) * mm, "end": v(-5.55, -9.4) * mm});
            skLineSegment(sketch, "E1309", {"start": v(-5.55, -9.4) * mm, "end": v(-5.6, -9.4) * mm});
            skLineSegment(sketch, "E1310", {"start": v(-5.6, -9.4) * mm, "end": v(-5.6, -9.51) * mm});
            skLineSegment(sketch, "E1311", {"start": v(-5.6, -9.51) * mm, "end": v(-5.71, -9.57) * mm});
            skLineSegment(sketch, "E1312", {"start": v(-5.71, -9.57) * mm, "end": v(-5.77, -9.79) * mm});
            skLineSegment(sketch, "E1313", {"start": v(-5.77, -9.79) * mm, "end": v(-5.88, -9.84) * mm});
            skLineSegment(sketch, "E1314", {"start": v(-5.88, -9.84) * mm, "end": v(-5.93, -10.06) * mm});
            skLineSegment(sketch, "E1315", {"start": v(-5.93, -10.06) * mm, "end": v(-6.04, -10.12) * mm});
            skLineSegment(sketch, "E1316", {"start": v(-6.04, -10.12) * mm, "end": v(-6.04, -10.23) * mm});
            skLineSegment(sketch, "E1317", {"start": v(-6.04, -10.23) * mm, "end": v(-6.1, -10.23) * mm});
            skLineSegment(sketch, "E1318", {"start": v(-6.1, -10.23) * mm, "end": v(-6.1, -10.34) * mm});
            skLineSegment(sketch, "E1319", {"start": v(-6.1, -10.34) * mm, "end": v(-6.16, -10.45) * mm});
            skLineSegment(sketch, "E1320", {"start": v(-6.16, -10.45) * mm, "end": v(-6.27, -10.5) * mm});
            skLineSegment(sketch, "E1321", {"start": v(-6.27, -10.5) * mm, "end": v(-6.32, -10.73) * mm});
            skLineSegment(sketch, "E1322", {"start": v(-6.32, -10.73) * mm, "end": v(-6.43, -10.79) * mm});
            skLineSegment(sketch, "E1323", {"start": v(-6.43, -10.79) * mm, "end": v(-6.43, -10.9) * mm});
            skLineSegment(sketch, "E1324", {"start": v(-6.43, -10.9) * mm, "end": v(-6.49, -10.9) * mm});
            skLineSegment(sketch, "E1325", {"start": v(-6.49, -10.9) * mm, "end": v(-6.49, -11) * mm});
            skLineSegment(sketch, "E1326", {"start": v(-6.49, -11) * mm, "end": v(-6.54, -11.12) * mm});
            skLineSegment(sketch, "E1327", {"start": v(-6.54, -11.12) * mm, "end": v(-6.65, -11.17) * mm});
            skLineSegment(sketch, "E1328", {"start": v(-6.65, -11.17) * mm, "end": v(-6.65, -11.28) * mm});
            skLineSegment(sketch, "E1329", {"start": v(-6.65, -11.28) * mm, "end": v(-6.7, -11.28) * mm});
            skLineSegment(sketch, "E1330", {"start": v(-6.7, -11.28) * mm, "end": v(-6.7, -11.4) * mm});
            skLineSegment(sketch, "E1331", {"start": v(-6.7, -11.4) * mm, "end": v(-6.77, -11.4) * mm});
            skLineSegment(sketch, "E1332", {"start": v(-6.77, -11.4) * mm, "end": v(-6.77, -11.5) * mm});
            skLineSegment(sketch, "E1333", {"start": v(-6.77, -11.5) * mm, "end": v(-6.82, -11.5) * mm});
            skLineSegment(sketch, "E1334", {"start": v(-6.82, -11.5) * mm, "end": v(-6.82, -11.62) * mm});
            skLineSegment(sketch, "E1335", {"start": v(-6.82, -11.62) * mm, "end": v(-6.99, -11.73) * mm});
            skLineSegment(sketch, "E1336", {"start": v(-6.99, -11.73) * mm, "end": v(-7.1, -12.06) * mm});
            skLineSegment(sketch, "E1337", {"start": v(-7.1, -12.06) * mm, "end": v(-7.2, -12.12) * mm});
            skLineSegment(sketch, "E1338", {"start": v(-7.2, -12.12) * mm, "end": v(-7.2, -12.23) * mm});
            skLineSegment(sketch, "E1339", {"start": v(-7.2, -12.23) * mm, "end": v(-7.26, -12.23) * mm});
            skLineSegment(sketch, "E1340", {"start": v(-7.26, -12.23) * mm, "end": v(-7.26, -12.34) * mm});
            skLineSegment(sketch, "E1341", {"start": v(-7.26, -12.34) * mm, "end": v(-7.32, -12.45) * mm});
            skLineSegment(sketch, "E1342", {"start": v(-7.32, -12.45) * mm, "end": v(-7.43, -12.5) * mm});
            skLineSegment(sketch, "E1343", {"start": v(-7.43, -12.5) * mm, "end": v(-7.49, -12.73) * mm});
            skLineSegment(sketch, "E1344", {"start": v(-7.49, -12.73) * mm, "end": v(-7.6, -12.78) * mm});
            skLineSegment(sketch, "E1345", {"start": v(-7.6, -12.78) * mm, "end": v(-7.6, -12.9) * mm});
            skLineSegment(sketch, "E1346", {"start": v(-7.6, -12.9) * mm, "end": v(-7.65, -12.9) * mm});
            skLineSegment(sketch, "E1347", {"start": v(-7.65, -12.9) * mm, "end": v(-7.65, -13) * mm});
            skLineSegment(sketch, "E1348", {"start": v(-7.65, -13) * mm, "end": v(-7.7, -13.11) * mm});
            skLineSegment(sketch, "E1349", {"start": v(-7.7, -13.11) * mm, "end": v(-7.82, -13.17) * mm});
            skLineSegment(sketch, "E1350", {"start": v(-7.82, -13.17) * mm, "end": v(-7.82, -13.28) * mm});
            skLineSegment(sketch, "E1351", {"start": v(-7.82, -13.28) * mm, "end": v(-7.87, -13.28) * mm});
            skLineSegment(sketch, "E1352", {"start": v(-7.87, -13.28) * mm, "end": v(-7.87, -13.4) * mm});
            skLineSegment(sketch, "E1353", {"start": v(-7.87, -13.4) * mm, "end": v(-7.93, -13.5) * mm});
            skLineSegment(sketch, "E1354", {"start": v(-7.93, -13.5) * mm, "end": v(-8.04, -13.56) * mm});
            skLineSegment(sketch, "E1355", {"start": v(-8.04, -13.56) * mm, "end": v(-8.1, -13.78) * mm});
            skLineSegment(sketch, "E1356", {"start": v(-8.1, -13.78) * mm, "end": v(-8.2, -13.84) * mm});
            skLineSegment(sketch, "E1357", {"start": v(-8.2, -13.84) * mm, "end": v(-8.26, -14.06) * mm});
            skLineSegment(sketch, "E1358", {"start": v(-8.26, -14.06) * mm, "end": v(-8.37, -14.11) * mm});
            skLineSegment(sketch, "E1359", {"start": v(-8.37, -14.11) * mm, "end": v(-8.37, -14.22) * mm});
            skLineSegment(sketch, "E1360", {"start": v(-8.37, -14.22) * mm, "end": v(-8.43, -14.22) * mm});
            skLineSegment(sketch, "E1361", {"start": v(-8.43, -14.22) * mm, "end": v(-8.43, -14.33) * mm});
            skLineSegment(sketch, "E1362", {"start": v(-8.43, -14.33) * mm, "end": v(-8.48, -14.33) * mm});
            skLineSegment(sketch, "E1363", {"start": v(-8.48, -14.33) * mm, "end": v(-8.48, -14.45) * mm});
            skLineSegment(sketch, "E1364", {"start": v(-8.48, -14.45) * mm, "end": v(-8.54, -14.45) * mm});
            skLineSegment(sketch, "E1365", {"start": v(-8.54, -14.45) * mm, "end": v(-8.6, -14.56) * mm});
            skLineSegment(sketch, "E1366", {"start": v(-8.6, -14.56) * mm, "end": v(-8.65, -14.72) * mm});
            skLineSegment(sketch, "E1367", {"start": v(-8.65, -14.72) * mm, "end": v(-8.65, -14.78) * mm});
            skLineSegment(sketch, "E1368", {"start": v(-8.65, -14.78) * mm, "end": v(-8.6, -15) * mm});
            skLineSegment(sketch, "E1369", {"start": v(-8.6, -15) * mm, "end": v(-8.54, -15.17) * mm});
            skLineSegment(sketch, "E1370", {"start": v(-8.54, -15.17) * mm, "end": v(-8.37, -15.22) * mm});
            skLineSegment(sketch, "E1371", {"start": v(-8.37, -15.22) * mm, "end": v(-8.32, -15.33) * mm});
            skLineSegment(sketch, "E1372", {"start": v(-8.32, -15.33) * mm, "end": v(-8.2, -15.39) * mm});
            skLineSegment(sketch, "E1373", {"start": v(-8.2, -15.39) * mm, "end": v(-8.04, -15.39) * mm});
            skLineSegment(sketch, "E1374", {"start": v(-8.04, -15.39) * mm, "end": v(-7.93, -15.44) * mm});
            skLineSegment(sketch, "E1375", {"start": v(-7.93, -15.44) * mm, "end": v(-7.87, -15.55) * mm});
            skLineSegment(sketch, "E1376", {"start": v(-7.87, -15.55) * mm, "end": v(-7.76, -15.55) * mm});
            skLineSegment(sketch, "E1377", {"start": v(-7.76, -15.55) * mm, "end": v(-7.76, -15.6) * mm});
            skLineSegment(sketch, "E1378", {"start": v(-7.76, -15.6) * mm, "end": v(-7.65, -15.6) * mm});
            skLineSegment(sketch, "E1379", {"start": v(-7.65, -15.6) * mm, "end": v(-7.65, -15.67) * mm});
            skLineSegment(sketch, "E1380", {"start": v(-7.65, -15.67) * mm, "end": v(-7.54, -15.67) * mm});
            skLineSegment(sketch, "E1381", {"start": v(-7.54, -15.67) * mm, "end": v(-7.54, -15.72) * mm});
            skLineSegment(sketch, "E1382", {"start": v(-7.54, -15.72) * mm, "end": v(-7.43, -15.72) * mm});
            skLineSegment(sketch, "E1383", {"start": v(-7.43, -15.72) * mm, "end": v(-7.43, -15.78) * mm});
            skLineSegment(sketch, "E1384", {"start": v(-7.43, -15.78) * mm, "end": v(-7.32, -15.78) * mm});
            skLineSegment(sketch, "E1385", {"start": v(-7.32, -15.78) * mm, "end": v(-7.2, -15.89) * mm});
            skLineSegment(sketch, "E1386", {"start": v(-7.2, -15.89) * mm, "end": v(-7.04, -15.89) * mm});
            skLineSegment(sketch, "E1387", {"start": v(-7.04, -15.89) * mm, "end": v(-6.93, -16) * mm});
            skLineSegment(sketch, "E1388", {"start": v(-6.93, -16) * mm, "end": v(-6.77, -16) * mm});
            skLineSegment(sketch, "E1389", {"start": v(-6.77, -16) * mm, "end": v(-6.65, -16.05) * mm});
            skLineSegment(sketch, "E1390", {"start": v(-6.65, -16.05) * mm, "end": v(-6.65, -16.1) * mm});
            skLineSegment(sketch, "E1391", {"start": v(-6.65, -16.1) * mm, "end": v(-6.54, -16.1) * mm});
            skLineSegment(sketch, "E1392", {"start": v(-6.54, -16.1) * mm, "end": v(-6.43, -16.22) * mm});
            skLineSegment(sketch, "E1393", {"start": v(-6.43, -16.22) * mm, "end": v(-6.27, -16.28) * mm});
            skLineSegment(sketch, "E1394", {"start": v(-6.27, -16.28) * mm, "end": v(-6.1, -16.28) * mm});
            skLineSegment(sketch, "E1395", {"start": v(-6.1, -16.28) * mm, "end": v(-5.93, -16.33) * mm});
            skLineSegment(sketch, "E1396", {"start": v(-5.93, -16.33) * mm, "end": v(-5.82, -16.44) * mm});
            skLineSegment(sketch, "E1397", {"start": v(-5.82, -16.44) * mm, "end": v(-5.66, -16.5) * mm});
            skLineSegment(sketch, "E1398", {"start": v(-5.66, -16.5) * mm, "end": v(-5.49, -16.5) * mm});
            skLineSegment(sketch, "E1399", {"start": v(-5.49, -16.5) * mm, "end": v(-5.49, -16.55) * mm});
            skLineSegment(sketch, "E1400", {"start": v(-5.49, -16.55) * mm, "end": v(-5.32, -16.55) * mm});
            skLineSegment(sketch, "E1401", {"start": v(-5.32, -16.55) * mm, "end": v(-5.32, -16.6) * mm});
            skLineSegment(sketch, "E1402", {"start": v(-5.32, -16.6) * mm, "end": v(-5.1, -16.6) * mm});
            skLineSegment(sketch, "E1403", {"start": v(-5.1, -16.6) * mm, "end": v(-4.94, -16.66) * mm});
            skLineSegment(sketch, "E1404", {"start": v(-4.94, -16.66) * mm, "end": v(-4.94, -16.72) * mm});
            skLineSegment(sketch, "E1405", {"start": v(-4.94, -16.72) * mm, "end": v(-4.77, -16.72) * mm});
            skLineSegment(sketch, "E1406", {"start": v(-4.77, -16.72) * mm, "end": v(-4.77, -16.77) * mm});
            skLineSegment(sketch, "E1407", {"start": v(-4.77, -16.77) * mm, "end": v(-4.6, -16.83) * mm});
            skLineSegment(sketch, "E1408", {"start": v(-4.6, -16.83) * mm, "end": v(-4.33, -16.83) * mm});
            skLineSegment(sketch, "E1409", {"start": v(-4.33, -16.83) * mm, "end": v(-4.33, -16.89) * mm});
            skLineSegment(sketch, "E1410", {"start": v(-4.33, -16.89) * mm, "end": v(-4.1, -16.89) * mm});
            skLineSegment(sketch, "E1411", {"start": v(-4.1, -16.89) * mm, "end": v(-4.1, -16.94) * mm});
            skLineSegment(sketch, "E1412", {"start": v(-4.1, -16.94) * mm, "end": v(-3.88, -16.94) * mm});
            skLineSegment(sketch, "E1413", {"start": v(-3.88, -16.94) * mm, "end": v(-3.88, -17) * mm});
            skLineSegment(sketch, "E1414", {"start": v(-3.88, -17) * mm, "end": v(-3.66, -17) * mm});
            skLineSegment(sketch, "E1415", {"start": v(-3.66, -17) * mm, "end": v(-3.66, -17.05) * mm});
            skLineSegment(sketch, "E1416", {"start": v(-3.66, -17.05) * mm, "end": v(-3.44, -17.05) * mm});
            skLineSegment(sketch, "E1417", {"start": v(-3.44, -17.05) * mm, "end": v(-3.44, -17.1) * mm});
            skLineSegment(sketch, "E1418", {"start": v(-3.44, -17.1) * mm, "end": v(-3.05, -17.1) * mm});
            skLineSegment(sketch, "E1419", {"start": v(-3.05, -17.1) * mm, "end": v(-3.05, -17.16) * mm});
            skLineSegment(sketch, "E1420", {"start": v(-3.05, -17.16) * mm, "end": v(-2.72, -17.16) * mm});
            skLineSegment(sketch, "E1421", {"start": v(-2.72, -17.16) * mm, "end": v(-2.72, -17.22) * mm});
            skLineSegment(sketch, "E1422", {"start": v(-2.72, -17.22) * mm, "end": v(-2.38, -17.22) * mm});
            skLineSegment(sketch, "E1423", {"start": v(-2.38, -17.22) * mm, "end": v(-2.38, -17.27) * mm});
            skLineSegment(sketch, "E1424", {"start": v(-2.38, -17.27) * mm, "end": v(-2.22, -17.27) * mm});
            skLineSegment(sketch, "E1425", {"start": v(-2.22, -17.27) * mm, "end": v(-1.83, -17.27) * mm});
            skLineSegment(sketch, "E1426", {"start": v(-1.83, -17.27) * mm, "end": v(-1.83, -17.33) * mm});
            skLineSegment(sketch, "E1427", {"start": v(-1.83, -17.33) * mm, "end": v(-1.39, -17.33) * mm});
            skLineSegment(sketch, "E1428", {"start": v(-1.39, -17.33) * mm, "end": v(-1.39, -17.38) * mm});
            skLineSegment(sketch, "E1429", {"start": v(-1.39, -17.38) * mm, "end": v(-1.22, -17.38) * mm});
            skLineSegment(sketch, "E1430", {"start": v(-1.22, -17.38) * mm, "end": v(-1, -17.38) * mm});
            skLineSegment(sketch, "E1431", {"start": v(-1, -17.38) * mm, "end": v(-0.94, -17.38) * mm});
            skLineSegment(sketch, "E1432", {"start": v(-0.94, -17.38) * mm, "end": v(-0.89, -17.38) * mm});
            skLineSegment(sketch, "E1433", {"start": v(-0.89, -17.38) * mm, "end": v(-0.83, -17.38) * mm});
            skLineSegment(sketch, "E1434", {"start": v(-0.83, -17.38) * mm, "end": v(-0.78, -17.38) * mm});
            skLineSegment(sketch, "E1435", {"start": v(-0.78, -17.38) * mm, "end": v(-0.72, -17.38) * mm});
            skLineSegment(sketch, "E1436", {"start": v(-0.72, -17.38) * mm, "end": v(-0.67, -17.38) * mm});
            skLineSegment(sketch, "E1437", {"start": v(-0.67, -17.38) * mm, "end": v(-0.61, -17.38) * mm});
            skLineSegment(sketch, "E1438", {"start": v(-0.61, -17.38) * mm, "end": v(-0.22, -17.38) * mm});
            skLineSegment(sketch, "E1439", {"start": v(-0.22, -17.38) * mm, "end": v(-0.22, -17.44) * mm});
            skLineSegment(sketch, "E1440", {"start": v(-0.22, -17.44) * mm, "end": v(0.22, -17.44) * mm});
            skLineSegment(sketch, "E1441", {"start": v(0.22, -17.44) * mm, "end": v(0.22, -17.38) * mm});
            skLineSegment(sketch, "E1442", {"start": v(0.22, -17.38) * mm, "end": v(0.39, -17.38) * mm});
            skLineSegment(sketch, "E1443", {"start": v(0.39, -17.38) * mm, "end": v(0.6, -17.38) * mm});
            skLineSegment(sketch, "E1444", {"start": v(0.6, -17.38) * mm, "end": v(0.67, -17.38) * mm});
            skLineSegment(sketch, "E1445", {"start": v(0.67, -17.38) * mm, "end": v(0.72, -17.38) * mm});
            skLineSegment(sketch, "E1446", {"start": v(0.72, -17.38) * mm, "end": v(0.78, -17.38) * mm});
            skLineSegment(sketch, "E1447", {"start": v(0.78, -17.38) * mm, "end": v(0.83, -17.38) * mm});
            skLineSegment(sketch, "E1448", {"start": v(0.83, -17.38) * mm, "end": v(0.89, -17.38) * mm});
            skLineSegment(sketch, "E1449", {"start": v(0.89, -17.38) * mm, "end": v(0.94, -17.38) * mm});
            skLineSegment(sketch, "E1450", {"start": v(0.94, -17.38) * mm, "end": v(1, -17.38) * mm});
            skLineSegment(sketch, "E1451", {"start": v(1, -17.38) * mm, "end": v(1.05, -17.38) * mm});
            skLineSegment(sketch, "E1452", {"start": v(1.05, -17.38) * mm, "end": v(1.1, -17.38) * mm});
            skLineSegment(sketch, "E1453", {"start": v(1.1, -17.38) * mm, "end": v(1.16, -17.38) * mm});
            skLineSegment(sketch, "E1454", {"start": v(1.16, -17.38) * mm, "end": v(1.22, -17.38) * mm});
            skLineSegment(sketch, "E1455", {"start": v(1.22, -17.38) * mm, "end": v(1.44, -17.38) * mm});
            skLineSegment(sketch, "E1456", {"start": v(1.44, -17.38) * mm, "end": v(1.44, -17.33) * mm});
            skLineSegment(sketch, "E1457", {"start": v(1.44, -17.33) * mm, "end": v(1.83, -17.33) * mm});
            skLineSegment(sketch, "E1458", {"start": v(1.83, -17.33) * mm, "end": v(1.83, -17.27) * mm});
            skLineSegment(sketch, "E1459", {"start": v(1.83, -17.27) * mm, "end": v(2, -17.27) * mm});
            skLineSegment(sketch, "E1460", {"start": v(2, -17.27) * mm, "end": v(2.16, -17.27) * mm});
            skLineSegment(sketch, "E1461", {"start": v(2.16, -17.27) * mm, "end": v(2.33, -17.27) * mm});
            skLineSegment(sketch, "E1462", {"start": v(2.33, -17.27) * mm, "end": v(2.33, -17.22) * mm});
            skLineSegment(sketch, "E1463", {"start": v(2.33, -17.22) * mm, "end": v(2.72, -17.22) * mm});
            skLineSegment(sketch, "E1464", {"start": v(2.72, -17.22) * mm, "end": v(2.72, -17.16) * mm});
            skLineSegment(sketch, "E1465", {"start": v(2.72, -17.16) * mm, "end": v(3.1, -17.16) * mm});
            skLineSegment(sketch, "E1466", {"start": v(3.1, -17.16) * mm, "end": v(3.1, -17.1) * mm});
            skLineSegment(sketch, "E1467", {"start": v(3.1, -17.1) * mm, "end": v(3.44, -17.1) * mm});
            skLineSegment(sketch, "E1468", {"start": v(3.44, -17.1) * mm, "end": v(3.44, -17.05) * mm});
            skLineSegment(sketch, "E1469", {"start": v(3.44, -17.05) * mm, "end": v(3.66, -17.05) * mm});
            skLineSegment(sketch, "E1470", {"start": v(3.66, -17.05) * mm, "end": v(3.66, -17) * mm});
            skLineSegment(sketch, "E1471", {"start": v(3.66, -17) * mm, "end": v(3.88, -17) * mm});
            skLineSegment(sketch, "E1472", {"start": v(3.88, -17) * mm, "end": v(3.88, -16.94) * mm});
            skLineSegment(sketch, "E1473", {"start": v(3.88, -16.94) * mm, "end": v(4.1, -16.94) * mm});
            skLineSegment(sketch, "E1474", {"start": v(4.1, -16.94) * mm, "end": v(4.1, -16.89) * mm});
            skLineSegment(sketch, "E1475", {"start": v(4.1, -16.89) * mm, "end": v(4.33, -16.89) * mm});
            skLineSegment(sketch, "E1476", {"start": v(4.33, -16.89) * mm, "end": v(4.33, -16.83) * mm});
            skLineSegment(sketch, "E1477", {"start": v(4.33, -16.83) * mm, "end": v(4.6, -16.83) * mm});
            skLineSegment(sketch, "E1478", {"start": v(4.6, -16.83) * mm, "end": v(4.77, -16.77) * mm});
            skLineSegment(sketch, "E1479", {"start": v(4.77, -16.77) * mm, "end": v(4.77, -16.72) * mm});
            skLineSegment(sketch, "E1480", {"start": v(4.77, -16.72) * mm, "end": v(4.94, -16.66) * mm});
            skLineSegment(sketch, "E1481", {"start": v(4.94, -16.66) * mm, "end": v(5.16, -16.66) * mm});
            skLineSegment(sketch, "E1482", {"start": v(5.16, -16.66) * mm, "end": v(5.32, -16.6) * mm});
            skLineSegment(sketch, "E1483", {"start": v(5.32, -16.6) * mm, "end": v(5.32, -16.55) * mm});
            skLineSegment(sketch, "E1484", {"start": v(5.32, -16.55) * mm, "end": v(5.49, -16.55) * mm});
            skLineSegment(sketch, "E1485", {"start": v(5.49, -16.55) * mm, "end": v(5.49, -16.5) * mm});
            skLineSegment(sketch, "E1486", {"start": v(5.49, -16.5) * mm, "end": v(5.66, -16.5) * mm});
            skLineSegment(sketch, "E1487", {"start": v(5.66, -16.5) * mm, "end": v(5.66, -16.44) * mm});
            skLineSegment(sketch, "E1488", {"start": v(5.66, -16.44) * mm, "end": v(5.82, -16.44) * mm});
            skLineSegment(sketch, "E1489", {"start": v(5.82, -16.44) * mm, "end": v(5.93, -16.33) * mm});
            skLineSegment(sketch, "E1490", {"start": v(5.93, -16.33) * mm, "end": v(6.1, -16.28) * mm});
            skLineSegment(sketch, "E1491", {"start": v(6.1, -16.28) * mm, "end": v(6.27, -16.28) * mm});
            skLineSegment(sketch, "E1492", {"start": v(6.27, -16.28) * mm, "end": v(6.43, -16.22) * mm});
            skLineSegment(sketch, "E1493", {"start": v(6.43, -16.22) * mm, "end": v(6.54, -16.1) * mm});
            skLineSegment(sketch, "E1494", {"start": v(6.54, -16.1) * mm, "end": v(6.65, -16.1) * mm});
            skLineSegment(sketch, "E1495", {"start": v(6.65, -16.1) * mm, "end": v(6.65, -16.05) * mm});
            skLineSegment(sketch, "E1496", {"start": v(6.65, -16.05) * mm, "end": v(6.77, -16) * mm});
            skLineSegment(sketch, "E1497", {"start": v(6.77, -16) * mm, "end": v(6.93, -16) * mm});
            skLineSegment(sketch, "E1498", {"start": v(6.93, -16) * mm, "end": v(7.04, -15.89) * mm});
            skLineSegment(sketch, "E1499", {"start": v(7.04, -15.89) * mm, "end": v(7.2, -15.89) * mm});
            skLineSegment(sketch, "E1500", {"start": v(7.2, -15.89) * mm, "end": v(7.32, -15.83) * mm});
            skLineSegment(sketch, "E1501", {"start": v(7.32, -15.83) * mm, "end": v(7.32, -15.78) * mm});
            skLineSegment(sketch, "E1502", {"start": v(7.32, -15.78) * mm, "end": v(7.43, -15.78) * mm});
            skLineSegment(sketch, "E1503", {"start": v(7.43, -15.78) * mm, "end": v(7.43, -15.72) * mm});
            skLineSegment(sketch, "E1504", {"start": v(7.43, -15.72) * mm, "end": v(7.54, -15.72) * mm});
            skLineSegment(sketch, "E1505", {"start": v(7.54, -15.72) * mm, "end": v(7.54, -15.67) * mm});
            skLineSegment(sketch, "E1506", {"start": v(7.54, -15.67) * mm, "end": v(7.65, -15.67) * mm});
            skLineSegment(sketch, "E1507", {"start": v(7.65, -15.67) * mm, "end": v(7.65, -15.6) * mm});
            skLineSegment(sketch, "E1508", {"start": v(7.65, -15.6) * mm, "end": v(7.76, -15.6) * mm});
            skLineSegment(sketch, "E1509", {"start": v(7.76, -15.6) * mm, "end": v(7.87, -15.55) * mm});
            skLineSegment(sketch, "E1510", {"start": v(7.87, -15.55) * mm, "end": v(7.93, -15.44) * mm});
            skLineSegment(sketch, "E1511", {"start": v(7.93, -15.44) * mm, "end": v(8.2, -15.39) * mm});
            skLineSegment(sketch, "E1512", {"start": v(8.2, -15.39) * mm, "end": v(8.37, -15.28) * mm});
            skLineSegment(sketch, "E1513", {"start": v(8.37, -15.28) * mm, "end": v(8.43, -15.22) * mm});
            skLineSegment(sketch, "E1514", {"start": v(8.43, -15.22) * mm, "end": v(8.43, -15.11) * mm});
            skLineSegment(sketch, "E1515", {"start": v(8.43, -15.11) * mm, "end": v(8.48, -15.11) * mm});
            skLineSegment(sketch, "E1516", {"start": v(8.48, -15.11) * mm, "end": v(8.54, -15) * mm});
            skLineSegment(sketch, "E1517", {"start": v(8.54, -15) * mm, "end": v(8.54, -14.72) * mm});
            skLineSegment(sketch, "E1518", {"start": v(8.54, -14.72) * mm, "end": v(8.48, -14.56) * mm});
            skLineSegment(sketch, "E1519", {"start": v(8.48, -14.56) * mm, "end": v(8.37, -14.4) * mm});
            skLineSegment(sketch, "E1520", {"start": v(8.37, -14.4) * mm, "end": v(8.26, -14.33) * mm});
            skLineSegment(sketch, "E1521", {"start": v(8.26, -14.33) * mm, "end": v(8.26, -14.22) * mm});
            skLineSegment(sketch, "E1522", {"start": v(8.26, -14.22) * mm, "end": v(8.2, -14.22) * mm});
            skLineSegment(sketch, "E1523", {"start": v(8.2, -14.22) * mm, "end": v(8.2, -14.11) * mm});
            skLineSegment(sketch, "E1524", {"start": v(8.2, -14.11) * mm, "end": v(8.15, -14) * mm});
            skLineSegment(sketch, "E1525", {"start": v(8.15, -14) * mm, "end": v(8.04, -13.95) * mm});
            skLineSegment(sketch, "E1526", {"start": v(8.04, -13.95) * mm, "end": v(8.04, -13.84) * mm});
            skLineSegment(sketch, "E1527", {"start": v(8.04, -13.84) * mm, "end": v(7.93, -13.78) * mm});
            skLineSegment(sketch, "E1528", {"start": v(7.93, -13.78) * mm, "end": v(7.87, -13.56) * mm});
            skLineSegment(sketch, "E1529", {"start": v(7.87, -13.56) * mm, "end": v(7.76, -13.5) * mm});
            skLineSegment(sketch, "E1530", {"start": v(7.76, -13.5) * mm, "end": v(7.7, -13.28) * mm});
            skLineSegment(sketch, "E1531", {"start": v(7.7, -13.28) * mm, "end": v(7.6, -13.23) * mm});
            skLineSegment(sketch, "E1532", {"start": v(7.6, -13.23) * mm, "end": v(7.6, -13.11) * mm});
            skLineSegment(sketch, "E1533", {"start": v(7.6, -13.11) * mm, "end": v(7.54, -13.11) * mm});
            skLineSegment(sketch, "E1534", {"start": v(7.54, -13.11) * mm, "end": v(7.54, -13) * mm});
            skLineSegment(sketch, "E1535", {"start": v(7.54, -13) * mm, "end": v(7.49, -12.9) * mm});
            skLineSegment(sketch, "E1536", {"start": v(7.49, -12.9) * mm, "end": v(7.38, -12.84) * mm});
            skLineSegment(sketch, "E1537", {"start": v(7.38, -12.84) * mm, "end": v(7.32, -12.62) * mm});
            skLineSegment(sketch, "E1538", {"start": v(7.32, -12.62) * mm, "end": v(7.2, -12.56) * mm});
            skLineSegment(sketch, "E1539", {"start": v(7.2, -12.56) * mm, "end": v(7.15, -12.34) * mm});
            skLineSegment(sketch, "E1540", {"start": v(7.15, -12.34) * mm, "end": v(7.04, -12.28) * mm});
            skLineSegment(sketch, "E1541", {"start": v(7.04, -12.28) * mm, "end": v(7.04, -12.17) * mm});
            skLineSegment(sketch, "E1542", {"start": v(7.04, -12.17) * mm, "end": v(6.99, -12.17) * mm});
            skLineSegment(sketch, "E1543", {"start": v(6.99, -12.17) * mm, "end": v(6.99, -12.06) * mm});
            skLineSegment(sketch, "E1544", {"start": v(6.99, -12.06) * mm, "end": v(6.93, -11.95) * mm});
            skLineSegment(sketch, "E1545", {"start": v(6.93, -11.95) * mm, "end": v(6.77, -11.84) * mm});
            skLineSegment(sketch, "E1546", {"start": v(6.77, -11.84) * mm, "end": v(6.65, -11.5) * mm});
            skLineSegment(sketch, "E1547", {"start": v(6.65, -11.5) * mm, "end": v(6.54, -11.45) * mm});
            skLineSegment(sketch, "E1548", {"start": v(6.54, -11.45) * mm, "end": v(6.54, -11.34) * mm});
            skLineSegment(sketch, "E1549", {"start": v(6.54, -11.34) * mm, "end": v(6.43, -11.28) * mm});
            skLineSegment(sketch, "E1550", {"start": v(6.43, -11.28) * mm, "end": v(6.43, -11.17) * mm});
            skLineSegment(sketch, "E1551", {"start": v(6.43, -11.17) * mm, "end": v(6.38, -11.17) * mm});
            skLineSegment(sketch, "E1552", {"start": v(6.38, -11.17) * mm, "end": v(6.38, -11.06) * mm});
            skLineSegment(sketch, "E1553", {"start": v(6.38, -11.06) * mm, "end": v(6.32, -10.95) * mm});
            skLineSegment(sketch, "E1554", {"start": v(6.32, -10.95) * mm, "end": v(6.21, -10.9) * mm});
            skLineSegment(sketch, "E1555", {"start": v(6.21, -10.9) * mm, "end": v(6.21, -10.79) * mm});
            skLineSegment(sketch, "E1556", {"start": v(6.21, -10.79) * mm, "end": v(6.1, -10.73) * mm});
            skLineSegment(sketch, "E1557", {"start": v(6.1, -10.73) * mm, "end": v(6.1, -10.62) * mm});
            skLineSegment(sketch, "E1558", {"start": v(6.1, -10.62) * mm, "end": v(6.04, -10.62) * mm});
            skLineSegment(sketch, "E1559", {"start": v(6.04, -10.62) * mm, "end": v(6.04, -10.5) * mm});
            skLineSegment(sketch, "E1560", {"start": v(6.04, -10.5) * mm, "end": v(5.99, -10.4) * mm});
            skLineSegment(sketch, "E1561", {"start": v(5.99, -10.4) * mm, "end": v(5.88, -10.34) * mm});
            skLineSegment(sketch, "E1562", {"start": v(5.88, -10.34) * mm, "end": v(5.82, -10.12) * mm});
            skLineSegment(sketch, "E1563", {"start": v(5.82, -10.12) * mm, "end": v(5.71, -10.06) * mm});
            skLineSegment(sketch, "E1564", {"start": v(5.71, -10.06) * mm, "end": v(5.66, -9.84) * mm});
            skLineSegment(sketch, "E1565", {"start": v(5.66, -9.84) * mm, "end": v(5.55, -9.79) * mm});
            skLineSegment(sketch, "E1566", {"start": v(5.55, -9.79) * mm, "end": v(5.49, -9.57) * mm});
            skLineSegment(sketch, "E1567", {"start": v(5.49, -9.57) * mm, "end": v(5.38, -9.51) * mm});
            skLineSegment(sketch, "E1568", {"start": v(5.38, -9.51) * mm, "end": v(5.32, -9.29) * mm});
            skLineSegment(sketch, "E1569", {"start": v(5.32, -9.29) * mm, "end": v(5.21, -9.23) * mm});
            skLineSegment(sketch, "E1570", {"start": v(5.21, -9.23) * mm, "end": v(5.16, -9.01) * mm});
            skLineSegment(sketch, "E1571", {"start": v(5.16, -9.01) * mm, "end": v(5.05, -8.96) * mm});
            skLineSegment(sketch, "E1572", {"start": v(5.05, -8.96) * mm, "end": v(5.05, -8.84) * mm});
            skLineSegment(sketch, "E1573", {"start": v(5.05, -8.84) * mm, "end": v(4.94, -8.79) * mm});
            skLineSegment(sketch, "E1574", {"start": v(4.94, -8.79) * mm, "end": v(4.94, -8.68) * mm});
            skLineSegment(sketch, "E1575", {"start": v(4.94, -8.68) * mm, "end": v(4.88, -8.68) * mm});
            skLineSegment(sketch, "E1576", {"start": v(4.88, -8.68) * mm, "end": v(4.88, -8.57) * mm});
            skLineSegment(sketch, "E1577", {"start": v(4.88, -8.57) * mm, "end": v(4.82, -8.46) * mm});
            skLineSegment(sketch, "E1578", {"start": v(4.82, -8.46) * mm, "end": v(4.71, -8.4) * mm});
            skLineSegment(sketch, "E1579", {"start": v(4.71, -8.4) * mm, "end": v(4.71, -8.3) * mm});
            skLineSegment(sketch, "E1580", {"start": v(4.71, -8.3) * mm, "end": v(4.6, -8.23) * mm});
            skLineSegment(sketch, "E1581", {"start": v(4.6, -8.23) * mm, "end": v(4.6, -8.12) * mm});
            skLineSegment(sketch, "E1582", {"start": v(4.6, -8.12) * mm, "end": v(4.55, -8.12) * mm});
            skLineSegment(sketch, "E1583", {"start": v(4.55, -8.12) * mm, "end": v(4.55, -8.01) * mm});
            skLineSegment(sketch, "E1584", {"start": v(4.55, -8.01) * mm, "end": v(4.5, -7.9) * mm});
            skLineSegment(sketch, "E1585", {"start": v(4.5, -7.9) * mm, "end": v(4.38, -7.85) * mm});
            skLineSegment(sketch, "E1586", {"start": v(4.38, -7.85) * mm, "end": v(4.38, -7.74) * mm});
            skLineSegment(sketch, "E1587", {"start": v(4.38, -7.74) * mm, "end": v(4.27, -7.68) * mm});
            skLineSegment(sketch, "E1588", {"start": v(4.27, -7.68) * mm, "end": v(4.27, -7.57) * mm});
            skLineSegment(sketch, "E1589", {"start": v(4.27, -7.57) * mm, "end": v(4.21, -7.57) * mm});
            skLineSegment(sketch, "E1590", {"start": v(4.21, -7.57) * mm, "end": v(4.21, -7.46) * mm});
            skLineSegment(sketch, "E1591", {"start": v(4.21, -7.46) * mm, "end": v(4.16, -7.35) * mm});
            skLineSegment(sketch, "E1592", {"start": v(4.16, -7.35) * mm, "end": v(4.05, -7.3) * mm});
            skLineSegment(sketch, "E1593", {"start": v(4.05, -7.3) * mm, "end": v(4, -7.07) * mm});
            skLineSegment(sketch, "E1594", {"start": v(4, -7.07) * mm, "end": v(3.88, -7.01) * mm});
            skLineSegment(sketch, "E1595", {"start": v(3.88, -7.01) * mm, "end": v(3.83, -6.8) * mm});
            skLineSegment(sketch, "E1596", {"start": v(3.83, -6.8) * mm, "end": v(3.72, -6.74) * mm});
            skLineSegment(sketch, "E1597", {"start": v(3.72, -6.74) * mm, "end": v(3.66, -6.52) * mm});
            skLineSegment(sketch, "E1598", {"start": v(3.66, -6.52) * mm, "end": v(3.55, -6.46) * mm});
            skLineSegment(sketch, "E1599", {"start": v(3.55, -6.46) * mm, "end": v(3.5, -6.24) * mm});
            skLineSegment(sketch, "E1600", {"start": v(3.5, -6.24) * mm, "end": v(3.38, -6.18) * mm});
            skLineSegment(sketch, "E1601", {"start": v(3.38, -6.18) * mm, "end": v(3.33, -5.96) * mm});
            skLineSegment(sketch, "E1602", {"start": v(3.33, -5.96) * mm, "end": v(3.22, -5.9) * mm});
            skLineSegment(sketch, "E1603", {"start": v(3.22, -5.9) * mm, "end": v(3.22, -5.8) * mm});
            skLineSegment(sketch, "E1604", {"start": v(3.22, -5.8) * mm, "end": v(3.1, -5.74) * mm});
            skLineSegment(sketch, "E1605", {"start": v(3.1, -5.74) * mm, "end": v(3.1, -5.63) * mm});
            skLineSegment(sketch, "E1606", {"start": v(3.1, -5.63) * mm, "end": v(3.05, -5.63) * mm});
            skLineSegment(sketch, "E1607", {"start": v(3.05, -5.63) * mm, "end": v(3.05, -5.52) * mm});
            skLineSegment(sketch, "E1608", {"start": v(3.05, -5.52) * mm, "end": v(3, -5.4) * mm});
            skLineSegment(sketch, "E1609", {"start": v(3, -5.4) * mm, "end": v(2.88, -5.35) * mm});
            skLineSegment(sketch, "E1610", {"start": v(2.88, -5.35) * mm, "end": v(2.88, -5.24) * mm});
            skLineSegment(sketch, "E1611", {"start": v(2.88, -5.24) * mm, "end": v(2.77, -5.18) * mm});
            skLineSegment(sketch, "E1612", {"start": v(2.77, -5.18) * mm, "end": v(2.66, -4.96) * mm});
            skLineSegment(sketch, "E1613", {"start": v(2.66, -4.96) * mm, "end": v(2.5, -4.9) * mm});
            skLineSegment(sketch, "E1614", {"start": v(2.5, -4.9) * mm, "end": v(2, -4.9) * mm});
            skLineSegment(sketch, "E1615", {"start": v(2, -4.9) * mm, "end": v(1.83, -4.96) * mm});
            skLineSegment(sketch, "E1616", {"start": v(1.83, -4.96) * mm, "end": v(1.83, -5.02) * mm});
            skLineSegment(sketch, "E1617", {"start": v(1.83, -5.02) * mm, "end": v(1.66, -5.02) * mm});
            skLineSegment(sketch, "E1618", {"start": v(1.66, -5.02) * mm, "end": v(1.55, -5.13) * mm});
            skLineSegment(sketch, "E1619", {"start": v(1.55, -5.13) * mm, "end": v(1.28, -5.13) * mm});
            skLineSegment(sketch, "E1620", {"start": v(1.28, -5.13) * mm, "end": v(1.1, -5.24) * mm});
            skLineSegment(sketch, "E1621", {"start": v(1.1, -5.24) * mm, "end": v(0.72, -5.24) * mm});
            skLineSegment(sketch, "E1622", {"start": v(0.72, -5.24) * mm, "end": v(0.72, -5.3) * mm});
            skLineSegment(sketch, "E1623", {"start": v(0.72, -5.3) * mm, "end": v(0.55, -5.3) * mm});
            skLineSegment(sketch, "E1624", {"start": v(0.55, -5.3) * mm, "end": v(0.33, -5.3) * mm});
            skLineSegment(sketch, "E1625", {"start": v(0.33, -5.3) * mm, "end": v(0.28, -5.3) * mm});
            skLineSegment(sketch, "E1626", {"start": v(0.28, -5.3) * mm, "end": v(0.22, -5.3) * mm});
            skLineSegment(sketch, "E1627", {"start": v(0.22, -5.3) * mm, "end": v(0.17, -5.3) * mm});
            skLineSegment(sketch, "E1628", {"start": v(0.17, -5.3) * mm, "end": v(0.11, -5.3) * mm});
            skLineSegment(sketch, "E1629", {"start": v(0.11, -5.3) * mm, "end": v(0.06, -5.3) * mm});
            skLineSegment(sketch, "E1630", {"start": v(0.06, -5.3) * mm, "end": v(0, -5.3) * mm});
            skLineSegment(sketch, "E1631", {"start": v(0, -5.3) * mm, "end": v(-0.06, -5.3) * mm});
            skLineSegment(sketch, "E1632", {"start": v(-0.06, -5.3) * mm, "end": v(-0.11, -5.3) * mm});
            skLineSegment(sketch, "E1633", {"start": v(-0.11, -5.3) * mm, "end": v(-0.17, -5.3) * mm});
            skLineSegment(sketch, "E1634", {"start": v(-0.17, -5.3) * mm, "end": v(-0.22, -5.3) * mm});
            skLineSegment(sketch, "E1635", {"start": v(-0.22, -5.3) * mm, "end": v(-0.28, -5.3) * mm});
            skLineSegment(sketch, "E1636", {"start": v(-0.28, -5.3) * mm, "end": v(-0.33, -5.3) * mm});
            skLineSegment(sketch, "E1637", {"start": v(-0.33, -5.3) * mm, "end": v(-0.39, -5.3) * mm});
            skLineSegment(sketch, "E1638", {"start": v(-0.39, -5.3) * mm, "end": v(-0.44, -5.3) * mm});
            skLineSegment(sketch, "E1639", {"start": v(-0.44, -5.3) * mm, "end": v(-0.5, -5.3) * mm});
            skLineSegment(sketch, "E1640", {"start": v(-0.5, -5.3) * mm, "end": v(-0.72, -5.3) * mm});
            skLineSegment(sketch, "E1641", {"start": v(-0.72, -5.3) * mm, "end": v(-0.72, -5.24) * mm});
            skLineSegment(sketch, "E1642", {"start": v(-0.72, -5.24) * mm, "end": v(-1.05, -5.24) * mm});
            skLineSegment(sketch, "E1643", {"start": v(-1.05, -5.24) * mm, "end": v(-1.05, -5.18) * mm});
            skLineSegment(sketch, "E1644", {"start": v(-1.05, -5.18) * mm, "end": v(-1.28, -5.18) * mm});
            skLineSegment(sketch, "E1645", {"start": v(-1.28, -5.18) * mm, "end": v(-1.28, -5.13) * mm});
            skLineSegment(sketch, "E1646", {"start": v(-1.28, -5.13) * mm, "end": v(-1.5, -5.13) * mm});
            skLineSegment(sketch, "E1647", {"start": v(-1.5, -5.13) * mm, "end": v(-1.66, -5.07) * mm});
            skLineSegment(sketch, "E1648", {"start": v(-1.66, -5.07) * mm, "end": v(-1.66, -5.02) * mm});
            skLineSegment(sketch, "E1649", {"start": v(-1.66, -5.02) * mm, "end": v(-1.83, -5.02) * mm});
            skLineSegment(sketch, "E1650", {"start": v(-1.83, -5.02) * mm, "end": v(-1.83, -4.96) * mm});
            skLineSegment(sketch, "E1651", {"start": v(-1.83, -4.96) * mm, "end": v(-2, -4.96) * mm});
            skLineSegment(sketch, "E1652", {"start": v(-2, -4.96) * mm, "end": v(-2.22, -4.8) * mm});
            skLineSegment(sketch, "E1653", {"start": v(-2.22, -4.8) * mm, "end": v(-2.44, -4.74) * mm});
            skLineSegment(sketch, "E1654", {"start": v(-2.44, -4.74) * mm, "end": v(-2.6, -4.74) * mm});
            skLineSegment(sketch, "E1655", {"start": v(-0.33, -1.75) * mm, "end": v(0, -1.75) * mm});
            skPoint(sketch, "E1656.orphan", {"position": v(0, 1.7) * mm});
            skPoint(sketch, "E1657.start.orphan", {"position": v(-1.72, 0) * mm});
            skSolve(sketch);
        }
        {
            var Q0;
            Q0 = qSketchRegion(id + "F7", true);
            extrude(context, id + "F8", {"entities" : qUnion([Q0]), "operationType" : NewBodyOperationType.REMOVE, "oppositeDirection" : true, "depth" : 3 * mm, "offsetDistance" : 25 * mm});
        }
    });
